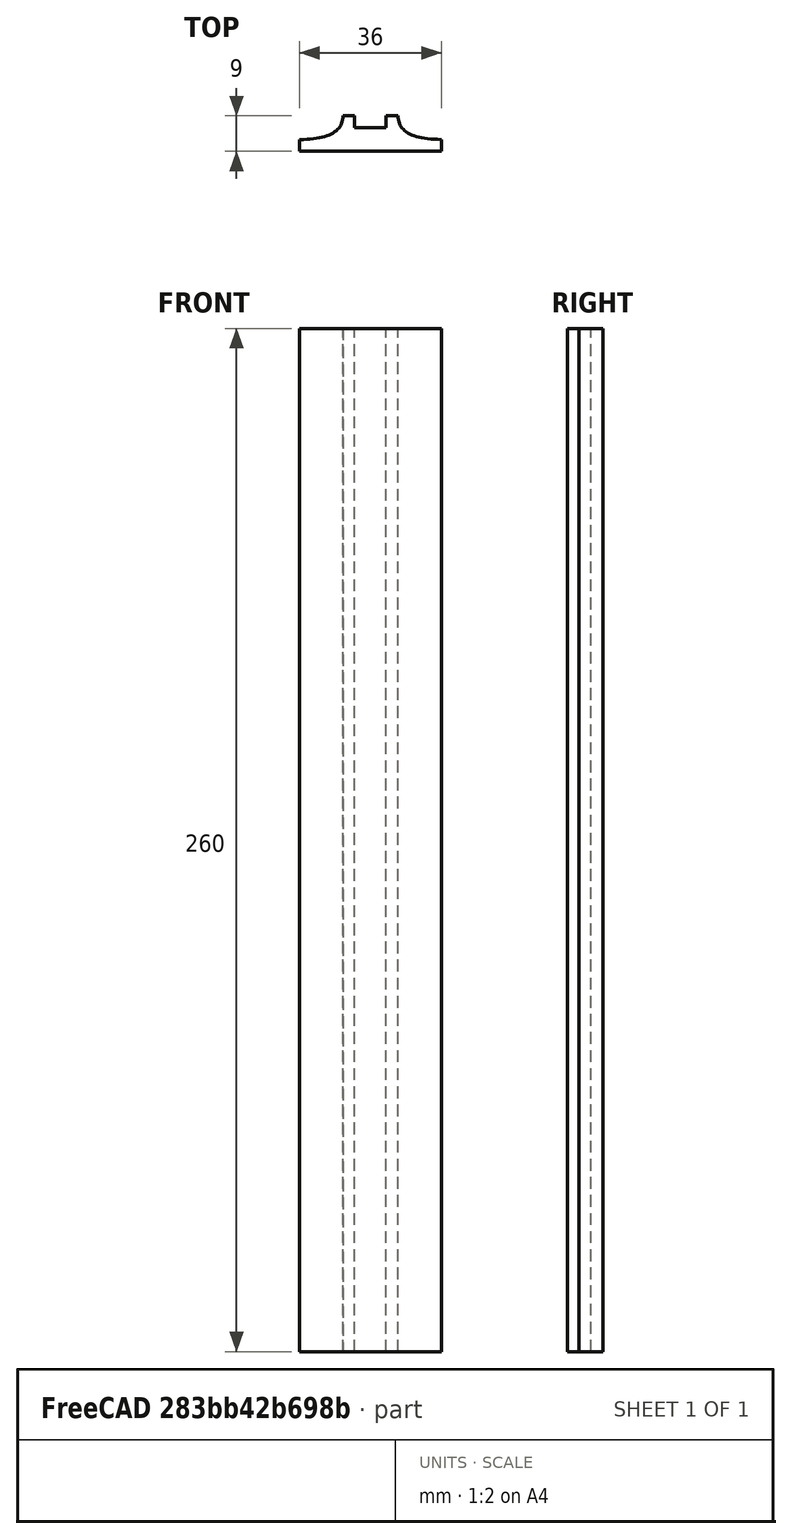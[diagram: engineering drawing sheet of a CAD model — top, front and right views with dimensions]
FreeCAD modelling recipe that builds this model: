
FCSTD DOCUMENT  (FreeCAD 0.19R0.19.2)
Label: laptopStand299.FCStd
License: All rights reserved
LicenseURL: http://en.wikipedia.org/wiki/All_rights_reserved
objects: Sketcher::SketchObject×11, Part::Extrusion×1
note: 12 computed .brp shape members not serialized (recipe doc carries the construction recipe); baked Part::Feature solids carry a one-line shape summary decoded from their .brp

FEATURE [Sketcher::SketchObject] Sketch001  label="legTop"
  FullyConstrained = true
  MapMode = 4
  Placement = pos=(0,0,0) rot=(0.57735,0.57735,0.57735;2.0944rad)
  sketch-geometry (41):
    g0: BSplineCurve PolesCount=3 KnotsCount=2 Degree=2 IsPeriodic=0
    g1: ArcOfCircle CenterX=73.1223 CenterY=-32.291 CenterZ=0 NormalX=0 NormalY=0 NormalZ=1 AngleXU=0 Radius=13 StartAngle=5.92268 EndAngle=9.06428
    g2: ArcOfCircle CenterX=66.7816 CenterY=-49.1439 CenterZ=0 NormalX=0 NormalY=0 NormalZ=1 AngleXU=0 Radius=13 StartAngle=2.78068 EndAngle=5.92131
    g3-g6: Circle x4 (B-spline internal-alignment scaffolding for g7; pole/knot coordinates omitted)
    g7: BSplineCurve PolesCount=4 KnotsCount=2 Degree=3 IsPeriodic=0
    g8: GeomPoint X=28.8094 Y=-19.0875 Z=0
    g9: GeomPoint X=47.0443 Y=-50.4712 Z=0
    g10: Circle CenterX=53.5586 CenterY=-23.2695 CenterZ=0 NormalX=0 NormalY=0 NormalZ=1 AngleXU=0 Radius=3.24518
    g11: LineSegment StartX=17.2232 StartY=-16.0875 StartZ=0 EndX=17.2232 EndY=-19.0875 EndZ=0
    g12: ArcOfCircle CenterX=17.2475 CenterY=-181.166 CenterZ=0 NormalX=0 NormalY=0 NormalZ=1 AngleXU=0 Radius=13 StartAngle=5.92268 EndAngle=7.49361
    g13: ArcOfCircle CenterX=29.5716 CenterY=-148.408 CenterZ=0 NormalX=0 NormalY=0 NormalZ=1 AngleXU=0 Radius=13 StartAngle=4.35228 EndAngle=5.92131
    g14: ArcOfCircle CenterX=35.8967 CenterY=-131.555 CenterZ=0 NormalX=0 NormalY=0 NormalZ=1 AngleXU=0 Radius=13 StartAngle=5.92268 EndAngle=7.49902
    g15: ArcOfCircle CenterX=48.1805 CenterY=-98.7782 CenterZ=0 NormalX=0 NormalY=0 NormalZ=1 AngleXU=0 Radius=13 StartAngle=4.34921 EndAngle=5.92131
    g16: ArcOfCircle CenterX=54.5183 CenterY=-81.9247 CenterZ=0 NormalX=0 NormalY=0 NormalZ=1 AngleXU=0 Radius=13 StartAngle=5.92268 EndAngle=8.70432
    g17: ArcOfCircle CenterX=20.184 CenterY=-217.506 CenterZ=0 NormalX=0 NormalY=0 NormalZ=1 AngleXU=0 Radius=3.81084 StartAngle=1.88136 EndAngle=6.80465
    g18: ArcOfCircle CenterX=36.3663 CenterY=-113.042 CenterZ=0 NormalX=0 NormalY=0 NormalZ=1 AngleXU=0 Radius=3.60555 StartAngle=0.230024 EndAngle=5.3372
    g19: ArcOfCircle CenterX=17.7945 CenterY=-162.686 CenterZ=0 NormalX=0 NormalY=0 NormalZ=1 AngleXU=0 Radius=3.60555 StartAngle=0.230024 EndAngle=5.3372
    g20: ArcOfCircle CenterX=49.8795 CenterY=-62.6074 CenterZ=0 NormalX=0 NormalY=0 NormalZ=1 AngleXU=0 Radius=3.84187 StartAngle=4.46973 EndAngle=9.40343
    g21: LineSegment StartX=48.9563 StartY=-66.3367 StartZ=0 EndX=44.7488 EndY=-73.3482 EndZ=0
    g22: LineSegment StartX=41.085 StartY=-66.3176 StartZ=0 EndX=46.0385 EndY=-62.5254 EndZ=0
    g23: LineSegment StartX=47.0443 StartY=-50.4712 StartZ=0 EndX=41.085 EndY=-66.3176 EndZ=0
    g24: LineSegment StartX=17.2232 StartY=-16.0875 StartZ=0 EndX=117.223 EndY=-16.0875 EndZ=0
    g25: LineSegment StartX=28.8094 StartY=-19.0875 StartZ=0 EndX=17.2232 EndY=-19.0875 EndZ=0
    g26: LineSegment StartX=117.223 StartY=-16.0875 StartZ=0 EndX=117.223 EndY=-19.0875 EndZ=0
    g27: LineSegment StartX=85.2866 StartY=-36.8766 StartZ=0 EndX=78.9396 EndY=-53.7463 EndZ=0
    g28: LineSegment StartX=60.9579 StartY=-27.7053 StartZ=0 EndX=54.6191 EndY=-44.5532 EndZ=0
    g29: LineSegment StartX=23.4884 StartY=-215.608 StartZ=0 EndX=94.6579 EndY=-26.1359 EndZ=0
    g30: LineSegment StartX=19.0195 StartY=-213.878 StartZ=0 EndX=29.4118 EndY=-185.752 EndZ=0
    g31: LineSegment StartX=22.7134 StartY=-166.661 StartZ=0 EndX=21.8316 EndY=-169.001 EndZ=0
    g32: LineSegment StartX=19.9036 StartY=-165.61 StartZ=0 EndX=22.7134 EndY=-166.661 EndZ=0
    g33: LineSegment StartX=21.3051 StartY=-161.864 StartZ=0 EndX=24.1149 EndY=-162.915 EndZ=0
    g34: LineSegment StartX=24.1149 StartY=-162.915 StartZ=0 EndX=24.9906 EndY=-160.574 EndZ=0
    g35: LineSegment StartX=41.7296 StartY=-153.01 StartZ=0 EndX=48.061 EndY=-136.14 EndZ=0
    g36: LineSegment StartX=41.2852 StartY=-117.017 StartZ=0 EndX=40.4148 EndY=-119.365 EndZ=0
    g37: LineSegment StartX=38.4753 StartY=-115.966 StartZ=0 EndX=41.2852 EndY=-117.017 EndZ=0
    g38: LineSegment StartX=39.8769 StartY=-112.22 StartZ=0 EndX=42.6867 EndY=-113.271 EndZ=0
    g39: LineSegment StartX=42.6867 StartY=-113.271 StartZ=0 EndX=43.5622 EndY=-110.93 EndZ=0
    g40: LineSegment StartX=66.6827 StartY=-86.5104 StartZ=0 EndX=60.3386 EndY=-103.381 EndZ=0
  constraints (65):
    c: Block(g0)
    c: Block(g1)
    c: Block(g2)
    c: Weight(g3) = 1
    c: Equal(g3,g4)
    c: Equal(g3,g5)
    c: Equal(g3,g6)
    c: InternalAlignment(g3-g6 -> g7) x4
    c: InternalAlignment(g8,g7)
    c: InternalAlignment(g9,g7)
    c: Block(g10)
    c: Block(g7)
    c: Vertical(g11)
    c: Block(g12)
    c: Block(g13)
    c: Block(g14)
    c: Block(g15)
    c: Block(g16)
    c: Block(g17)
    c: Block(g18)
    c: Block(g19)
    c: Block(g20)
    c: Coincident(g21,g20)
    c: Coincident(g21,g16)
    c: Coincident(g22,g20)
    c: Block(g22)
    c: Coincident(g23,g7)
    c: Coincident(g23,g22)
    c: Coincident(g24,g11)
    c: Horizontal(g24)
    c: Coincident(g25,g7)
    c: Coincident(g25,g11)
    c: Horizontal(g25)
    c: Coincident(g26,g24)
    c: Coincident(g26,g0)
    c: Vertical(g26)
    c: Block(g24)
    c: Coincident(g27,g1)
    c: Coincident(g27,g2)
    c: Coincident(g28,g1)
    c: Coincident(g28,g2)
    c: Coincident(g29,g17)
    c: Coincident(g29,g0)
    c: Coincident(g30,g17)
    c: Coincident(g30,g12)
    c: Coincident(g31,g12)
    c: Coincident(g32,g19)
    c: Coincident(g32,g31)
    c: Block(g31)
    c: Coincident(g33,g19)
    c: Coincident(g34,g33)
    c: Coincident(g34,g13)
    c: Block(g34)
    c: Coincident(g35,g13)
    c: Coincident(g35,g14)
    c: Coincident(g36,g14)
    c: Coincident(g37,g18)
    c: Coincident(g37,g36)
    c: Block(g36)
    c: Coincident(g38,g18)
    c: Coincident(g39,g38)
    c: Coincident(g39,g15)
    c: Block(g39)
    c: Coincident(g40,g16)
    c: Coincident(g40,g15)
FEATURE [Sketcher::SketchObject] Sketch002
  FullyConstrained = true
  sketch-geometry (20):
    g0: LineSegment StartX=-2.77179 StartY=-200.304 StartZ=0 EndX=5.22821 EndY=-200.304 EndZ=0
    g1: LineSegment StartX=5.22821 StartY=-200.304 StartZ=0 EndX=5.22821 EndY=-197.304 EndZ=0
    g2: LineSegment StartX=-2.77179 StartY=-200.304 StartZ=0 EndX=-2.77179 EndY=-197.304 EndZ=0
    g3: LineSegment StartX=5.22821 StartY=-197.304 StartZ=0 EndX=8.22821 EndY=-197.304 EndZ=0
    g4: LineSegment StartX=-2.77179 StartY=-197.304 StartZ=0 EndX=-5.77179 EndY=-197.304 EndZ=0
    g5: LineSegment StartX=19.2282 StartY=-203.304 StartZ=0 EndX=19.2282 EndY=-206.304 EndZ=0
    g6: LineSegment StartX=-16.7718 StartY=-203.304 StartZ=0 EndX=-16.7718 EndY=-206.304 EndZ=0
    g7: LineSegment StartX=-16.7718 StartY=-206.304 StartZ=0 EndX=19.2282 EndY=-206.304 EndZ=0
    g8: Circle CenterX=-16.7718 CenterY=-203.304 CenterZ=0 NormalX=0 NormalY=0 NormalZ=1 AngleXU=0 Radius=1
    g9: Circle CenterX=-5.77179 CenterY=-203.304 CenterZ=0 NormalX=0 NormalY=0 NormalZ=1 AngleXU=0 Radius=1
    g10: Circle CenterX=-5.77179 CenterY=-197.304 CenterZ=0 NormalX=0 NormalY=0 NormalZ=1 AngleXU=0 Radius=1
    g11: BSplineCurve PolesCount=3 KnotsCount=2 Degree=2 IsPeriodic=0
    g12: GeomPoint X=-16.7718 Y=-203.304 Z=0
    g13: GeomPoint X=-5.77179 Y=-197.304 Z=0
    g14: Circle CenterX=19.2282 CenterY=-203.304 CenterZ=0 NormalX=0 NormalY=0 NormalZ=1 AngleXU=0 Radius=1
    g15: Circle CenterX=8.22821 CenterY=-203.304 CenterZ=0 NormalX=0 NormalY=0 NormalZ=1 AngleXU=0 Radius=1
    g16: Circle CenterX=8.22821 CenterY=-197.304 CenterZ=0 NormalX=0 NormalY=0 NormalZ=1 AngleXU=0 Radius=1
    g17: BSplineCurve PolesCount=3 KnotsCount=2 Degree=2 IsPeriodic=0
    g18: GeomPoint X=19.2282 Y=-203.304 Z=0
    g19: GeomPoint X=8.22821 Y=-197.304 Z=0
  constraints (41):
    c: Horizontal(g0)
    c: Distance(g0) = 8
    c: Coincident(g1,g0)
    c: Vertical(g1)
    c: Distance(g1) = 3
    c: Coincident(g2,g0)
    c: Vertical(g2)
    c: Distance(g2) = 3
    c: Coincident(g3,g1)
    c: Horizontal(g3)
    c: Distance(g3) = 3
    c: Coincident(g4,g2)
    c: Horizontal(g4)
    c: Distance(g4) = 3
    c: Vertical(g5)
    c: Vertical(g6)
    c: Coincident(g7,g6)
    c: Coincident(g7,g5)
    c: Weight(g8) = 1
    c: Equal(g8,g9)
    c: Equal(g8,g10)
    c: Coincident(g11,g4)
    c: InternalAlignment(g8,g11)
    c: InternalAlignment(g9,g11)
    c: InternalAlignment(g10,g11)
    c: InternalAlignment(g12,g11)
    c: InternalAlignment(g13,g11)
    c: Coincident(g17,g5)
    c: Weight(g14) = 1
    c: Equal(g14,g15)
    c: Equal(g14,g16)
    c: Coincident(g17,g3)
    c: InternalAlignment(g14,g17)
    c: InternalAlignment(g15,g17)
    c: InternalAlignment(g16,g17)
    c: InternalAlignment(g18,g17)
    c: InternalAlignment(g19,g17)
    c: Block(g7)
    c: Block(g17)
    c: Block(g11)
    c: Block(g6)
FEATURE [Part::Extrusion] Extrude003
  Base = -> Sketch002
  Dir = (0,0,1)
  DirMode = 2
  FaceMakerClass = Part::FaceMakerBullseye
  LengthFwd = 260
  LengthRev = 0
  Solid = true
  Symmetric = false
FEATURE [Sketcher::SketchObject] Sketch003  label="original"
  FullyConstrained = false
  sketch-geometry (469):
    g0: LineSegment StartX=-42.9272 StartY=136.221 StartZ=0 EndX=-42.9272 EndY=-103.779 EndZ=0
    g1: LineSegment StartX=407.073 StartY=136.221 StartZ=0 EndX=407.073 EndY=-103.779 EndZ=0
    g2: ArcOfCircle CenterX=-26.9272 CenterY=-83.7794 CenterZ=0 NormalX=0 NormalY=0 NormalZ=1 AngleXU=0 Radius=8 StartAngle=3.14159 EndAngle=6.28319
    g3: ArcOfCircle CenterX=391.073 CenterY=-83.7794 CenterZ=0 NormalX=0 NormalY=0 NormalZ=1 AngleXU=0 Radius=8 StartAngle=3.14159 EndAngle=6.28319
    g4: Circle CenterX=175.022 CenterY=27.0628 CenterZ=0 NormalX=0 NormalY=0 NormalZ=1 AngleXU=0 Radius=1
    g5: Circle CenterX=179.022 CenterY=24.8665 CenterZ=0 NormalX=0 NormalY=0 NormalZ=1 AngleXU=0 Radius=1
    g6: Circle CenterX=179.022 CenterY=27.0628 CenterZ=0 NormalX=0 NormalY=0 NormalZ=1 AngleXU=0 Radius=1
    g7: BSplineCurve PolesCount=3 KnotsCount=2 Degree=2 IsPeriodic=0
    g8: GeomPoint X=175.022 Y=27.0628 Z=0
    g9: GeomPoint X=179.022 Y=27.0628 Z=0
    g10: Circle CenterX=189.124 CenterY=27.0628 CenterZ=0 NormalX=0 NormalY=0 NormalZ=1 AngleXU=0 Radius=1
    g11: Circle CenterX=185.124 CenterY=24.8665 CenterZ=0 NormalX=0 NormalY=0 NormalZ=1 AngleXU=0 Radius=1
    g12: Circle CenterX=185.124 CenterY=27.0628 CenterZ=0 NormalX=0 NormalY=0 NormalZ=1 AngleXU=0 Radius=1
    g13: BSplineCurve PolesCount=3 KnotsCount=2 Degree=2 IsPeriodic=0
    g14: GeomPoint X=189.124 Y=27.0628 Z=0
    g15: GeomPoint X=185.124 Y=27.0628 Z=0
    g16: Circle CenterX=175.022 CenterY=5.37834 CenterZ=0 NormalX=0 NormalY=0 NormalZ=1 AngleXU=0 Radius=1
    g17: Circle CenterX=179.022 CenterY=7.57463 CenterZ=0 NormalX=0 NormalY=0 NormalZ=1 AngleXU=0 Radius=1
    g18: Circle CenterX=179.022 CenterY=5.34704 CenterZ=0 NormalX=0 NormalY=0 NormalZ=1 AngleXU=0 Radius=1
    g19: BSplineCurve PolesCount=3 KnotsCount=2 Degree=2 IsPeriodic=0
    g20: GeomPoint X=175.022 Y=5.37834 Z=0
    g21: GeomPoint X=179.022 Y=5.34704 Z=0
    g22: Circle CenterX=189.124 CenterY=5.37834 CenterZ=0 NormalX=0 NormalY=0 NormalZ=1 AngleXU=0 Radius=1
    g23: Circle CenterX=185.124 CenterY=7.57463 CenterZ=0 NormalX=0 NormalY=0 NormalZ=1 AngleXU=0 Radius=1
    g24: Circle CenterX=185.124 CenterY=5.34704 CenterZ=0 NormalX=0 NormalY=0 NormalZ=1 AngleXU=0 Radius=1
    g25: BSplineCurve PolesCount=3 KnotsCount=2 Degree=2 IsPeriodic=0
    g26: GeomPoint X=189.124 Y=5.37834 Z=0
    g27: GeomPoint X=185.124 Y=5.34704 Z=0
    g28: Circle CenterX=165.871 CenterY=18.1458 CenterZ=0 NormalX=0 NormalY=0 NormalZ=1 AngleXU=0 Radius=1
    g29: Circle CenterX=169.377 CenterY=16.2206 CenterZ=0 NormalX=0 NormalY=0 NormalZ=1 AngleXU=0 Radius=1
    g30: Circle CenterX=165.871 CenterY=14.2956 CenterZ=0 NormalX=0 NormalY=0 NormalZ=1 AngleXU=0 Radius=1
    g31: BSplineCurve PolesCount=3 KnotsCount=2 Degree=2 IsPeriodic=0
    g32: GeomPoint X=165.871 Y=18.1458 Z=0
    g33: GeomPoint X=165.871 Y=14.2956 Z=0
    g34: Circle CenterX=198.275 CenterY=18.1318 CenterZ=0 NormalX=0 NormalY=0 NormalZ=1 AngleXU=0 Radius=1
    g35: Circle CenterX=194.768 CenterY=16.2206 CenterZ=0 NormalX=0 NormalY=0 NormalZ=1 AngleXU=0 Radius=1
    g36: Circle CenterX=198.264 CenterY=14.2963 CenterZ=0 NormalX=0 NormalY=0 NormalZ=1 AngleXU=0 Radius=1
    g37: BSplineCurve PolesCount=3 KnotsCount=2 Degree=2 IsPeriodic=0
    g38: GeomPoint X=198.275 Y=18.1318 Z=0
    g39: GeomPoint X=198.264 Y=14.2963 Z=0
    g40: LineSegment StartX=407.073 StartY=-103.779 StartZ=0 EndX=-42.9272 EndY=-103.779 EndZ=0
    g41: Circle CenterX=125.607 CenterY=54.1951 CenterZ=0 NormalX=0 NormalY=0 NormalZ=1 AngleXU=0 Radius=1
    g42: Circle CenterX=139.632 CenterY=46.4944 CenterZ=0 NormalX=0 NormalY=0 NormalZ=1 AngleXU=0 Radius=1
    g43: Circle CenterX=127.326 CenterY=56.7187 CenterZ=0 NormalX=0 NormalY=0 NormalZ=1 AngleXU=0 Radius=1
    g44: BSplineCurve PolesCount=3 KnotsCount=2 Degree=2 IsPeriodic=0
    g45: GeomPoint X=125.607 Y=54.1951 Z=0
    g46: GeomPoint X=127.326 Y=56.7187 Z=0
    g47: Circle CenterX=236.824 CenterY=56.7187 CenterZ=0 NormalX=0 NormalY=0 NormalZ=1 AngleXU=0 Radius=1
    g48: Circle CenterX=224.513 CenterY=46.4944 CenterZ=0 NormalX=0 NormalY=0 NormalZ=1 AngleXU=0 Radius=1
    g49: Circle CenterX=238.538 CenterY=54.1951 CenterZ=0 NormalX=0 NormalY=0 NormalZ=1 AngleXU=0 Radius=1
    g50: BSplineCurve PolesCount=3 KnotsCount=2 Degree=2 IsPeriodic=0
    g51: GeomPoint X=236.824 Y=56.7187 Z=0
    g52: GeomPoint X=238.538 Y=54.1951 Z=0
    g53: Circle CenterX=238.538 CenterY=-21.7516 CenterZ=0 NormalX=0 NormalY=0 NormalZ=1 AngleXU=0 Radius=1
    g54: Circle CenterX=224.513 CenterY=-14.0532 CenterZ=0 NormalX=0 NormalY=0 NormalZ=1 AngleXU=0 Radius=1
    g55: Circle CenterX=236.584 CenterY=-24.2775 CenterZ=0 NormalX=0 NormalY=0 NormalZ=1 AngleXU=0 Radius=1
    g56: BSplineCurve PolesCount=3 KnotsCount=2 Degree=2 IsPeriodic=0
    g57: GeomPoint X=238.538 Y=-21.7516 Z=0
    g58: GeomPoint X=236.584 Y=-24.2775 Z=0
    g59: Circle CenterX=125.607 CenterY=-21.7539 CenterZ=0 NormalX=0 NormalY=0 NormalZ=1 AngleXU=0 Radius=1
    g60: Circle CenterX=139.632 CenterY=-14.0532 CenterZ=0 NormalX=0 NormalY=0 NormalZ=1 AngleXU=0 Radius=1
    g61: Circle CenterX=127.325 CenterY=-24.2775 CenterZ=0 NormalX=0 NormalY=0 NormalZ=1 AngleXU=0 Radius=1
    g62: BSplineCurve PolesCount=3 KnotsCount=2 Degree=2 IsPeriodic=0
    g63: GeomPoint X=125.607 Y=-21.7539 Z=0
    g64: GeomPoint X=127.325 Y=-24.2775 Z=0
    g65: Circle CenterX=302.996 CenterY=111.695 CenterZ=0 NormalX=0 NormalY=0 NormalZ=1 AngleXU=0 Radius=1
    g66: Circle CenterX=306.073 CenterY=114.251 CenterZ=0 NormalX=0 NormalY=0 NormalZ=1 AngleXU=0 Radius=1
    g67: Circle CenterX=306.073 CenterY=110.251 CenterZ=0 NormalX=0 NormalY=0 NormalZ=1 AngleXU=0 Radius=1
    g68: BSplineCurve PolesCount=3 KnotsCount=2 Degree=2 IsPeriodic=0
    g69: GeomPoint X=302.996 Y=111.695 Z=0
    g70: GeomPoint X=306.073 Y=110.251 Z=0
    g71: Circle CenterX=306.073 CenterY=95.2763 CenterZ=0 NormalX=0 NormalY=0 NormalZ=1 AngleXU=0 Radius=1
    g72: Circle CenterX=306.073 CenterY=91.2763 CenterZ=0 NormalX=0 NormalY=0 NormalZ=1 AngleXU=0 Radius=1
    g73: Circle CenterX=302.567 CenterY=89.3511 CenterZ=0 NormalX=0 NormalY=0 NormalZ=1 AngleXU=0 Radius=1
    g74: BSplineCurve PolesCount=3 KnotsCount=2 Degree=2 IsPeriodic=0
    g75: GeomPoint X=306.073 Y=95.2763 Z=0
    g76: GeomPoint X=302.567 Y=89.3511 Z=0
    g77: LineSegment StartX=306.073 StartY=110.251 StartZ=0 EndX=306.073 EndY=95.2763 EndZ=0
    g78: LineSegment StartX=302.996 StartY=111.695 StartZ=0 EndX=236.824 EndY=56.7187 EndZ=0
    g79: LineSegment StartX=238.538 StartY=54.1951 StartZ=0 EndX=302.567 EndY=89.3511 EndZ=0
    g80: Circle CenterX=61.1496 CenterY=111.695 CenterZ=0 NormalX=0 NormalY=0 NormalZ=1 AngleXU=0 Radius=1
    g81: Circle CenterX=58.0728 CenterY=114.251 CenterZ=0 NormalX=0 NormalY=0 NormalZ=1 AngleXU=0 Radius=1
    g82: Circle CenterX=58.0728 CenterY=110.251 CenterZ=0 NormalX=0 NormalY=0 NormalZ=1 AngleXU=0 Radius=1
    g83: BSplineCurve PolesCount=3 KnotsCount=2 Degree=2 IsPeriodic=0
    g84: GeomPoint X=61.1496 Y=111.695 Z=0
    g85: GeomPoint X=58.0728 Y=110.251 Z=0
    g86: Circle CenterX=61.5791 CenterY=89.3511 CenterZ=0 NormalX=0 NormalY=0 NormalZ=1 AngleXU=0 Radius=1
    g87: Circle CenterX=58.0728 CenterY=91.2763 CenterZ=0 NormalX=0 NormalY=0 NormalZ=1 AngleXU=0 Radius=1
    g88: Circle CenterX=58.0728 CenterY=95.2763 CenterZ=0 NormalX=0 NormalY=0 NormalZ=1 AngleXU=0 Radius=1
    g89: BSplineCurve PolesCount=3 KnotsCount=2 Degree=2 IsPeriodic=0
    g90: GeomPoint X=61.5791 Y=89.3511 Z=0
    g91: GeomPoint X=58.0728 Y=95.2763 Z=0
    g92: LineSegment StartX=58.0728 StartY=110.251 StartZ=0 EndX=58.0728 EndY=95.2763 EndZ=0
    g93: LineSegment StartX=61.1496 StartY=111.695 StartZ=0 EndX=127.326 EndY=56.7187 EndZ=0
    g94: LineSegment StartX=125.607 StartY=54.1951 StartZ=0 EndX=61.5791 EndY=89.3511 EndZ=0
    g95: Circle CenterX=61.5791 CenterY=-56.9099 CenterZ=0 NormalX=0 NormalY=0 NormalZ=1 AngleXU=0 Radius=1
    g96: Circle CenterX=58.0728 CenterY=-58.8351 CenterZ=0 NormalX=0 NormalY=0 NormalZ=1 AngleXU=0 Radius=1
    g97: Circle CenterX=58.0728 CenterY=-62.8351 CenterZ=0 NormalX=0 NormalY=0 NormalZ=1 AngleXU=0 Radius=1
    g98: BSplineCurve PolesCount=3 KnotsCount=2 Degree=2 IsPeriodic=0
    g99: GeomPoint X=61.5791 Y=-56.9099 Z=0
    g100: GeomPoint X=58.0728 Y=-62.8351 Z=0
    g101: Circle CenterX=58.0728 CenterY=-77.8102 CenterZ=0 NormalX=0 NormalY=0 NormalZ=1 AngleXU=0 Radius=1
    g102: Circle CenterX=58.0728 CenterY=-81.8102 CenterZ=0 NormalX=0 NormalY=0 NormalZ=1 AngleXU=0 Radius=1
    g103: Circle CenterX=61.1496 CenterY=-79.2541 CenterZ=0 NormalX=0 NormalY=0 NormalZ=1 AngleXU=0 Radius=1
    g104: BSplineCurve PolesCount=3 KnotsCount=2 Degree=2 IsPeriodic=0
    g105: GeomPoint X=58.0728 Y=-77.8102 Z=0
    g106: GeomPoint X=61.1496 Y=-79.2541 Z=0
    g107: LineSegment StartX=58.0728 StartY=-62.8351 StartZ=0 EndX=58.0728 EndY=-77.8102 EndZ=0
    g108: LineSegment StartX=61.1496 StartY=-79.2541 StartZ=0 EndX=127.325 EndY=-24.2775 EndZ=0
    g109: LineSegment StartX=125.607 StartY=-21.7539 StartZ=0 EndX=61.5791 EndY=-56.9099 EndZ=0
    g110: Circle CenterX=302.567 CenterY=-56.9099 CenterZ=0 NormalX=0 NormalY=0 NormalZ=1 AngleXU=0 Radius=1
    g111: Circle CenterX=306.073 CenterY=-58.8351 CenterZ=0 NormalX=0 NormalY=0 NormalZ=1 AngleXU=0 Radius=1
    g112: Circle CenterX=306.073 CenterY=-62.8351 CenterZ=0 NormalX=0 NormalY=0 NormalZ=1 AngleXU=0 Radius=1
    g113: BSplineCurve PolesCount=3 KnotsCount=2 Degree=2 IsPeriodic=0
    g114: GeomPoint X=302.567 Y=-56.9099 Z=0
    g115: GeomPoint X=306.073 Y=-62.8351 Z=0
    g116: Circle CenterX=302.996 CenterY=-79.2541 CenterZ=0 NormalX=0 NormalY=0 NormalZ=1 AngleXU=0 Radius=1
    g117: Circle CenterX=306.073 CenterY=-81.8102 CenterZ=0 NormalX=0 NormalY=0 NormalZ=1 AngleXU=0 Radius=1
    g118: Circle CenterX=306.073 CenterY=-77.8102 CenterZ=0 NormalX=0 NormalY=0 NormalZ=1 AngleXU=0 Radius=1
    g119: BSplineCurve PolesCount=3 KnotsCount=2 Degree=2 IsPeriodic=0
    g120: GeomPoint X=302.996 Y=-79.2541 Z=0
    g121: GeomPoint X=306.073 Y=-77.8102 Z=0
    g122: LineSegment StartX=306.073 StartY=-62.8351 StartZ=0 EndX=306.073 EndY=-77.8102 EndZ=0
    g123: LineSegment StartX=302.996 StartY=-79.2541 StartZ=0 EndX=236.584 EndY=-24.2775 EndZ=0
    g124: LineSegment StartX=238.538 StartY=-21.7516 StartZ=0 EndX=302.567 EndY=-56.9099 EndZ=0
    g125: Circle CenterX=61.6457 CenterY=-88.8112 CenterZ=0 NormalX=0 NormalY=0 NormalZ=1 AngleXU=0 Radius=1
    g126: Circle CenterX=58.0728 CenterY=-91.7794 CenterZ=0 NormalX=0 NormalY=0 NormalZ=1 AngleXU=0 Radius=1
    g127: Circle CenterX=63.9135 CenterY=-91.7791 CenterZ=0 NormalX=0 NormalY=0 NormalZ=1 AngleXU=0 Radius=1
    g128: BSplineCurve PolesCount=3 KnotsCount=2 Degree=2 IsPeriodic=0
    g129: GeomPoint X=61.6457 Y=-88.8112 Z=0
    g130: GeomPoint X=63.9135 Y=-91.7791 Z=0
    g131: Circle CenterX=179.022 CenterY=-85.8163 CenterZ=0 NormalX=0 NormalY=0 NormalZ=1 AngleXU=0 Radius=1
    g132: Circle CenterX=179.022 CenterY=-91.7794 CenterZ=0 NormalX=0 NormalY=0 NormalZ=1 AngleXU=0 Radius=1
    g133: Circle CenterX=171.895 CenterY=-91.7791 CenterZ=0 NormalX=0 NormalY=0 NormalZ=1 AngleXU=0 Radius=1
    g134: BSplineCurve PolesCount=3 KnotsCount=2 Degree=2 IsPeriodic=0
    g135: GeomPoint X=179.022 Y=-85.8163 Z=0
    g136: GeomPoint X=171.895 Y=-91.7791 Z=0
    g137: Circle CenterX=185.124 CenterY=-86.2028 CenterZ=0 NormalX=0 NormalY=0 NormalZ=1 AngleXU=0 Radius=1
    g138: Circle CenterX=185.124 CenterY=-91.7794 CenterZ=0 NormalX=0 NormalY=0 NormalZ=1 AngleXU=0 Radius=1
    g139: Circle CenterX=191.747 CenterY=-91.7794 CenterZ=0 NormalX=0 NormalY=0 NormalZ=1 AngleXU=0 Radius=1
    g140: BSplineCurve PolesCount=3 KnotsCount=2 Degree=2 IsPeriodic=0
    g141: GeomPoint X=185.124 Y=-86.2028 Z=0
    g142: GeomPoint X=191.747 Y=-91.7794 Z=0
    g143: Circle CenterX=299.888 CenterY=-86.6413 CenterZ=0 NormalX=0 NormalY=0 NormalZ=1 AngleXU=0 Radius=1
    g144: Circle CenterX=306.073 CenterY=-91.7794 CenterZ=0 NormalX=0 NormalY=0 NormalZ=1 AngleXU=0 Radius=1
    g145: Circle CenterX=298.776 CenterY=-91.7794 CenterZ=0 NormalX=0 NormalY=0 NormalZ=1 AngleXU=0 Radius=1
    g146: BSplineCurve PolesCount=3 KnotsCount=2 Degree=2 IsPeriodic=0
    g147: GeomPoint X=299.888 Y=-86.6413 Z=0
    g148: GeomPoint X=298.776 Y=-91.7794 Z=0
    g149: LineSegment StartX=189.124 StartY=5.37834 StartZ=0 EndX=299.888 EndY=-86.6413 EndZ=0
    g150: LineSegment StartX=298.776 StartY=-91.7794 StartZ=0 EndX=191.747 EndY=-91.7794 EndZ=0
    g151: LineSegment StartX=185.124 StartY=-86.2028 StartZ=0 EndX=185.124 EndY=5.34704 EndZ=0
    g152: LineSegment StartX=179.022 StartY=5.34704 StartZ=0 EndX=179.022 EndY=-85.8163 EndZ=0
    g153: LineSegment StartX=171.895 StartY=-91.7791 StartZ=0 EndX=63.9135 EndY=-91.7791 EndZ=0
    g154: LineSegment StartX=61.6457 StartY=-88.8112 StartZ=0 EndX=175.022 EndY=5.37834 EndZ=0
    g155: Circle CenterX=302.073 CenterY=124.221 CenterZ=0 NormalX=0 NormalY=0 NormalZ=1 AngleXU=0 Radius=1
    g156: Circle CenterX=306.073 CenterY=124.221 CenterZ=0 NormalX=0 NormalY=0 NormalZ=1 AngleXU=0 Radius=1
    g157: Circle CenterX=302.996 CenterY=121.665 CenterZ=0 NormalX=0 NormalY=0 NormalZ=1 AngleXU=0 Radius=1
    g158: BSplineCurve PolesCount=3 KnotsCount=2 Degree=2 IsPeriodic=0
    g159: GeomPoint X=302.073 Y=124.221 Z=0
    g160: GeomPoint X=302.996 Y=121.665 Z=0
    g161: Circle CenterX=189.124 CenterY=124.221 CenterZ=0 NormalX=0 NormalY=0 NormalZ=1 AngleXU=0 Radius=1
    g162: Circle CenterX=185.124 CenterY=124.221 CenterZ=0 NormalX=0 NormalY=0 NormalZ=1 AngleXU=0 Radius=1
    g163: Circle CenterX=185.124 CenterY=120.221 CenterZ=0 NormalX=0 NormalY=0 NormalZ=1 AngleXU=0 Radius=1
    g164: BSplineCurve PolesCount=3 KnotsCount=2 Degree=2 IsPeriodic=0
    g165: GeomPoint X=189.124 Y=124.221 Z=0
    g166: GeomPoint X=185.124 Y=120.221 Z=0
    g167: Circle CenterX=175.022 CenterY=124.221 CenterZ=0 NormalX=0 NormalY=0 NormalZ=1 AngleXU=0 Radius=1
    g168: Circle CenterX=179.022 CenterY=124.221 CenterZ=0 NormalX=0 NormalY=0 NormalZ=1 AngleXU=0 Radius=1
    g169: Circle CenterX=179.022 CenterY=120.221 CenterZ=0 NormalX=0 NormalY=0 NormalZ=1 AngleXU=0 Radius=1
    g170: BSplineCurve PolesCount=3 KnotsCount=2 Degree=2 IsPeriodic=0
    g171: GeomPoint X=175.022 Y=124.221 Z=0
    g172: GeomPoint X=179.022 Y=120.221 Z=0
    g173: Circle CenterX=62.0728 CenterY=124.221 CenterZ=0 NormalX=0 NormalY=0 NormalZ=1 AngleXU=0 Radius=1
    g174: Circle CenterX=58.0728 CenterY=124.221 CenterZ=0 NormalX=0 NormalY=0 NormalZ=1 AngleXU=0 Radius=1
    g175: Circle CenterX=61.1496 CenterY=121.665 CenterZ=0 NormalX=0 NormalY=0 NormalZ=1 AngleXU=0 Radius=1
    g176: BSplineCurve PolesCount=3 KnotsCount=2 Degree=2 IsPeriodic=0
    g177: GeomPoint X=62.0728 Y=124.221 Z=0
    g178: GeomPoint X=61.1496 Y=121.665 Z=0
    g179: LineSegment StartX=179.022 StartY=120.221 StartZ=0 EndX=179.022 EndY=27.0628 EndZ=0
    g180: LineSegment StartX=185.124 StartY=27.0628 StartZ=0 EndX=185.124 EndY=120.221 EndZ=0
    g181: LineSegment StartX=302.996 StartY=121.665 StartZ=0 EndX=189.124 EndY=27.0628 EndZ=0
    g182: LineSegment StartX=175.022 StartY=27.0628 StartZ=0 EndX=61.1496 EndY=121.665 EndZ=0
    g183: Circle CenterX=61.5791 CenterY=75.4095 CenterZ=0 NormalX=0 NormalY=0 NormalZ=1 AngleXU=0 Radius=1
    g184: Circle CenterX=58.0728 CenterY=77.3346 CenterZ=0 NormalX=0 NormalY=0 NormalZ=1 AngleXU=0 Radius=1
    g185: Circle CenterX=58.0728 CenterY=73.3346 CenterZ=0 NormalX=0 NormalY=0 NormalZ=1 AngleXU=0 Radius=1
    g186: BSplineCurve PolesCount=3 KnotsCount=2 Degree=2 IsPeriodic=0
    g187: GeomPoint X=61.5791 Y=75.4095 Z=0
    g188: GeomPoint X=58.0728 Y=73.3346 Z=0
    g189: Circle CenterX=58.0728 CenterY=-40.8935 CenterZ=0 NormalX=0 NormalY=0 NormalZ=1 AngleXU=0 Radius=1
    g190: Circle CenterX=58.0728 CenterY=-44.8935 CenterZ=0 NormalX=0 NormalY=0 NormalZ=1 AngleXU=0 Radius=1
    g191: Circle CenterX=61.5791 CenterY=-42.9683 CenterZ=0 NormalX=0 NormalY=0 NormalZ=1 AngleXU=0 Radius=1
    g192: BSplineCurve PolesCount=3 KnotsCount=2 Degree=2 IsPeriodic=0
    g193: GeomPoint X=58.0728 Y=-40.8935 Z=0
    g194: GeomPoint X=61.5791 Y=-42.9683 Z=0
    g195: LineSegment StartX=61.5791 StartY=-42.9683 StartZ=0 EndX=165.871 EndY=14.2956 EndZ=0
    g196: LineSegment StartX=165.871 StartY=18.1458 StartZ=0 EndX=61.5791 EndY=75.4095 EndZ=0
    g197: LineSegment StartX=58.0728 StartY=73.3346 StartZ=0 EndX=58.0728 EndY=-40.8935 EndZ=0
    g198: Circle CenterX=302.567 CenterY=-42.9683 CenterZ=0 NormalX=0 NormalY=0 NormalZ=1 AngleXU=0 Radius=1
    g199: Circle CenterX=306.073 CenterY=-44.8935 CenterZ=0 NormalX=0 NormalY=0 NormalZ=1 AngleXU=0 Radius=1
    g200: Circle CenterX=306.073 CenterY=-40.8935 CenterZ=0 NormalX=0 NormalY=0 NormalZ=1 AngleXU=0 Radius=1
    g201: BSplineCurve PolesCount=3 KnotsCount=2 Degree=2 IsPeriodic=0
    g202: GeomPoint X=302.567 Y=-42.9683 Z=0
    g203: GeomPoint X=306.073 Y=-40.8935 Z=0
    g204: Circle CenterX=306.073 CenterY=73.3346 CenterZ=0 NormalX=0 NormalY=0 NormalZ=1 AngleXU=0 Radius=1
    g205: Circle CenterX=306.073 CenterY=77.3346 CenterZ=0 NormalX=0 NormalY=0 NormalZ=1 AngleXU=0 Radius=1
    g206: Circle CenterX=302.535 CenterY=75.4095 CenterZ=0 NormalX=0 NormalY=0 NormalZ=1 AngleXU=0 Radius=1
    g207: BSplineCurve PolesCount=3 KnotsCount=2 Degree=2 IsPeriodic=0
    g208: GeomPoint X=306.073 Y=73.3346 Z=0
    g209: GeomPoint X=302.535 Y=75.4095 Z=0
    g210: LineSegment StartX=302.567 StartY=-42.9683 StartZ=0 EndX=198.264 EndY=14.2963 EndZ=0
    g211: LineSegment StartX=198.275 StartY=18.1318 StartZ=0 EndX=302.535 EndY=75.4095 EndZ=0
    g212: LineSegment StartX=306.073 StartY=73.3346 StartZ=0 EndX=306.073 EndY=-40.8935 EndZ=0
    g213: LineSegment StartX=322.073 StartY=105.865 StartZ=0 EndX=328.643 EndY=105.865 EndZ=0
    g214: LineSegment StartX=318.073 StartY=120.221 StartZ=0 EndX=318.073 EndY=109.865 EndZ=0
    g215: LineSegment StartX=336.157 StartY=107.779 StartZ=0 EndX=362.567 EndY=122.294 EndZ=0
    g216: Circle CenterX=362.073 CenterY=124.221 CenterZ=0 NormalX=0 NormalY=0 NormalZ=1 AngleXU=0 Radius=1
    g217: Circle CenterX=366.073 CenterY=124.221 CenterZ=0 NormalX=0 NormalY=0 NormalZ=1 AngleXU=0 Radius=1
    g218: Circle CenterX=362.567 CenterY=122.294 CenterZ=0 NormalX=0 NormalY=0 NormalZ=1 AngleXU=0 Radius=1
    g219: BSplineCurve PolesCount=3 KnotsCount=2 Degree=2 IsPeriodic=0
    g220: GeomPoint X=362.073 Y=124.221 Z=0
    g221: GeomPoint X=362.567 Y=122.294 Z=0
    g222: Circle CenterX=322.073 CenterY=124.221 CenterZ=0 NormalX=0 NormalY=0 NormalZ=1 AngleXU=0 Radius=1
    g223: Circle CenterX=318.073 CenterY=124.221 CenterZ=0 NormalX=0 NormalY=0 NormalZ=1 AngleXU=0 Radius=1
    g224: Circle CenterX=318.073 CenterY=120.221 CenterZ=0 NormalX=0 NormalY=0 NormalZ=1 AngleXU=0 Radius=1
    g225: BSplineCurve PolesCount=3 KnotsCount=2 Degree=2 IsPeriodic=0
    g226: GeomPoint X=322.073 Y=124.221 Z=0
    g227: GeomPoint X=318.073 Y=120.221 Z=0
    g228: Circle CenterX=322.073 CenterY=105.865 CenterZ=0 NormalX=0 NormalY=0 NormalZ=1 AngleXU=0 Radius=1
    g229: Circle CenterX=318.073 CenterY=105.865 CenterZ=0 NormalX=0 NormalY=0 NormalZ=1 AngleXU=0 Radius=1
    g230: Circle CenterX=318.073 CenterY=109.865 CenterZ=0 NormalX=0 NormalY=0 NormalZ=1 AngleXU=0 Radius=1
    g231: BSplineCurve PolesCount=3 KnotsCount=2 Degree=2 IsPeriodic=0
    g232: GeomPoint X=322.073 Y=105.865 Z=0
    g233: GeomPoint X=318.073 Y=109.865 Z=0
    g234: Circle CenterX=336.157 CenterY=107.779 CenterZ=0 NormalX=0 NormalY=0 NormalZ=1 AngleXU=0 Radius=1
    g235: Circle CenterX=332.651 CenterY=105.853 CenterZ=0 NormalX=0 NormalY=0 NormalZ=1 AngleXU=0 Radius=1
    g236: Circle CenterX=328.643 CenterY=105.865 CenterZ=0 NormalX=0 NormalY=0 NormalZ=1 AngleXU=0 Radius=1
    g237: BSplineCurve PolesCount=3 KnotsCount=2 Degree=2 IsPeriodic=0
    g238: GeomPoint X=336.157 Y=107.779 Z=0
    g239: GeomPoint X=328.643 Y=105.865 Z=0
    g240: LineSegment StartX=322.073 StartY=124.221 StartZ=0 EndX=362.073 EndY=124.221 EndZ=0
    g241: Circle CenterX=371.567 CenterY=-80.8644 CenterZ=0 NormalX=0 NormalY=0 NormalZ=1 AngleXU=0 Radius=1
    g242: Circle CenterX=375.073 CenterY=-82.7896 CenterZ=0 NormalX=0 NormalY=0 NormalZ=1 AngleXU=0 Radius=1
    g243: Circle CenterX=375.073 CenterY=-78.7896 CenterZ=0 NormalX=0 NormalY=0 NormalZ=1 AngleXU=0 Radius=1
    g244: BSplineCurve PolesCount=3 KnotsCount=2 Degree=2 IsPeriodic=0
    g245: GeomPoint X=371.567 Y=-80.8644 Z=0
    g246: GeomPoint X=375.073 Y=-78.7896 Z=0
    g247: Circle CenterX=321.579 CenterY=-53.4075 CenterZ=0 NormalX=0 NormalY=0 NormalZ=1 AngleXU=0 Radius=1
    g248: Circle CenterX=318.073 CenterY=-51.4823 CenterZ=0 NormalX=0 NormalY=0 NormalZ=1 AngleXU=0 Radius=1
    g249: Circle CenterX=318.073 CenterY=-47.4805 CenterZ=0 NormalX=0 NormalY=0 NormalZ=1 AngleXU=0 Radius=1
    g250: BSplineCurve PolesCount=3 KnotsCount=2 Degree=2 IsPeriodic=0
    g251: GeomPoint X=321.579 Y=-53.4075 Z=0
    g252: GeomPoint X=318.073 Y=-47.4805 Z=0
    g253: LineSegment StartX=371.567 StartY=-80.8644 StartZ=0 EndX=321.579 EndY=-53.4075 EndZ=0
    g254: Circle CenterX=321.579 CenterY=-67.3492 CenterZ=0 NormalX=0 NormalY=0 NormalZ=1 AngleXU=0 Radius=1
    g255: Circle CenterX=318.073 CenterY=-65.424 CenterZ=0 NormalX=0 NormalY=0 NormalZ=1 AngleXU=0 Radius=1
    g256: Circle CenterX=318.073 CenterY=-69.424 CenterZ=0 NormalX=0 NormalY=0 NormalZ=1 AngleXU=0 Radius=1
    g257: BSplineCurve PolesCount=3 KnotsCount=2 Degree=2 IsPeriodic=0
    g258: GeomPoint X=321.579 Y=-67.3492 Z=0
    g259: GeomPoint X=318.073 Y=-69.424 Z=0
    g260: Circle CenterX=362.567 CenterY=-89.8542 CenterZ=0 NormalX=0 NormalY=0 NormalZ=1 AngleXU=0 Radius=1
    g261: Circle CenterX=366.073 CenterY=-91.7794 CenterZ=0 NormalX=0 NormalY=0 NormalZ=1 AngleXU=0 Radius=1
    g262: Circle CenterX=362.073 CenterY=-91.7794 CenterZ=0 NormalX=0 NormalY=0 NormalZ=1 AngleXU=0 Radius=1
    g263: BSplineCurve PolesCount=3 KnotsCount=2 Degree=2 IsPeriodic=0
    g264: GeomPoint X=362.567 Y=-89.8542 Z=0
    g265: GeomPoint X=362.073 Y=-91.7794 Z=0
    g266: Circle CenterX=322.073 CenterY=-91.7794 CenterZ=0 NormalX=0 NormalY=0 NormalZ=1 AngleXU=0 Radius=1
    g267: Circle CenterX=318.073 CenterY=-91.7794 CenterZ=0 NormalX=0 NormalY=0 NormalZ=1 AngleXU=0 Radius=1
    g268: Circle CenterX=318.073 CenterY=-87.7794 CenterZ=0 NormalX=0 NormalY=0 NormalZ=1 AngleXU=0 Radius=1
    g269: BSplineCurve PolesCount=3 KnotsCount=2 Degree=2 IsPeriodic=0
    g270: GeomPoint X=322.073 Y=-91.7794 Z=0
    g271: GeomPoint X=318.073 Y=-87.7794 Z=0
    g272: LineSegment StartX=362.567 StartY=-89.8542 StartZ=0 EndX=321.579 EndY=-67.3492 EndZ=0
    g273: LineSegment StartX=318.073 StartY=-69.424 StartZ=0 EndX=318.073 EndY=-87.7794 EndZ=0
    g274: LineSegment StartX=322.073 StartY=-91.7794 StartZ=0 EndX=362.073 EndY=-91.7794 EndZ=0
    g275: Circle CenterX=2.07281 CenterY=124.221 CenterZ=0 NormalX=0 NormalY=0 NormalZ=1 AngleXU=0 Radius=1
    g276: Circle CenterX=1.57905 CenterY=122.295 CenterZ=0 NormalX=0 NormalY=0 NormalZ=1 AngleXU=0 Radius=1
    g277: BSplineCurve PolesCount=3 KnotsCount=2 Degree=2 IsPeriodic=0
    g278: GeomPoint X=2.07281 Y=124.221 Z=0
    g279: GeomPoint X=1.57905 Y=122.295 Z=0
    g280: Circle CenterX=42.0728 CenterY=124.221 CenterZ=0 NormalX=0 NormalY=0 NormalZ=1 AngleXU=0 Radius=1
    g281: Circle CenterX=46.0728 CenterY=124.221 CenterZ=0 NormalX=0 NormalY=0 NormalZ=1 AngleXU=0 Radius=1
    g282: Circle CenterX=46.0728 CenterY=120.221 CenterZ=0 NormalX=0 NormalY=0 NormalZ=1 AngleXU=0 Radius=1
    g283: BSplineCurve PolesCount=3 KnotsCount=2 Degree=2 IsPeriodic=0
    g284: GeomPoint X=42.0728 Y=124.221 Z=0
    g285: GeomPoint X=46.0728 Y=120.221 Z=0
    g286: Circle CenterX=46.0728 CenterY=109.865 CenterZ=0 NormalX=0 NormalY=0 NormalZ=1 AngleXU=0 Radius=1
    g287: Circle CenterX=46.0728 CenterY=105.865 CenterZ=0 NormalX=0 NormalY=0 NormalZ=1 AngleXU=0 Radius=1
    g288: Circle CenterX=42.0728 CenterY=105.865 CenterZ=0 NormalX=0 NormalY=0 NormalZ=1 AngleXU=0 Radius=1
    g289: BSplineCurve PolesCount=3 KnotsCount=2 Degree=2 IsPeriodic=0
    g290: GeomPoint X=46.0728 Y=109.865 Z=0
    g291: GeomPoint X=42.0728 Y=105.865 Z=0
    g292: Circle CenterX=35.5028 CenterY=105.865 CenterZ=0 NormalX=0 NormalY=0 NormalZ=1 AngleXU=0 Radius=1
    g293: Circle CenterX=31.5028 CenterY=105.865 CenterZ=0 NormalX=0 NormalY=0 NormalZ=1 AngleXU=0 Radius=1
    g294: Circle CenterX=27.9965 CenterY=107.79 CenterZ=0 NormalX=0 NormalY=0 NormalZ=1 AngleXU=0 Radius=1
    g295: BSplineCurve PolesCount=3 KnotsCount=2 Degree=2 IsPeriodic=0
    g296: GeomPoint X=35.5028 Y=105.865 Z=0
    g297: GeomPoint X=27.9965 Y=107.79 Z=0
    g298: LineSegment StartX=2.07281 StartY=124.221 StartZ=0 EndX=42.0728 EndY=124.221 EndZ=0
    g299: LineSegment StartX=46.0728 StartY=120.221 StartZ=0 EndX=46.0728 EndY=109.865 EndZ=0
    g300: LineSegment StartX=42.0728 StartY=105.865 StartZ=0 EndX=35.5028 EndY=105.865 EndZ=0
    g301: LineSegment StartX=27.9965 StartY=107.79 StartZ=0 EndX=1.57905 EndY=122.295 EndZ=0
    g302: Circle CenterX=42.5666 CenterY=-67.3492 CenterZ=0 NormalX=0 NormalY=0 NormalZ=1 AngleXU=0 Radius=1
    g303: Circle CenterX=46.0728 CenterY=-65.424 CenterZ=0 NormalX=0 NormalY=0 NormalZ=1 AngleXU=0 Radius=1
    g304: Circle CenterX=46.0728 CenterY=-69.424 CenterZ=0 NormalX=0 NormalY=0 NormalZ=1 AngleXU=0 Radius=1
    g305: BSplineCurve PolesCount=3 KnotsCount=2 Degree=2 IsPeriodic=0
    g306: GeomPoint X=42.5666 Y=-67.3492 Z=0
    g307: GeomPoint X=46.0728 Y=-69.424 Z=0
    g308: Circle CenterX=46.0728 CenterY=-87.7794 CenterZ=0 NormalX=0 NormalY=0 NormalZ=1 AngleXU=0 Radius=1
    g309: Circle CenterX=46.0728 CenterY=-91.7794 CenterZ=0 NormalX=0 NormalY=0 NormalZ=1 AngleXU=0 Radius=1
    g310: Circle CenterX=42.0728 CenterY=-91.7794 CenterZ=0 NormalX=0 NormalY=0 NormalZ=1 AngleXU=0 Radius=1
    g311: BSplineCurve PolesCount=3 KnotsCount=2 Degree=2 IsPeriodic=0
    g312: GeomPoint X=46.0728 Y=-87.7794 Z=0
    g313: GeomPoint X=42.0728 Y=-91.7794 Z=0
    g314: Circle CenterX=2.07281 CenterY=-91.7794 CenterZ=0 NormalX=0 NormalY=0 NormalZ=1 AngleXU=0 Radius=1
    g315: Circle CenterX=-1.92719 CenterY=-91.7794 CenterZ=0 NormalX=0 NormalY=0 NormalZ=1 AngleXU=0 Radius=1
    g316: Circle CenterX=1.57905 CenterY=-89.8542 CenterZ=0 NormalX=0 NormalY=0 NormalZ=1 AngleXU=0 Radius=1
    g317: BSplineCurve PolesCount=3 KnotsCount=2 Degree=2 IsPeriodic=0
    g318: GeomPoint X=2.07281 Y=-91.7794 Z=0
    g319: GeomPoint X=1.57905 Y=-89.8542 Z=0
    g320: LineSegment StartX=2.07281 StartY=-91.7794 StartZ=0 EndX=42.0728 EndY=-91.7794 EndZ=0
    g321: LineSegment StartX=46.0728 StartY=-87.7794 StartZ=0 EndX=46.0728 EndY=-69.424 EndZ=0
    g322: LineSegment StartX=42.5666 StartY=-67.3492 StartZ=0 EndX=1.57905 EndY=-89.8542 EndZ=0
    g323: Circle CenterX=322.073 CenterY=76.4095 CenterZ=0 NormalX=0 NormalY=0 NormalZ=1 AngleXU=0 Radius=4
    g324: BSplineCurve PolesCount=3 KnotsCount=2 Degree=2 IsPeriodic=0
    g325: GeomPoint X=318.073 Y=72.4095 Z=0
    g326: GeomPoint X=322.073 Y=76.4095 Z=0
    g327: Circle CenterX=375.073 CenterY=72.4095 CenterZ=0 NormalX=0 NormalY=0 NormalZ=1 AngleXU=0 Radius=1
    g328: Circle CenterX=375.073 CenterY=76.4095 CenterZ=0 NormalX=0 NormalY=0 NormalZ=1 AngleXU=0 Radius=1
    g329: Circle CenterX=371.073 CenterY=76.4095 CenterZ=0 NormalX=0 NormalY=0 NormalZ=1 AngleXU=0 Radius=1
    g330: BSplineCurve PolesCount=3 KnotsCount=2 Degree=2 IsPeriodic=0
    g331: GeomPoint X=375.073 Y=72.4095 Z=0
    g332: GeomPoint X=371.073 Y=76.4095 Z=0
    g333: LineSegment StartX=322.073 StartY=76.4095 StartZ=0 EndX=371.073 EndY=76.4095 EndZ=0
    g334: LineSegment StartX=318.073 StartY=72.4095 StartZ=0 EndX=318.073 EndY=-47.4805 EndZ=0
    g335: LineSegment StartX=375.073 StartY=72.4095 StartZ=0 EndX=375.073 EndY=-78.7896 EndZ=0
    g336: ArcOfCircle CenterX=-26.9272 CenterY=22.1087 CenterZ=0 NormalX=0 NormalY=0 NormalZ=1 AngleXU=0 Radius=4 StartAngle=5e-16 EndAngle=3.14159
    g337: LineSegment StartX=-22.9272 StartY=22.1087 StartZ=0 EndX=-18.9272 EndY=-83.7794 EndZ=0
    g338: LineSegment StartX=-34.9272 StartY=-83.7794 StartZ=0 EndX=-30.9272 EndY=22.1087 EndZ=0
    g339: ArcOfCircle CenterX=391.073 CenterY=22.1087 CenterZ=0 NormalX=0 NormalY=0 NormalZ=1 AngleXU=0 Radius=4 StartAngle=0 EndAngle=3.14159
    g340: LineSegment StartX=387.073 StartY=22.1087 StartZ=0 EndX=383.073 EndY=-83.7794 EndZ=0
    g341: LineSegment StartX=395.073 StartY=22.1087 StartZ=0 EndX=399.073 EndY=-83.7794 EndZ=0
    g342: Circle CenterX=-10.9272 CenterY=-78.7794 CenterZ=0 NormalX=0 NormalY=0 NormalZ=1 AngleXU=0 Radius=1
    g343: Circle CenterX=-10.9272 CenterY=-82.7794 CenterZ=0 NormalX=0 NormalY=0 NormalZ=1 AngleXU=0 Radius=1
    g344: Circle CenterX=-7.42095 CenterY=-80.8542 CenterZ=0 NormalX=0 NormalY=0 NormalZ=1 AngleXU=0 Radius=1
    g345: BSplineCurve PolesCount=3 KnotsCount=2 Degree=2 IsPeriodic=0
    g346: GeomPoint X=-10.9272 Y=-78.7794 Z=0
    g347: GeomPoint X=-7.42095 Y=-80.8542 Z=0
    g348: Circle CenterX=42.5666 CenterY=-53.4075 CenterZ=0 NormalX=0 NormalY=0 NormalZ=1 AngleXU=0 Radius=1
    g349: Circle CenterX=46.0728 CenterY=-51.4823 CenterZ=0 NormalX=0 NormalY=0 NormalZ=1 AngleXU=0 Radius=1
    g350: Circle CenterX=46.0728 CenterY=-47.4823 CenterZ=0 NormalX=0 NormalY=0 NormalZ=1 AngleXU=0 Radius=1
    g351: BSplineCurve PolesCount=3 KnotsCount=2 Degree=2 IsPeriodic=0
    g352: GeomPoint X=42.5666 Y=-53.4075 Z=0
    g353: GeomPoint X=46.0728 Y=-47.4823 Z=0
    g354: Circle CenterX=46.0728 CenterY=72.4095 CenterZ=0 NormalX=0 NormalY=0 NormalZ=1 AngleXU=0 Radius=1
    g355: Circle CenterX=46.0728 CenterY=76.4095 CenterZ=0 NormalX=0 NormalY=0 NormalZ=1 AngleXU=0 Radius=1
    g356: Circle CenterX=42.0728 CenterY=76.4095 CenterZ=0 NormalX=0 NormalY=0 NormalZ=1 AngleXU=0 Radius=1
    g357: BSplineCurve PolesCount=3 KnotsCount=2 Degree=2 IsPeriodic=0
    g358: GeomPoint X=46.0728 Y=72.4095 Z=0
    g359: GeomPoint X=42.0728 Y=76.4095 Z=0
    g360: Circle CenterX=-6.92719 CenterY=76.4095 CenterZ=0 NormalX=0 NormalY=0 NormalZ=1 AngleXU=0 Radius=1
    g361: Circle CenterX=-10.9272 CenterY=76.4095 CenterZ=0 NormalX=0 NormalY=0 NormalZ=1 AngleXU=0 Radius=1
    g362: Circle CenterX=-10.9272 CenterY=72.4095 CenterZ=0 NormalX=0 NormalY=0 NormalZ=1 AngleXU=0 Radius=1
    g363: BSplineCurve PolesCount=3 KnotsCount=2 Degree=2 IsPeriodic=0
    g364: GeomPoint X=-6.92719 Y=76.4095 Z=0
    g365: GeomPoint X=-10.9272 Y=72.4095 Z=0
    g366: LineSegment StartX=-10.9272 StartY=72.4095 StartZ=0 EndX=-10.9272 EndY=-78.7794 EndZ=0
    g367: LineSegment StartX=-7.42095 StartY=-80.8542 StartZ=0 EndX=42.5666 EndY=-53.4075 EndZ=0
    g368: LineSegment StartX=46.0728 StartY=-47.4823 StartZ=0 EndX=46.0728 EndY=72.4095 EndZ=0
    g369: LineSegment StartX=42.0728 StartY=76.4095 StartZ=0 EndX=-6.92719 EndY=76.4095 EndZ=0
    g370: LineSegment StartX=-42.9272 StartY=136.221 StartZ=0 EndX=407.073 EndY=136.221 EndZ=0
    g371: LineSegment StartX=232.072 StartY=136.221 StartZ=0 EndX=220.072 EndY=136.221 EndZ=0
    g372: LineSegment StartX=232.072 StartY=136.221 StartZ=0 EndX=232.072 EndY=124.221 EndZ=0
    g373: LineSegment StartX=220.072 StartY=136.221 StartZ=0 EndX=220.072 EndY=124.221 EndZ=0
    g374: LineSegment StartX=220.072 StartY=136.221 StartZ=0 EndX=226.072 EndY=136.221 EndZ=0
    g375: LineSegment StartX=220.072 StartY=136.221 StartZ=0 EndX=220.072 EndY=130.221 EndZ=0
    g376: LineSegment StartX=220.072 StartY=124.221 StartZ=0 EndX=226.072 EndY=124.221 EndZ=0
    g377: LineSegment StartX=232.072 StartY=124.221 StartZ=0 EndX=232.072 EndY=127.221 EndZ=0
    g378: LineSegment StartX=232.072 StartY=136.221 StartZ=0 EndX=232.072 EndY=133.221 EndZ=0
    g379-g383: Circle x5 (B-spline internal-alignment scaffolding for g384; pole/knot coordinates omitted)
    g384: BSplineCurve PolesCount=5 KnotsCount=3 Degree=3 IsPeriodic=0
    g385: GeomPoint X=232.072 Y=133.221 Z=0
    g386: GeomPoint X=223.072 Y=130.221 Z=0
    g387: GeomPoint X=232.072 Y=127.221 Z=0
    g388: LineSegment StartX=189.124 StartY=124.221 StartZ=0 EndX=302.073 EndY=124.221 EndZ=0
    g389: LineSegment StartX=132.072 StartY=136.221 StartZ=0 EndX=132.072 EndY=124.221 EndZ=0
    g390: LineSegment StartX=132.072 StartY=136.221 StartZ=0 EndX=144.072 EndY=136.221 EndZ=0
    g391: LineSegment StartX=144.072 StartY=136.221 StartZ=0 EndX=144.072 EndY=124.221 EndZ=0
    g392: LineSegment StartX=144.072 StartY=136.221 StartZ=0 EndX=138.072 EndY=136.221 EndZ=0
    g393: LineSegment StartX=144.072 StartY=136.221 StartZ=0 EndX=144.072 EndY=130.221 EndZ=0
    g394: LineSegment StartX=132.072 StartY=136.221 StartZ=0 EndX=132.072 EndY=133.221 EndZ=0
    g395: LineSegment StartX=132.072 StartY=133.221 StartZ=0 EndX=132.072 EndY=127.221 EndZ=0
    g396-g400: Circle x5 (B-spline internal-alignment scaffolding for g401; pole/knot coordinates omitted)
    g401: BSplineCurve PolesCount=5 KnotsCount=3 Degree=3 IsPeriodic=0
    g402: GeomPoint X=132.072 Y=133.221 Z=0
    g403: GeomPoint X=141.072 Y=130.221 Z=0
    g404: GeomPoint X=132.072 Y=127.221 Z=0
    g405: LineSegment StartX=132.072 StartY=124.221 StartZ=0 EndX=175.022 EndY=124.221 EndZ=0
    g406: LineSegment StartX=62.0728 StartY=124.221 StartZ=0 EndX=132.072 EndY=124.221 EndZ=0
    g407: LineSegment StartX=132.072 StartY=136.221 StartZ=0 EndX=131.457 EndY=138.832 EndZ=0
    ... +61 more geometry lines
  constraints (808):
    c: Vertical(g0)
    c: Vertical(g1)
    c: Block(g1)
    c: Block(g0)
    c: Weight(g4) = 1
    c: Equal(g4,g5)
    c: Equal(g4,g6)
    c: InternalAlignment(g4,g7)
    c: InternalAlignment(g5,g7)
    c: InternalAlignment(g6,g7)
    c: InternalAlignment(g8,g7)
    c: InternalAlignment(g9,g7)
    c: Weight(g10) = 1
    c: Equal(g10,g11)
    c: Equal(g10,g12)
    c: InternalAlignment(g10,g13)
    c: InternalAlignment(g11,g13)
    c: InternalAlignment(g12,g13)
    c: InternalAlignment(g14,g13)
    c: InternalAlignment(g15,g13)
    c: Block(g13)
    c: Block(g7)
    c: Weight(g16) = 1
    c: Equal(g16,g17)
    c: Equal(g16,g18)
    c: InternalAlignment(g16,g19)
    c: InternalAlignment(g17,g19)
    c: InternalAlignment(g18,g19)
    c: InternalAlignment(g20,g19)
    c: InternalAlignment(g21,g19)
    c: Weight(g22) = 1
    c: Equal(g22,g23)
    c: Equal(g22,g24)
    c: InternalAlignment(g22,g25)
    c: InternalAlignment(g23,g25)
    c: InternalAlignment(g24,g25)
    c: InternalAlignment(g26,g25)
    c: InternalAlignment(g27,g25)
    c: Block(g25)
    c: Block(g19)
    c: Weight(g28) = 1
    c: Equal(g28,g29)
    c: Equal(g28,g30)
    c: InternalAlignment(g28,g31)
    c: InternalAlignment(g29,g31)
    c: InternalAlignment(g30,g31)
    c: InternalAlignment(g32,g31)
    c: InternalAlignment(g33,g31)
    c: Weight(g34) = 1
    c: Equal(g34,g35)
    c: Equal(g34,g36)
    c: InternalAlignment(g34,g37)
    c: InternalAlignment(g35,g37)
    c: InternalAlignment(g36,g37)
    c: InternalAlignment(g38,g37)
    c: InternalAlignment(g39,g37)
    c: Block(g31)
    c: Block(g37)
    c: Coincident(g40,g1)
    c: Coincident(g40,g0)
    c: Horizontal(g40)
    c: Distance(g40) = 450
    c: Weight(g41) = 1
    c: Equal(g41,g42)
    c: Equal(g41,g43)
    c: InternalAlignment(g41,g44)
    c: InternalAlignment(g42,g44)
    c: InternalAlignment(g43,g44)
    c: InternalAlignment(g45,g44)
    c: InternalAlignment(g46,g44)
    c: Block(g44)
    c: Weight(g47) = 1
    c: Equal(g47,g48)
    c: Equal(g47,g49)
    c: InternalAlignment(g47,g50)
    c: InternalAlignment(g48,g50)
    c: InternalAlignment(g49,g50)
    c: InternalAlignment(g51,g50)
    c: InternalAlignment(g52,g50)
    c: Block(g50)
    c: Weight(g53) = 1
    c: Equal(g53,g54)
    c: Equal(g53,g55)
    c: InternalAlignment(g53,g56)
    c: InternalAlignment(g54,g56)
    c: InternalAlignment(g55,g56)
    c: InternalAlignment(g57,g56)
    c: InternalAlignment(g58,g56)
    c: Block(g56)
    c: Weight(g59) = 1
    c: Equal(g59,g60)
    c: Equal(g59,g61)
    c: InternalAlignment(g59,g62)
    c: InternalAlignment(g60,g62)
    c: InternalAlignment(g61,g62)
    c: InternalAlignment(g63,g62)
    c: InternalAlignment(g64,g62)
    c: Block(g62)
    c: Weight(g65) = 1
    c: Equal(g65,g66)
    c: Equal(g65,g67)
    c: InternalAlignment(g65,g68)
    c: InternalAlignment(g66,g68)
    c: InternalAlignment(g67,g68)
    c: InternalAlignment(g69,g68)
    c: InternalAlignment(g70,g68)
    c: Weight(g71) = 1
    c: Equal(g71,g72)
    c: Equal(g71,g73)
    c: InternalAlignment(g71,g74)
    c: InternalAlignment(g72,g74)
    c: InternalAlignment(g73,g74)
    c: InternalAlignment(g75,g74)
    c: InternalAlignment(g76,g74)
    c: Block(g68)
    c: Block(g74)
    c: Coincident(g77,g68)
    c: Coincident(g77,g74)
    c: Vertical(g77)
    c: Coincident(g78,g68)
    c: Coincident(g78,g50)
    c: Coincident(g79,g50)
    c: Coincident(g79,g74)
    c: Weight(g80) = 1
    c: Equal(g80,g81)
    c: Equal(g80,g82)
    c: InternalAlignment(g80,g83)
    c: InternalAlignment(g81,g83)
    c: InternalAlignment(g82,g83)
    c: InternalAlignment(g84,g83)
    c: InternalAlignment(g85,g83)
    c: Weight(g86) = 1
    c: Equal(g86,g87)
    c: Equal(g86,g88)
    c: InternalAlignment(g86,g89)
    c: InternalAlignment(g87,g89)
    c: InternalAlignment(g88,g89)
    c: InternalAlignment(g90,g89)
    c: InternalAlignment(g91,g89)
    c: Block(g83)
    c: Block(g89)
    c: Coincident(g92,g83)
    c: Coincident(g92,g89)
    c: Vertical(g92)
    c: Coincident(g93,g83)
    c: Coincident(g93,g44)
    c: Coincident(g94,g44)
    c: Coincident(g94,g89)
    c: Weight(g95) = 1
    c: Equal(g95,g96)
    c: Equal(g95,g97)
    c: InternalAlignment(g95,g98)
    c: InternalAlignment(g96,g98)
    c: InternalAlignment(g97,g98)
    c: InternalAlignment(g99,g98)
    c: InternalAlignment(g100,g98)
    c: Weight(g101) = 1
    c: Equal(g101,g102)
    c: Equal(g101,g103)
    c: InternalAlignment(g101,g104)
    c: InternalAlignment(g102,g104)
    c: InternalAlignment(g103,g104)
    c: InternalAlignment(g105,g104)
    c: InternalAlignment(g106,g104)
    c: Block(g98)
    c: Block(g104)
    c: Coincident(g107,g98)
    c: Coincident(g107,g104)
    c: Vertical(g107)
    c: Coincident(g108,g104)
    c: Coincident(g108,g62)
    c: Coincident(g109,g62)
    c: Coincident(g109,g98)
    c: Weight(g110) = 1
    c: Equal(g110,g111)
    c: Equal(g110,g112)
    c: InternalAlignment(g110,g113)
    c: InternalAlignment(g111,g113)
    c: InternalAlignment(g112,g113)
    c: InternalAlignment(g114,g113)
    c: InternalAlignment(g115,g113)
    c: Weight(g116) = 1
    c: Equal(g116,g117)
    c: Equal(g116,g118)
    c: InternalAlignment(g116,g119)
    c: InternalAlignment(g117,g119)
    c: InternalAlignment(g118,g119)
    c: InternalAlignment(g120,g119)
    c: InternalAlignment(g121,g119)
    c: Block(g113)
    c: Block(g119)
    c: Coincident(g122,g113)
    c: Coincident(g122,g119)
    c: Vertical(g122)
    c: Coincident(g123,g119)
    c: Coincident(g123,g56)
    c: Coincident(g124,g56)
    c: Coincident(g124,g113)
    c: Weight(g125) = 1
    c: Equal(g125,g126)
    c: Equal(g125,g127)
    c: InternalAlignment(g125,g128)
    c: InternalAlignment(g126,g128)
    c: InternalAlignment(g127,g128)
    c: InternalAlignment(g129,g128)
    c: InternalAlignment(g130,g128)
    c: Weight(g131) = 1
    c: Equal(g131,g132)
    c: Equal(g131,g133)
    c: InternalAlignment(g131,g134)
    c: InternalAlignment(g132,g134)
    c: InternalAlignment(g133,g134)
    c: InternalAlignment(g135,g134)
    c: InternalAlignment(g136,g134)
    c: Weight(g137) = 1
    c: Equal(g137,g138)
    c: Equal(g137,g139)
    c: InternalAlignment(g137,g140)
    c: InternalAlignment(g138,g140)
    c: InternalAlignment(g139,g140)
    c: InternalAlignment(g141,g140)
    c: InternalAlignment(g142,g140)
    c: Weight(g143) = 1
    c: Equal(g143,g144)
    c: Equal(g143,g145)
    c: InternalAlignment(g143,g146)
    c: InternalAlignment(g144,g146)
    c: InternalAlignment(g145,g146)
    c: InternalAlignment(g147,g146)
    c: InternalAlignment(g148,g146)
    c: Block(g146)
    c: Block(g140)
    c: Block(g134)
    c: Block(g128)
    c: Coincident(g149,g25)
    c: Coincident(g149,g146)
    c: Coincident(g150,g146)
    c: Coincident(g150,g140)
    c: Horizontal(g150)
    c: Coincident(g151,g140)
    c: Coincident(g151,g25)
    c: Vertical(g151)
    c: Coincident(g152,g19)
    c: Coincident(g152,g134)
    c: Vertical(g152)
    c: Coincident(g153,g134)
    c: Coincident(g153,g128)
    c: Horizontal(g153)
    c: Coincident(g154,g128)
    c: Coincident(g154,g19)
    c: Weight(g155) = 1
    c: Equal(g155,g156)
    c: Equal(g155,g157)
    c: InternalAlignment(g155,g158)
    c: InternalAlignment(g156,g158)
    c: InternalAlignment(g157,g158)
    c: InternalAlignment(g159,g158)
    c: InternalAlignment(g160,g158)
    c: Weight(g161) = 1
    c: Equal(g161,g162)
    c: Equal(g161,g163)
    c: InternalAlignment(g161,g164)
    c: InternalAlignment(g162,g164)
    c: InternalAlignment(g163,g164)
    c: InternalAlignment(g165,g164)
    c: InternalAlignment(g166,g164)
    c: Weight(g167) = 1
    c: Equal(g167,g168)
    c: Equal(g167,g169)
    c: InternalAlignment(g167,g170)
    c: InternalAlignment(g168,g170)
    c: InternalAlignment(g169,g170)
    c: InternalAlignment(g171,g170)
    c: InternalAlignment(g172,g170)
    c: Weight(g173) = 1
    c: Equal(g173,g174)
    c: Equal(g173,g175)
    c: InternalAlignment(g173,g176)
    c: InternalAlignment(g174,g176)
    c: InternalAlignment(g175,g176)
    c: InternalAlignment(g177,g176)
    c: InternalAlignment(g178,g176)
    c: Block(g176)
    c: Block(g170)
    c: Block(g164)
    c: Block(g158)
    c: Coincident(g179,g170)
    c: Coincident(g179,g7)
    c: Vertical(g179)
    c: Coincident(g180,g13)
    c: Coincident(g180,g164)
    c: Vertical(g180)
    c: Coincident(g181,g158)
    c: Coincident(g181,g13)
    c: Coincident(g182,g7)
    c: Weight(g183) = 1
    c: Equal(g183,g184)
    c: Equal(g183,g185)
    c: InternalAlignment(g183,g186)
    c: InternalAlignment(g184,g186)
    c: InternalAlignment(g185,g186)
    c: InternalAlignment(g187,g186)
    c: InternalAlignment(g188,g186)
    c: Weight(g189) = 1
    c: Equal(g189,g190)
    c: Equal(g189,g191)
    c: InternalAlignment(g189,g192)
    c: InternalAlignment(g190,g192)
    c: InternalAlignment(g191,g192)
    c: InternalAlignment(g193,g192)
    c: InternalAlignment(g194,g192)
    c: Block(g192)
    c: Block(g186)
    c: Coincident(g195,g192)
    c: Coincident(g195,g31)
    c: Coincident(g196,g31)
    c: Coincident(g196,g186)
    c: Coincident(g197,g186)
    c: Coincident(g197,g192)
    c: Vertical(g197)
    c: Weight(g198) = 1
    c: Equal(g198,g199)
    c: Equal(g198,g200)
    c: InternalAlignment(g198,g201)
    c: InternalAlignment(g199,g201)
    c: InternalAlignment(g200,g201)
    c: InternalAlignment(g202,g201)
    c: InternalAlignment(g203,g201)
    c: Weight(g204) = 1
    c: Equal(g204,g205)
    c: Equal(g204,g206)
    c: InternalAlignment(g204,g207)
    c: InternalAlignment(g205,g207)
    c: InternalAlignment(g206,g207)
    c: InternalAlignment(g208,g207)
    c: InternalAlignment(g209,g207)
    c: Block(g207)
    c: Block(g201)
    c: Coincident(g210,g201)
    c: Coincident(g210,g37)
    c: Coincident(g211,g37)
    c: Coincident(g211,g207)
    c: Coincident(g212,g207)
    c: Coincident(g212,g201)
    c: Vertical(g212)
    c: Horizontal(g213)
    c: Block(g213)
    c: Vertical(g214)
    c: Block(g214)
    c: Block(g215)
    c: Weight(g216) = 1
    c: Equal(g216,g217)
    c: Equal(g216,g218)
    c: InternalAlignment(g216,g219)
    c: InternalAlignment(g217,g219)
    c: InternalAlignment(g218,g219)
    c: InternalAlignment(g220,g219)
    c: InternalAlignment(g221,g219)
    c: Weight(g222) = 1
    c: Equal(g222,g223)
    c: Equal(g222,g224)
    c: InternalAlignment(g222,g225)
    c: InternalAlignment(g223,g225)
    c: InternalAlignment(g224,g225)
    c: InternalAlignment(g226,g225)
    c: InternalAlignment(g227,g225)
    c: Weight(g228) = 1
    c: Equal(g228,g229)
    c: Equal(g228,g230)
    c: InternalAlignment(g228,g231)
    c: InternalAlignment(g229,g231)
    c: InternalAlignment(g230,g231)
    c: InternalAlignment(g232,g231)
    c: InternalAlignment(g233,g231)
    c: Weight(g234) = 1
    c: Equal(g234,g235)
    c: Equal(g234,g236)
    c: InternalAlignment(g234,g237)
    c: InternalAlignment(g235,g237)
    c: InternalAlignment(g236,g237)
    c: InternalAlignment(g238,g237)
    c: InternalAlignment(g239,g237)
    c: Block(g219)
    c: Block(g225)
    c: Block(g231)
    c: Block(g237)
    c: Coincident(g240,g225)
    c: Coincident(g240,g219)
    c: Horizontal(g240)
    c: Block(g182)
    c: Weight(g241) = 1
    c: Equal(g241,g242)
    c: Equal(g241,g243)
    c: InternalAlignment(g241,g244)
    c: InternalAlignment(g242,g244)
    c: InternalAlignment(g243,g244)
    c: InternalAlignment(g245,g244)
    c: InternalAlignment(g246,g244)
    c: Weight(g247) = 1
    c: Equal(g247,g248)
    c: Equal(g247,g249)
    c: InternalAlignment(g247,g250)
    c: InternalAlignment(g248,g250)
    c: InternalAlignment(g249,g250)
    c: InternalAlignment(g251,g250)
    c: InternalAlignment(g252,g250)
    c: Block(g244)
    c: Block(g250)
    c: Coincident(g253,g244)
    c: Coincident(g253,g250)
    c: Weight(g254) = 1
    c: Equal(g254,g255)
    c: Equal(g254,g256)
    c: InternalAlignment(g254,g257)
    c: InternalAlignment(g255,g257)
    c: InternalAlignment(g256,g257)
    c: InternalAlignment(g258,g257)
    c: InternalAlignment(g259,g257)
    c: Weight(g260) = 1
    c: Equal(g260,g261)
    c: Equal(g260,g262)
    c: InternalAlignment(g260,g263)
    c: InternalAlignment(g261,g263)
    c: InternalAlignment(g262,g263)
    c: InternalAlignment(g264,g263)
    c: InternalAlignment(g265,g263)
    c: Weight(g266) = 1
    c: Equal(g266,g267)
    c: Equal(g266,g268)
    c: InternalAlignment(g266,g269)
    c: InternalAlignment(g267,g269)
    c: InternalAlignment(g268,g269)
    c: InternalAlignment(g270,g269)
    c: InternalAlignment(g271,g269)
    c: Block(g269)
    c: Block(g263)
    c: Block(g257)
    c: Coincident(g272,g263)
    c: Coincident(g272,g257)
    c: Coincident(g273,g257)
    c: Coincident(g273,g269)
    c: Vertical(g273)
    c: Coincident(g274,g269)
    c: Coincident(g274,g263)
    c: Horizontal(g274)
    c: Weight(g275) = 1
    c: Equal(g275,g276)
    c: InternalAlignment(g275,g277)
    c: InternalAlignment(g276,g277)
    c: InternalAlignment(g278,g277)
    c: InternalAlignment(g279,g277)
    c: Weight(g280) = 1
    c: InternalAlignment(g281,g283)
    c: InternalAlignment(g282,g283)
    c: InternalAlignment(g284,g283)
    c: InternalAlignment(g285,g283)
    c: Weight(g286) = 1
    c: Equal(g286,g287)
    c: Equal(g286,g288)
    c: InternalAlignment(g286,g289)
    c: InternalAlignment(g287,g289)
    c: InternalAlignment(g288,g289)
    c: InternalAlignment(g290,g289)
    c: InternalAlignment(g291,g289)
    c: Equal(g292,g293)
    c: Equal(g292,g294)
    c: InternalAlignment(g292,g295)
    c: InternalAlignment(g293,g295)
    c: InternalAlignment(g294,g295)
    c: InternalAlignment(g296,g295)
    c: InternalAlignment(g297,g295)
    c: Block(g283)
    c: Block(g289)
    c: Block(g295)
    c: Block(g277)
    c: Coincident(g298,g277)
    c: Coincident(g298,g283)
    c: Horizontal(g298)
    c: Coincident(g299,g283)
    c: Coincident(g299,g289)
    c: Vertical(g299)
    c: Coincident(g300,g289)
    c: Coincident(g300,g295)
    c: Horizontal(g300)
    c: Coincident(g301,g295)
    c: Coincident(g301,g277)
    c: Weight(g302) = 1
    c: Equal(g302,g303)
    c: Equal(g302,g304)
    c: InternalAlignment(g302,g305)
    c: InternalAlignment(g303,g305)
    c: InternalAlignment(g304,g305)
    c: InternalAlignment(g306,g305)
    c: InternalAlignment(g307,g305)
    c: Weight(g308) = 1
    c: Equal(g308,g309)
    c: Equal(g308,g310)
    c: InternalAlignment(g308,g311)
    c: InternalAlignment(g309,g311)
    c: InternalAlignment(g310,g311)
    c: InternalAlignment(g312,g311)
    c: Weight(g314) = 1
    c: Equal(g314,g315)
    c: Equal(g314,g316)
    c: InternalAlignment(g314,g317)
    c: InternalAlignment(g315,g317)
    c: InternalAlignment(g316,g317)
    c: InternalAlignment(g318,g317)
    c: InternalAlignment(g319,g317)
    c: Block(g317)
    c: Block(g311)
    c: Block(g305)
    c: Coincident(g320,g317)
    c: Coincident(g320,g311)
    c: Horizontal(g320)
    c: Coincident(g321,g311)
    c: Coincident(g321,g305)
    c: Vertical(g321)
    c: Coincident(g322,g305)
    c: Coincident(g322,g317)
    c: InternalAlignment(g323,g324)
    c: InternalAlignment(g325,g324)
    c: InternalAlignment(g326,g324)
    c: Block(g324)
    c: Equal(g327,g328)
    c: Equal(g327,g329)
    c: InternalAlignment(g327,g330)
    c: InternalAlignment(g328,g330)
    c: InternalAlignment(g329,g330)
    c: InternalAlignment(g331,g330)
    c: InternalAlignment(g332,g330)
    c: Block(g330)
    c: Coincident(g333,g324)
    c: Horizontal(g333)
    c: Block(g333)
    c: Coincident(g334,g324)
    c: Coincident(g334,g250)
    c: Vertical(g334)
    c: Coincident(g335,g330)
    c: Coincident(g335,g244)
    c: Vertical(g335)
    c: Block(g336)
    c: Block(g2)
    c: Distance(g334) = 119.89
    c: Coincident(g337,g336)
    c: Coincident(g337,g2)
    c: Coincident(g338,g2)
    c: Coincident(g338,g336)
    c: Block(g3)
    c: Block(g339)
    c: Coincident(g340,g339)
    c: Coincident(g340,g3)
    c: Coincident(g341,g339)
    c: Coincident(g341,g3)
    c: Block(g341)
    c: Block(g340)
    c: Weight(g342) = 1
    c: Equal(g342,g344)
    c: InternalAlignment(g342,g345)
    c: InternalAlignment(g343,g345)
    c: InternalAlignment(g344,g345)
    c: InternalAlignment(g346,g345)
    c: InternalAlignment(g347,g345)
    c: InternalAlignment(g352,g351)
    c: InternalAlignment(g353,g351)
    c: InternalAlignment(g355,g357)
    c: Horizontal(g369)
    c: Coincident(g370,g0)
    c: Horizontal(g370)
    c: Block(g370)
    c: Distance(g370) = 450
    c: Horizontal(g371)
    c: Distance(g371) = 12
    c: Coincident(g373,g371)
    c: Vertical(g373)
    c: Horizontal(g374)
    c: Vertical(g375)
    c: Distance(g375) = 6
    c: Coincident(g375,g371)
    c: Coincident(g374,g371)
    c: Block(g373)
    c: Coincident(g376,g373)
    c: Horizontal(g376)
    c: Distance(g376) = 6
    c: Vertical(g377)
    c: Distance(g377) = 3
    c: Vertical(g378)
    c: Distance(g378) = 3
    c: Coincident(g372,g377)
    c: Coincident(g384,g378)
    c: Weight(g379) = 1
    c: Equal(g379,g380)
    c: Coincident(g380,g374)
    c: Equal(g379,g381)
    c: Coincident(g381,g375)
    c: Equal(g379,g382)
    c: Coincident(g382,g376)
    c: Equal(g379,g383)
    c: Coincident(g384,g377)
    c: InternalAlignment(g379-g383 -> g384) x5
    c: InternalAlignment(g385,g384)
    c: InternalAlignment(g386,g384)
    c: InternalAlignment(g387,g384)
    c: Coincident(g388,g164)
    c: Coincident(g388,g158)
    c: Coincident(g392,g390)
    c: Vertical(g393)
    c: Distance(g393) = 6
    c: Coincident(g393,g390)
    c: Vertical(g394)
    c: Distance(g394) = 3
    c: Vertical(g395)
    c: Distance(g395) = 6
    c: Coincident(g395,g394)
    c: Coincident(g401,g394)
    c: Weight(g396) = 1
    c: Equal(g396,g397)
    c: Coincident(g397,g392)
    c: Equal(g396,g398)
    c: Coincident(g398,g393)
    c: Equal(g396,g399)
    c: Equal(g396,g400)
    c: Coincident(g401,g395)
    c: InternalAlignment(g396-g400 -> g401) x5
    c: InternalAlignment(g402,g401)
    c: InternalAlignment(g403,g401)
    c: InternalAlignment(g404,g401)
    c: Coincident(g405,g389)
    c: Coincident(g405,g170)
    c: Horizontal(g405)
    c: Block(g401)
    c: Coincident(g406,g176)
    c: Coincident(g406,g389)
    c: Horizontal(g406)
    c: Block(g405)
    c: Coincident(g408,g389)
    c: PointOnObject(g408,g153)
    c: Vertical(g408)
    c: Block(g409)
    c: Coincident(g410,g409)
    c: Vertical(g410)
    c: PointOnObject(g410,g40)
    c: Block(g410)
    c: Coincident(g411,g409)
    c: Vertical(g411)
    c: Block(g411)
    c: Vertical(g412)
    c: Distance(g412) = 3
    c: Equal(g379,g415) = 1
    c: Equal(g415,g416)
    c: InternalAlignment(g415,g417)
    c: InternalAlignment(g416,g417)
    c: InternalAlignment(g413,g417)
    c: InternalAlignment(g414,g417)
    c: InternalAlignment(g418,g417)
    c: Block(g417)
    c: Coincident(g418,g412)
    c: Coincident(g419,g417)
    c: PointOnObject(g419,g150)
    c: Vertical(g419)
    c: Distance(g420) = 3
    c: Block(g420)
    c: Distance(g421) = 3
    c: Parallel(g421,g420)
    c: Coincident(g421,g420)
    c: Coincident(g422,g420)
    c: Perpendicular(g422,g420)
    c: Distance(g422) = 3
    c: Coincident(g423,g421)
    c: Perpendicular(g423,g421)
    c: Distance(g423) = 3
    c: Coincident(g424,g420)
    c: Perpendicular(g424,g421)
    c: Distance(g424) = 6
    c: Coincident(g425,g424)
    c: PointOnObject(g423,g425)
    c: Coincident(g426,g420)
    c: PointOnObject(g426,g79)
    c: Block(g426)
    c: Distance(g427) = 2.76
    c: Coincident(g428,g427)
    c: Parallel(g427,g428)
    c: PointOnObject(g428,g181)
    c: Distance(g428) = 2.41
    c: Block(g428)
    c: Coincident(g429,g427)
    c: Distance(g429) = 6.6
    c: Perpendicular(g429,g428)
    c: Distance(g430) = 6.6
    c: Coincident(g431,g429)
    c: Coincident(g431,g430)
    c: Block(g432)
    c: Coincident(g433,g432)
    c: Vertical(g433)
    c: Distance(g433) = 3.6
    c: Coincident(g434,g427)
    c: Parallel(g427,g434)
    c: PointOnObject(g434,g78)
    c: Block(g434)
    c: Coincident(g435,g421)
    c: Parallel(g435,g421)
    c: PointOnObject(g435,g211)
    c: Block(g435)
    c: Coincident(g436,g435)
    c: Vertical(g436)
    c: PointOnObject(g436,g210)
    c: Coincident(g437,g436)
    c: Perpendicular(g437,g210)
    c: Distance(g437) = 3
    c: Coincident(g438,g437)
    c: Block(g437)
    c: Distance(g438) = 3
    c: Parallel(g437,g438)
    c: Coincident(g439,g438)
    c: Distance(g439) = 3
    c: Parallel(g438,g439)
    c: Coincident(g440,g439)
    c: Parallel(g440,g437)
    c: PointOnObject(g440,g124)
    c: PointOnObject(g441,g53)
    c: Tangent(g440,g441)
    c: Coincident(g442,g439)
    c: Perpendicular(g442,g439)
    c: Coincident(g443,g437)
    c: Parallel(g443,g442)
    c: Distance(g443) = 3
    c: Distance(g442) = 3
    c: PointOnObject(g442,g444)
    c: Block(g444)
    c: PointOnObject(g445,g123)
    c: Perpendicular(g123,g445)
    c: Distance(g445) = 2.41
    c: Block(g445)
    c: Coincident(g446,g445)
    c: Perpendicular(g123,g446)
    c: Distance(g446) = 2.76
    c: Coincident(g447,g446)
    c: Perpendicular(g123,g447)
    c: PointOnObject(g447,g149)
    c: Coincident(g448,g445)
    c: Parallel(g123,g448)
    c: Distance(g448) = 6.6
    c: Coincident(g449,g446)
    c: Parallel(g123,g449)
    c: Coincident(g450,g448)
    c: Distance(g449) = 6.6
    c: Coincident(g449,g450)
    c: Block(g149)
    c: Block(g124)
    c: Block(g211)
    c: Block(g181)
    c: Block(g78)
    c: Block(g79)
    c: Block(g430)
    c: Coincident(g451,g447)
    c: Distance(g451) = 46
    c: Parallel(g149,g451)
    c: Coincident(g452,g451)
    c: Horizontal(g452)
    c: PointOnObject(g452,g154)
    c: Coincident(g453,g451)
    c: Vertical(g453)
    c: Distance(g453) = 9
    c: Block(g452)
    c: PointOnObject(g454,g93)
    c: Distance(g455) = 6.6
    c: Distance(g456) = 6.6
    c: Block(g454)
    c: Coincident(g457,g456)
    c: Coincident(g457,g455)
    c: Perpendicular(g457,g182)
    c: Coincident(g458,g455)
    c: Perpendicular(g458,g182)
    c: PointOnObject(g458,g182)
    c: Block(g458)
    c: Block(g457)
    c: Block(g456)
    c: PointOnObject(g459,g196)
    c: Perpendicular(g196,g459)
    c: Distance(g459) = 3
    c: Coincident(g460,g459)
    c: Perpendicular(g196,g460)
    c: Distance(g460) = 3
    c: Coincident(g461,g460)
    c: Perpendicular(g196,g461)
    c: Distance(g461) = 3
    c: Coincident(g462,g461)
    c: Tangent(g462,g41)
    c: PointOnObject(g462,g94)
    c: Block(g462)
    c: Block(g459)
    c: Coincident(g463,g459)
    c: Parallel(g196,g463)
    c: Distance(g463) = 3
    c: Coincident(g464,g461)
    c: Distance(g464) = 3
    c: Parallel(g196,g464)
    c: Coincident(g465,g460)
    c: Distance(g465) = 6
    c: Parallel(g465,g196)
    c: Coincident(g466,g465)
    c: PointOnObject(g464,g466)
    c: Block(g466)
    c: Coincident(g467,g458)
    c: Vertical(g467)
    c: PointOnObject(g467,g195)
    c: Coincident(g468,g467)
    c: Perpendicular(g195,g468)
FEATURE [Sketcher::SketchObject] Sketch004  label="rightSideBottom"
  FullyConstrained = false
  sketch-geometry (91):
    g0: ArcOfCircle CenterX=391.073 CenterY=-83.7794 CenterZ=0 NormalX=0 NormalY=0 NormalZ=1 AngleXU=0 Radius=8 StartAngle=3.14159 EndAngle=6.28319
    g1: Circle CenterX=306.073 CenterY=-81.8102 CenterZ=0 NormalX=0 NormalY=0 NormalZ=1 AngleXU=0 Radius=1
    g2: Circle CenterX=306.073 CenterY=-77.8102 CenterZ=0 NormalX=0 NormalY=0 NormalZ=1 AngleXU=0 Radius=1
    g3: Circle CenterX=302.567 CenterY=-42.9683 CenterZ=0 NormalX=0 NormalY=0 NormalZ=1 AngleXU=0 Radius=1
    g4: Circle CenterX=306.073 CenterY=-44.8935 CenterZ=0 NormalX=0 NormalY=0 NormalZ=1 AngleXU=0 Radius=1
    g5: Circle CenterX=306.073 CenterY=-40.8935 CenterZ=0 NormalX=0 NormalY=0 NormalZ=1 AngleXU=0 Radius=1
    g6: BSplineCurve PolesCount=3 KnotsCount=2 Degree=2 IsPeriodic=0
    g7: GeomPoint X=302.567 Y=-42.9683 Z=0
    g8: GeomPoint X=306.073 Y=-40.8935 Z=0
    g9: Circle CenterX=371.567 CenterY=-80.8644 CenterZ=0 NormalX=0 NormalY=0 NormalZ=1 AngleXU=0 Radius=1
    g10: Circle CenterX=375.073 CenterY=-82.7896 CenterZ=0 NormalX=0 NormalY=0 NormalZ=1 AngleXU=0 Radius=1
    g11: Circle CenterX=375.073 CenterY=-78.7896 CenterZ=0 NormalX=0 NormalY=0 NormalZ=1 AngleXU=0 Radius=1
    g12: GeomPoint X=371.567 Y=-80.8644 Z=0
    g13: GeomPoint X=375.073 Y=-78.7896 Z=0
    g14: Circle CenterX=318.073 CenterY=-51.4823 CenterZ=0 NormalX=0 NormalY=0 NormalZ=1 AngleXU=0 Radius=1
    g15: Circle CenterX=318.073 CenterY=-47.4805 CenterZ=0 NormalX=0 NormalY=0 NormalZ=1 AngleXU=0 Radius=1
    g16: GeomPoint X=321.579 Y=-53.4075 Z=0
    g17: GeomPoint X=318.073 Y=-47.4805 Z=0
    g18: Circle CenterX=321.579 CenterY=-67.3492 CenterZ=0 NormalX=0 NormalY=0 NormalZ=1 AngleXU=0 Radius=1
    g19: Circle CenterX=318.073 CenterY=-65.424 CenterZ=0 NormalX=0 NormalY=0 NormalZ=1 AngleXU=0 Radius=1
    g20: Circle CenterX=318.073 CenterY=-69.424 CenterZ=0 NormalX=0 NormalY=0 NormalZ=1 AngleXU=0 Radius=1
    g21: GeomPoint X=321.579 Y=-67.3492 Z=0
    g22: GeomPoint X=318.073 Y=-69.424 Z=0
    g23: Circle CenterX=362.567 CenterY=-89.8542 CenterZ=0 NormalX=0 NormalY=0 NormalZ=1 AngleXU=0 Radius=1
    g24: Circle CenterX=366.073 CenterY=-91.7794 CenterZ=0 NormalX=0 NormalY=0 NormalZ=1 AngleXU=0 Radius=1
    g25: Circle CenterX=362.073 CenterY=-91.7794 CenterZ=0 NormalX=0 NormalY=0 NormalZ=1 AngleXU=0 Radius=1
    g26: GeomPoint X=362.567 Y=-89.8542 Z=0
    g27: GeomPoint X=362.073 Y=-91.7794 Z=0
    g28: Circle CenterX=322.073 CenterY=-91.7794 CenterZ=0 NormalX=0 NormalY=0 NormalZ=1 AngleXU=0 Radius=1
    g29: Circle CenterX=318.073 CenterY=-91.7794 CenterZ=0 NormalX=0 NormalY=0 NormalZ=1 AngleXU=0 Radius=1
    g30: Circle CenterX=318.073 CenterY=-87.7794 CenterZ=0 NormalX=0 NormalY=0 NormalZ=1 AngleXU=0 Radius=1
    g31: GeomPoint X=322.073 Y=-91.7794 Z=0
    g32: GeomPoint X=318.073 Y=-87.7794 Z=0
    g33: ArcOfCircle CenterX=391.073 CenterY=22.1087 CenterZ=0 NormalX=0 NormalY=0 NormalZ=1 AngleXU=0 Radius=4 StartAngle=0 EndAngle=3.14159
    g34: LineSegment StartX=387.073 StartY=22.1087 StartZ=0 EndX=383.073 EndY=-83.7794 EndZ=0
    g35: LineSegment StartX=395.073 StartY=22.1087 StartZ=0 EndX=399.073 EndY=-83.7794 EndZ=0
    g36: LineSegment StartX=232.072 StartY=-103.779 StartZ=0 EndX=232.072 EndY=-100.779 EndZ=0
    g37: GeomPoint X=232.072 Y=-94.7794 Z=0
    g38: GeomPoint X=223.072 Y=-97.7794 Z=0
    g39: Circle CenterX=232.072 CenterY=-94.7794 CenterZ=0 NormalX=0 NormalY=0 NormalZ=1 AngleXU=0 Radius=1
    g40: Circle CenterX=232.072 CenterY=-100.779 CenterZ=0 NormalX=0 NormalY=0 NormalZ=1 AngleXU=0 Radius=1
    g41: BSplineCurve PolesCount=5 KnotsCount=3 Degree=3 IsPeriodic=0
    g42: GeomPoint X=232.072 Y=-100.779 Z=0
    g43: LineSegment StartX=232.072 StartY=-94.7794 StartZ=0 EndX=232.072 EndY=-91.7794 EndZ=0
    g44: LineSegment StartX=245.072 StartY=-31.3037 StartZ=0 EndX=243.535 EndY=-33.1602 EndZ=0
    g45: LineSegment StartX=241.775 StartY=-35.2862 StartZ=0 EndX=240.266 EndY=-37.1092 EndZ=0
    g46: LineSegment StartX=243.535 StartY=-33.1602 StartZ=0 EndX=248.619 EndY=-37.3688 EndZ=0
    g47: LineSegment StartX=241.775 StartY=-35.2862 StartZ=0 EndX=246.859 EndY=-39.4949 EndZ=0
    g48: LineSegment StartX=248.619 StartY=-37.3688 StartZ=0 EndX=246.859 EndY=-39.4949 EndZ=0
    g49: LineSegment StartX=232.072 StartY=-103.779 StartZ=0 EndX=407.073 EndY=-103.779 EndZ=0
    g50: LineSegment StartX=299.888 StartY=-86.6413 StartZ=0 EndX=240.266 EndY=-37.1092 EndZ=0
    g51: LineSegment StartX=245.072 StartY=-11.4025 StartZ=0 EndX=302.567 EndY=-42.9683 EndZ=0
    g52: BSplineCurve PolesCount=3 KnotsCount=2 Degree=2 IsPeriodic=0
    g53: BSplineCurve PolesCount=3 KnotsCount=2 Degree=2 IsPeriodic=0
    g54: LineSegment StartX=321.579 StartY=-53.4075 StartZ=0 EndX=371.567 EndY=-80.8644 EndZ=0
    g55: BSplineCurve PolesCount=3 KnotsCount=2 Degree=2 IsPeriodic=0
    g56: BSplineCurve PolesCount=3 KnotsCount=2 Degree=2 IsPeriodic=0
    g57: BSplineCurve PolesCount=3 KnotsCount=2 Degree=2 IsPeriodic=0
    g58: LineSegment StartX=318.073 StartY=-69.424 StartZ=0 EndX=318.073 EndY=-87.7794 EndZ=0
    g59: LineSegment StartX=321.579 StartY=-67.3492 StartZ=0 EndX=362.567 EndY=-89.8542 EndZ=0
    g60: LineSegment StartX=362.073 StartY=-91.7794 StartZ=0 EndX=322.073 EndY=-91.7794 EndZ=0
    g61: BSplineCurve PolesCount=3 KnotsCount=2 Degree=2 IsPeriodic=0
    g62: BSplineCurve PolesCount=3 KnotsCount=2 Degree=2 IsPeriodic=0
    g63: LineSegment StartX=245.072 StartY=-31.3037 StartZ=0 EndX=302.996 EndY=-79.2541 EndZ=0
    g64: LineSegment StartX=302.567 StartY=-56.9099 StartZ=0 EndX=239.193 EndY=-22.1109 EndZ=0
    g65: LineSegment StartX=306.073 StartY=-62.8351 StartZ=0 EndX=306.073 EndY=-77.8102 EndZ=0
    g66: BSplineCurve PolesCount=3 KnotsCount=2 Degree=2 IsPeriodic=0
    g67: LineSegment StartX=298.776 StartY=-91.7794 StartZ=0 EndX=232.072 EndY=-91.7794 EndZ=0
    g68: LineSegment StartX=245.072 StartY=-11.4025 StartZ=0 EndX=243.628 EndY=-14.0323 EndZ=0
    g69: LineSegment StartX=240.741 StartY=-19.2917 StartZ=0 EndX=239.193 EndY=-22.1109 EndZ=0
    g70: LineSegment StartX=243.628 StartY=-14.0323 StartZ=0 EndX=246.258 EndY=-15.476 EndZ=0
    g71: LineSegment StartX=240.741 StartY=-19.2917 StartZ=0 EndX=243.37 EndY=-20.7355 EndZ=0
    g72: ArcOfCircle CenterX=247.444 CenterY=-19.5495 CenterZ=0 NormalX=0 NormalY=0 NormalZ=1 AngleXU=0 Radius=4.24264 StartAngle=3.4249 EndAngle=8.13729
    g73: LineSegment StartX=407.073 StartY=-103.779 StartZ=0 EndX=407.073 EndY=48.2206 EndZ=0
    g74: LineSegment StartX=375.073 StartY=48.2206 StartZ=0 EndX=375.073 EndY=-78.7896 EndZ=0
    g75: LineSegment StartX=375.073 StartY=48.2206 StartZ=0 EndX=382.073 EndY=48.2206 EndZ=0
    g76: LineSegment StartX=407.073 StartY=48.2206 StartZ=0 EndX=400.073 EndY=48.2206 EndZ=0
    g77: LineSegment StartX=394.073 StartY=48.2206 StartZ=0 EndX=394.073 EndY=52.2206 EndZ=0
    g78: LineSegment StartX=388.073 StartY=48.2206 StartZ=0 EndX=388.073 EndY=58.2206 EndZ=0
    g79: ArcOfCircle CenterX=385.073 CenterY=61.2206 CenterZ=0 NormalX=0 NormalY=0 NormalZ=1 AngleXU=0 Radius=4.24264 StartAngle=5.49779 EndAngle=10.2102
    g80: ArcOfCircle CenterX=397.073 CenterY=55.2206 CenterZ=0 NormalX=0 NormalY=0 NormalZ=1 AngleXU=0 Radius=4.24264 StartAngle=5.49779 EndAngle=10.2102
    g81: LineSegment StartX=382.073 StartY=58.2206 StartZ=0 EndX=382.073 EndY=48.2206 EndZ=0
    g82: LineSegment StartX=400.073 StartY=52.2206 StartZ=0 EndX=400.073 EndY=48.2206 EndZ=0
    g83: LineSegment StartX=394.073 StartY=48.2206 StartZ=0 EndX=388.073 EndY=48.2206 EndZ=0
    g84: LineSegment StartX=306.073 StartY=-40.8935 StartZ=0 EndX=306.073 EndY=-27.5935 EndZ=0
    g85: LineSegment StartX=318.073 StartY=-27.5935 StartZ=0 EndX=318.073 EndY=-47.4805 EndZ=0
    g86: LineSegment StartX=306.073 StartY=-27.5935 StartZ=0 EndX=310.073 EndY=-27.5935 EndZ=0
    g87: LineSegment StartX=318.073 StartY=-27.5935 StartZ=0 EndX=314.073 EndY=-27.5935 EndZ=0
    g88: LineSegment StartX=310.073 StartY=-27.5935 StartZ=0 EndX=310.073 EndY=-31.5935 EndZ=0
    g89: LineSegment StartX=314.073 StartY=-27.5935 StartZ=0 EndX=314.073 EndY=-31.5935 EndZ=0
    g90: ArcOfCircle CenterX=312.073 CenterY=-33.5935 CenterZ=0 NormalX=0 NormalY=0 NormalZ=1 AngleXU=0 Radius=2.82843 StartAngle=2.35619 EndAngle=7.06858
  constraints (121):
    c: Distance(g44) = 2.41
    c: Block(g44)
    c: Coincident(g46,g44)
    c: Coincident(g49,g36)
    c: Horizontal(g49)
    c: Block(g49)
    c: Coincident(g50,g45)
    c: Block(g50)
    c: Coincident(g51,g6)
    c: Block(g51)
    c: Coincident(g54,g52)
    c: Coincident(g54,g53)
    c: Coincident(g58,g56)
    c: Coincident(g58,g57)
    c: Vertical(g58)
    c: Coincident(g59,g56)
    c: Coincident(g59,g55)
    c: Coincident(g60,g55)
    c: Coincident(g60,g57)
    c: Horizontal(g60)
    c: Block(g61)
    c: Block(g62)
    c: Coincident(g63,g44)
    c: Coincident(g63,g62)
    c: Coincident(g64,g61)
    c: Coincident(g65,g61)
    c: Coincident(g65,g62)
    c: Vertical(g65)
    c: Block(g66)
    c: Coincident(g66,g50)
    c: Coincident(g67,g66)
    c: Coincident(g67,g43)
    c: Horizontal(g67)
    c: Coincident(g68,g51)
    c: Perpendicular(g68,g51)
    c: Coincident(g69,g64)
    c: Coincident(g70,g68)
    c: Distance(g70) = 3
    c: Distance(g71) = 3
    c: Perpendicular(g68,g70)
    c: Coincident(g72,g70)
    c: Coincident(g72,g71)
    c: Block(g72)
    c: Block(g69)
    c: Block(g71)
    c: Block(g54)
    c: Block(g59)
    c: Block(g58)
    c: Block(g60)
    c: Block(g67)
    c: Block(g43)
    c: Block(g36)
    c: Block(g48)
    c: Block(g46)
    c: Block(g47)
    c: Block(g45)
    c: Block(g35)
    c: Block(g34)
    c: Block(g0)
    c: Block(g33)
    c: Block(g52)
    c: Block(g6)
    c: Block(g41)
    c: Block(g57)
    c: Block(g55)
    c: Block(g53)
    c: Block(g68)
    c: Distance(g48) = 2.76
    c: Distance(g47) = 6.6
    c: Distance(g45) = 2.36657
    c: Coincident(g73,g49)
    c: Vertical(g73)
    c: Distance(g73) = 152
    c: Coincident(g74,g53)
    c: Vertical(g74)
    c: Block(g74)
    c: Coincident(g75,g74)
    c: Horizontal(g75)
    c: Distance(g75) = 7
    c: Horizontal(g76)
    c: Distance(g76) = 7
    c: Coincident(g76,g73)
    c: Vertical(g77)
    c: Distance(g77) = 4
    c: Vertical(g78)
    c: Distance(g78) = 10
    c: Coincident(g79,g78)
    c: Coincident(g80,g77)
    c: Block(g80)
    c: Block(g79)
    c: Coincident(g81,g79)
    c: Coincident(g81,g75)
    c: Vertical(g81)
    c: Coincident(g82,g80)
    c: Coincident(g82,g76)
    c: Vertical(g82)
    c: Coincident(g83,g77)
    c: Coincident(g83,g78)
    c: Horizontal(g83)
    c: Coincident(g84,g6)
    c: Vertical(g84)
    c: Distance(g84) = 13.3
    c: Coincident(g85,g52)
    c: Vertical(g85)
    c: Block(g85)
    c: Coincident(g86,g84)
    c: Horizontal(g86)
    c: Distance(g86) = 4
    c: Coincident(g87,g85)
    c: Horizontal(g87)
    c: Distance(g87) = 4
    c: Coincident(g88,g86)
    c: Vertical(g88)
    c: Coincident(g89,g87)
    c: Vertical(g89)
    c: Distance(g88) = 4
    c: Distance(g89) = 4
    c: Coincident(g90,g88)
    c: Coincident(g90,g89)
    c: Block(g90)
    c: Block(g56)
FEATURE [Sketcher::SketchObject] Sketch005  label="middleTop"
  FullyConstrained = true
  sketch-geometry (133):
    g0: Circle CenterX=175.025 CenterY=27.0667 CenterZ=0 NormalX=0 NormalY=0 NormalZ=1 AngleXU=0 Radius=1
    g1: Circle CenterX=179.022 CenterY=24.8665 CenterZ=0 NormalX=0 NormalY=0 NormalZ=1 AngleXU=0 Radius=1
    g2: Circle CenterX=179.022 CenterY=27.0606 CenterZ=0 NormalX=0 NormalY=0 NormalZ=1 AngleXU=0 Radius=1
    g3: BSplineCurve PolesCount=3 KnotsCount=2 Degree=2 IsPeriodic=0
    g4: GeomPoint X=175.025 Y=27.0667 Z=0
    g5: GeomPoint X=179.022 Y=27.0606 Z=0
    g6: Circle CenterX=189.124 CenterY=27.0628 CenterZ=0 NormalX=0 NormalY=0 NormalZ=1 AngleXU=0 Radius=1
    g7: Circle CenterX=185.124 CenterY=24.8665 CenterZ=0 NormalX=0 NormalY=0 NormalZ=1 AngleXU=0 Radius=1
    g8: Circle CenterX=185.124 CenterY=27.0606 CenterZ=0 NormalX=0 NormalY=0 NormalZ=1 AngleXU=0 Radius=1
    g9: BSplineCurve PolesCount=3 KnotsCount=2 Degree=2 IsPeriodic=0
    g10: GeomPoint X=189.124 Y=27.0628 Z=0
    g11: GeomPoint X=185.124 Y=27.0606 Z=0
    g12: Circle CenterX=165.871 CenterY=18.1458 CenterZ=0 NormalX=0 NormalY=0 NormalZ=1 AngleXU=0 Radius=1
    g13: Circle CenterX=169.377 CenterY=16.2206 CenterZ=0 NormalX=0 NormalY=0 NormalZ=1 AngleXU=0 Radius=1
    g14: Circle CenterX=165.871 CenterY=14.2956 CenterZ=0 NormalX=0 NormalY=0 NormalZ=1 AngleXU=0 Radius=1
    g15: BSplineCurve PolesCount=3 KnotsCount=2 Degree=2 IsPeriodic=0
    g16: GeomPoint X=165.871 Y=18.1458 Z=0
    g17: GeomPoint X=165.871 Y=14.2956 Z=0
    g18: Circle CenterX=198.275 CenterY=18.1318 CenterZ=0 NormalX=0 NormalY=0 NormalZ=1 AngleXU=0 Radius=1
    g19: Circle CenterX=194.768 CenterY=16.2206 CenterZ=0 NormalX=0 NormalY=0 NormalZ=1 AngleXU=0 Radius=1
    g20: Circle CenterX=198.264 CenterY=14.2963 CenterZ=0 NormalX=0 NormalY=0 NormalZ=1 AngleXU=0 Radius=1
    g21: BSplineCurve PolesCount=3 KnotsCount=2 Degree=2 IsPeriodic=0
    g22: GeomPoint X=198.275 Y=18.1318 Z=0
    g23: GeomPoint X=198.264 Y=14.2963 Z=0
    g24: Circle CenterX=125.607 CenterY=54.1951 CenterZ=0 NormalX=0 NormalY=0 NormalZ=1 AngleXU=0 Radius=1
    g25: Circle CenterX=139.632 CenterY=46.4944 CenterZ=0 NormalX=0 NormalY=0 NormalZ=1 AngleXU=0 Radius=1
    g26: Circle CenterX=127.326 CenterY=56.7187 CenterZ=0 NormalX=0 NormalY=0 NormalZ=1 AngleXU=0 Radius=1
    g27: BSplineCurve PolesCount=3 KnotsCount=2 Degree=2 IsPeriodic=0
    g28: GeomPoint X=125.607 Y=54.1951 Z=0
    g29: GeomPoint X=127.326 Y=56.7187 Z=0
    g30: Circle CenterX=236.824 CenterY=56.7187 CenterZ=0 NormalX=0 NormalY=0 NormalZ=1 AngleXU=0 Radius=1
    g31: Circle CenterX=224.513 CenterY=46.4944 CenterZ=0 NormalX=0 NormalY=0 NormalZ=1 AngleXU=0 Radius=1
    g32: Circle CenterX=238.538 CenterY=54.1951 CenterZ=0 NormalX=0 NormalY=0 NormalZ=1 AngleXU=0 Radius=1
    g33: BSplineCurve PolesCount=3 KnotsCount=2 Degree=2 IsPeriodic=0
    g34: GeomPoint X=236.824 Y=56.7187 Z=0
    g35: GeomPoint X=238.538 Y=54.1951 Z=0
    g36: Circle CenterX=189.121 CenterY=124.221 CenterZ=0 NormalX=0 NormalY=0 NormalZ=1 AngleXU=0 Radius=1
    g37: Circle CenterX=185.124 CenterY=124.221 CenterZ=0 NormalX=0 NormalY=0 NormalZ=1 AngleXU=0 Radius=1
    g38: Circle CenterX=185.124 CenterY=120.221 CenterZ=0 NormalX=0 NormalY=0 NormalZ=1 AngleXU=0 Radius=1
    g39: BSplineCurve PolesCount=3 KnotsCount=2 Degree=2 IsPeriodic=0
    g40: GeomPoint X=189.121 Y=124.221 Z=0
    g41: GeomPoint X=185.124 Y=120.221 Z=0
    g42: Circle CenterX=175.022 CenterY=124.221 CenterZ=0 NormalX=0 NormalY=0 NormalZ=1 AngleXU=0 Radius=1
    g43: Circle CenterX=179.022 CenterY=124.221 CenterZ=0 NormalX=0 NormalY=0 NormalZ=1 AngleXU=0 Radius=1
    g44: Circle CenterX=179.022 CenterY=120.221 CenterZ=0 NormalX=0 NormalY=0 NormalZ=1 AngleXU=0 Radius=1
    g45: BSplineCurve PolesCount=3 KnotsCount=2 Degree=2 IsPeriodic=0
    g46: GeomPoint X=175.022 Y=124.221 Z=0
    g47: GeomPoint X=179.022 Y=120.221 Z=0
    g48: LineSegment StartX=232.071 StartY=124.221 StartZ=0 EndX=232.071 EndY=127.221 EndZ=0
    g49-g52: Circle x4 (B-spline internal-alignment scaffolding for g53; pole/knot coordinates omitted)
    g53: BSplineCurve PolesCount=5 KnotsCount=3 Degree=3 IsPeriodic=0
    g54: GeomPoint X=232.072 Y=133.221 Z=0
    g55: GeomPoint X=223.072 Y=130.221 Z=0
    g56: GeomPoint X=232.071 Y=127.221 Z=0
    g57-g61: Circle x5 (B-spline internal-alignment scaffolding for g62; pole/knot coordinates omitted)
    g62: BSplineCurve PolesCount=5 KnotsCount=3 Degree=3 IsPeriodic=0
    g63: GeomPoint X=132.072 Y=133.221 Z=0
    g64: GeomPoint X=141.072 Y=130.221 Z=0
    g65: GeomPoint X=132.072 Y=127.221 Z=0
    g66: ArcOfCircle CenterX=247.391 CenterY=52.0843 CenterZ=0 NormalX=0 NormalY=0 NormalZ=1 AngleXU=0 Radius=4.24264 StartAngle=4.42912 EndAngle=9.14151
    g67: LineSegment StartX=240.687 StartY=51.8263 StartZ=0 EndX=239.192 EndY=54.5542 EndZ=0
    g68: LineSegment StartX=243.575 StartY=46.5669 StartZ=0 EndX=245.072 EndY=43.8408 EndZ=0
    g69: LineSegment StartX=240.168 StartY=69.471 StartZ=0 EndX=241.708 EndY=67.6172 EndZ=0
    g70: LineSegment StartX=246.783 StartY=71.8328 StartZ=0 EndX=248.546 EndY=69.7098 EndZ=0
    g71: LineSegment StartX=245.073 StartY=63.5726 StartZ=0 EndX=243.476 EndY=65.4955 EndZ=0
    g72: LineSegment StartX=123.967 StartY=69.4706 StartZ=0 EndX=122.37 EndY=67.5474 EndZ=0
    g73: LineSegment StartX=232.072 StartY=133.221 StartZ=0 EndX=232.072 EndY=136.221 EndZ=0
    g74: LineSegment StartX=232.072 StartY=136.221 StartZ=0 EndX=132.072 EndY=136.221 EndZ=0
    g75: LineSegment StartX=132.072 StartY=136.221 StartZ=0 EndX=132.072 EndY=133.221 EndZ=0
    g76: LineSegment StartX=132.072 StartY=127.221 StartZ=0 EndX=132.072 EndY=124.221 EndZ=0
    g77: LineSegment StartX=132.072 StartY=124.221 StartZ=0 EndX=175.022 EndY=124.221 EndZ=0
    g78: LineSegment StartX=189.121 StartY=124.221 StartZ=0 EndX=232.071 EndY=124.221 EndZ=0
    g79: LineSegment StartX=185.124 StartY=120.221 StartZ=0 EndX=185.124 EndY=27.0606 EndZ=0
    g80: LineSegment StartX=189.124 StartY=27.0628 StartZ=0 EndX=240.168 EndY=69.471 EndZ=0
    g81: LineSegment StartX=241.708 StartY=67.6172 StartZ=0 EndX=246.783 EndY=71.8328 EndZ=0
    g82: LineSegment StartX=248.546 StartY=69.7098 StartZ=0 EndX=243.476 EndY=65.4955 EndZ=0
    g83: LineSegment StartX=245.073 StartY=63.5726 StartZ=0 EndX=236.824 EndY=56.7187 EndZ=0
    g84: LineSegment StartX=238.538 StartY=54.1951 StartZ=0 EndX=239.192 EndY=54.5542 EndZ=0
    g85: LineSegment StartX=240.687 StartY=51.8263 StartZ=0 EndX=243.317 EndY=53.2701 EndZ=0
    g86: LineSegment StartX=246.205 StartY=48.0108 StartZ=0 EndX=243.575 EndY=46.5669 EndZ=0
    g87: LineSegment StartX=245.072 StartY=43.8408 StartZ=0 EndX=198.275 EndY=18.1318 EndZ=0
    g88: LineSegment StartX=165.871 StartY=18.1458 StartZ=0 EndX=118.934 EndY=43.9178 EndZ=0
    g89: LineSegment StartX=118.934 StartY=43.9178 StartZ=0 EndX=120.377 EndY=46.5474 EndZ=0
    g90: LineSegment StartX=117.748 StartY=47.9913 StartZ=0 EndX=120.377 EndY=46.5474 EndZ=0
    g91: LineSegment StartX=120.635 StartY=53.2507 StartZ=0 EndX=123.265 EndY=51.8068 EndZ=0
    g92: LineSegment StartX=123.265 StartY=51.8068 StartZ=0 EndX=124.73 EndY=54.6766 EndZ=0
    g93: ArcOfCircle CenterX=116.562 CenterY=52.0649 CenterZ=0 NormalX=0 NormalY=0 NormalZ=1 AngleXU=0 Radius=4.24264 StartAngle=0.283267 EndAngle=4.99566
    g94: LineSegment StartX=124.73 StartY=54.6766 StartZ=0 EndX=125.607 EndY=54.1951 EndZ=0
    g95: LineSegment StartX=127.326 StartY=56.7187 StartZ=0 EndX=119.072 EndY=63.5741 EndZ=0
    g96: LineSegment StartX=119.072 StartY=63.5741 StartZ=0 EndX=120.669 EndY=65.4973 EndZ=0
    g97: LineSegment StartX=120.669 StartY=65.4973 StartZ=0 EndX=115.591 EndY=69.7147 EndZ=0
    g98: LineSegment StartX=115.591 StartY=69.7147 StartZ=0 EndX=117.293 EndY=71.7641 EndZ=0
    g99: LineSegment StartX=117.293 StartY=71.7641 StartZ=0 EndX=122.37 EndY=67.5474 EndZ=0
    g100: LineSegment StartX=123.967 StartY=69.4706 StartZ=0 EndX=175.025 EndY=27.0667 EndZ=0
    g101: LineSegment StartX=179.022 StartY=27.0606 StartZ=0 EndX=179.022 EndY=120.221 EndZ=0
    g102-g117: Circle x16 (B-spline internal-alignment scaffolding for g118; pole/knot coordinates omitted)
    g118: BSplineCurve PolesCount=16 KnotsCount=14 Degree=3 IsPeriodic=0
    g119-g132: GeomPoint x14 (B-spline internal-alignment scaffolding for g118; pole/knot coordinates omitted)
  constraints (180):
    c: Weight(g0) = 1
    c: Equal(g0,g1)
    c: Equal(g0,g2)
    c: InternalAlignment(g0,g3)
    c: InternalAlignment(g1,g3)
    c: InternalAlignment(g2,g3)
    c: InternalAlignment(g4,g3)
    c: InternalAlignment(g5,g3)
    c: Weight(g6) = 1
    c: Equal(g6,g7)
    c: Equal(g6,g8)
    c: InternalAlignment(g6,g9)
    c: InternalAlignment(g7,g9)
    c: InternalAlignment(g8,g9)
    c: InternalAlignment(g10,g9)
    c: InternalAlignment(g11,g9)
    c: Block(g9)
    c: Block(g3)
    c: Weight(g12) = 1
    c: Equal(g12,g13)
    c: Equal(g12,g14)
    c: InternalAlignment(g12,g15)
    c: InternalAlignment(g13,g15)
    c: InternalAlignment(g14,g15)
    c: InternalAlignment(g16,g15)
    c: InternalAlignment(g17,g15)
    c: Weight(g18) = 1
    c: Equal(g18,g19)
    c: Equal(g18,g20)
    c: InternalAlignment(g18,g21)
    c: InternalAlignment(g19,g21)
    c: InternalAlignment(g20,g21)
    c: InternalAlignment(g22,g21)
    c: InternalAlignment(g23,g21)
    c: Block(g15)
    c: Block(g21)
    c: Weight(g24) = 1
    c: Equal(g24,g25)
    c: Equal(g24,g26)
    c: InternalAlignment(g24,g27)
    c: InternalAlignment(g25,g27)
    c: InternalAlignment(g26,g27)
    c: InternalAlignment(g28,g27)
    c: InternalAlignment(g29,g27)
    c: Block(g27)
    c: Weight(g30) = 1
    c: Equal(g30,g31)
    c: Equal(g30,g32)
    c: InternalAlignment(g30,g33)
    c: InternalAlignment(g31,g33)
    c: InternalAlignment(g32,g33)
    c: InternalAlignment(g34,g33)
    c: InternalAlignment(g35,g33)
    c: Block(g33)
    c: Weight(g36) = 1
    c: Equal(g36,g37)
    c: Equal(g36,g38)
    c: InternalAlignment(g36,g39)
    c: InternalAlignment(g37,g39)
    c: InternalAlignment(g38,g39)
    c: InternalAlignment(g40,g39)
    c: InternalAlignment(g41,g39)
    c: Weight(g42) = 1
    c: Equal(g42,g43)
    c: Equal(g42,g44)
    c: InternalAlignment(g42,g45)
    c: InternalAlignment(g43,g45)
    c: InternalAlignment(g44,g45)
    c: InternalAlignment(g46,g45)
    c: InternalAlignment(g47,g45)
    c: Block(g45)
    c: Block(g39)
    c: Vertical(g48)
    c: Distance(g48) = 3
    c: Weight(g49) = 1
    c: Equal(g49,g50)
    c: Equal(g49,g51)
    c: Equal(g49,g52)
    c: Coincident(g53,g48)
    c: InternalAlignment(g49-g52 -> g53) x4
    c: InternalAlignment(g54,g53)
    c: InternalAlignment(g55,g53)
    c: InternalAlignment(g56,g53)
    c: Weight(g57) = 1
    c: Equal(g57, g58-g61) x4
    c: InternalAlignment(g57-g61 -> g62) x5
    c: InternalAlignment(g63,g62)
    c: InternalAlignment(g64,g62)
    c: InternalAlignment(g65,g62)
    c: Block(g62)
    c: Block(g67)
    c: Block(g68)
    c: Distance(g69) = 2.41
    c: Distance(g70) = 2.76
    c: Distance(g71) = 2.5
    c: Distance(g72) = 2.5
    c: Block(g66)
    c: Block(g48)
    c: Block(g53)
    c: Coincident(g73,g53)
    c: Vertical(g73)
    c: Distance(g73) = 3
    c: Coincident(g74,g73)
    c: Horizontal(g74)
    c: Distance(g74) = 100
    c: Coincident(g75,g74)
    c: Coincident(g75,g62)
    c: Vertical(g75)
    c: Distance(g75) = 3
    c: Coincident(g76,g62)
    c: Vertical(g76)
    c: Distance(g76) = 3
    c: Coincident(g77,g76)
    c: Coincident(g77,g45)
    c: Horizontal(g77)
    c: Distance(g77) = 42.95
    c: Coincident(g78,g39)
    c: Coincident(g78,g48)
    c: Horizontal(g78)
    c: Distance(g78) = 42.95
    c: Coincident(g79,g39)
    c: Coincident(g79,g9)
    c: Vertical(g79)
    c: Distance(g79) = 93.16
    c: Coincident(g80,g9)
    c: Coincident(g80,g69)
    c: Angle(g80) = 0.693245
    c: Block(g80)
    c: Coincident(g81,g69)
    c: Coincident(g81,g70)
    c: Block(g81)
    c: Coincident(g82,g70)
    c: Coincident(g82,g71)
    c: Block(g82)
    c: Coincident(g83,g71)
    c: Coincident(g83,g33)
    c: Block(g71)
    c: Coincident(g84,g33)
    c: Coincident(g84,g67)
    c: Coincident(g85,g67)
    c: Coincident(g85,g66)
    c: Coincident(g86,g66)
    c: Coincident(g86,g68)
    c: Coincident(g87,g68)
    c: Coincident(g87,g21)
    c: Coincident(g88,g15)
    c: Coincident(g89,g88)
    c: Block(g89)
    c: Coincident(g90,g89)
    c: Block(g90)
    c: Block(g91)
    c: Coincident(g92,g91)
    c: Block(g92)
    c: Coincident(g93,g91)
    c: Coincident(g93,g90)
    c: Block(g93)
    c: Coincident(g94,g92)
    c: Coincident(g94,g27)
    c: Coincident(g95,g27)
    c: Block(g95)
    c: Coincident(g96,g95)
    c: Coincident(g97,g96)
    c: Coincident(g98,g97)
    c: Coincident(g99,g98)
    c: Coincident(g99,g72)
    c: Block(g98)
    c: Block(g96)
    c: Block(g72)
    c: Coincident(g100,g72)
    c: Coincident(g100,g3)
    c: Coincident(g101,g3)
    c: Coincident(g101,g45)
    c: Vertical(g101)
    c: Coincident(g118,g21)
    c: Weight(g102) = 1
    c: Equal(g102, g103-g117) x15
    c: Coincident(g118,g15)
    c: InternalAlignment(g102-g117 -> g118) x16
    c: InternalAlignment(g119-g132 -> g118) x14
    c: Block(g118)
FEATURE [Sketcher::SketchObject] Sketch006  label="leftSideTop"
  FullyConstrained = true
  sketch-geometry (99):
    g0: Circle CenterX=61.1495 CenterY=111.695 CenterZ=0 NormalX=0 NormalY=0 NormalZ=1 AngleXU=0 Radius=1
    g1: Circle CenterX=58.0728 CenterY=114.251 CenterZ=0 NormalX=0 NormalY=0 NormalZ=1 AngleXU=0 Radius=1
    g2: Circle CenterX=58.0728 CenterY=110.251 CenterZ=0 NormalX=0 NormalY=0 NormalZ=1 AngleXU=0 Radius=1
    g3: BSplineCurve PolesCount=3 KnotsCount=2 Degree=2 IsPeriodic=0
    g4: GeomPoint X=61.1495 Y=111.695 Z=0
    g5: GeomPoint X=58.0728 Y=110.251 Z=0
    g6: Circle CenterX=61.5791 CenterY=89.3511 CenterZ=0 NormalX=0 NormalY=0 NormalZ=1 AngleXU=0 Radius=1
    g7: Circle CenterX=58.0728 CenterY=91.2763 CenterZ=0 NormalX=0 NormalY=0 NormalZ=1 AngleXU=0 Radius=1
    g8: Circle CenterX=58.0728 CenterY=95.2763 CenterZ=0 NormalX=0 NormalY=0 NormalZ=1 AngleXU=0 Radius=1
    g9: BSplineCurve PolesCount=3 KnotsCount=2 Degree=2 IsPeriodic=0
    g10: GeomPoint X=61.5791 Y=89.3511 Z=0
    g11: GeomPoint X=58.0728 Y=95.2763 Z=0
    g12: Circle CenterX=62.0728 CenterY=124.221 CenterZ=0 NormalX=0 NormalY=0 NormalZ=1 AngleXU=0 Radius=1
    g13: Circle CenterX=58.0728 CenterY=124.221 CenterZ=0 NormalX=0 NormalY=0 NormalZ=1 AngleXU=0 Radius=1
    g14: Circle CenterX=61.1496 CenterY=121.665 CenterZ=0 NormalX=0 NormalY=0 NormalZ=1 AngleXU=0 Radius=1
    g15: BSplineCurve PolesCount=3 KnotsCount=2 Degree=2 IsPeriodic=0
    g16: GeomPoint X=62.0728 Y=124.221 Z=0
    g17: GeomPoint X=61.1496 Y=121.665 Z=0
    g18: Circle CenterX=61.5791 CenterY=75.4095 CenterZ=0 NormalX=0 NormalY=0 NormalZ=1 AngleXU=0 Radius=1
    g19: Circle CenterX=58.0728 CenterY=77.3346 CenterZ=0 NormalX=0 NormalY=0 NormalZ=1 AngleXU=0 Radius=1
    g20: Circle CenterX=58.0728 CenterY=73.3346 CenterZ=0 NormalX=0 NormalY=0 NormalZ=1 AngleXU=0 Radius=1
    g21: BSplineCurve PolesCount=3 KnotsCount=2 Degree=2 IsPeriodic=0
    g22: GeomPoint X=61.5791 Y=75.4095 Z=0
    g23: GeomPoint X=58.0728 Y=73.3346 Z=0
    g24: Circle CenterX=2.07281 CenterY=124.221 CenterZ=0 NormalX=0 NormalY=0 NormalZ=1 AngleXU=0 Radius=1
    g25: Circle CenterX=1.57905 CenterY=122.295 CenterZ=0 NormalX=0 NormalY=0 NormalZ=1 AngleXU=0 Radius=1
    g26: BSplineCurve PolesCount=3 KnotsCount=2 Degree=2 IsPeriodic=0
    g27: GeomPoint X=2.07281 Y=124.221 Z=0
    g28: GeomPoint X=1.57905 Y=122.295 Z=0
    g29: Circle CenterX=46.0728 CenterY=124.221 CenterZ=0 NormalX=0 NormalY=0 NormalZ=1 AngleXU=0 Radius=1
    g30: Circle CenterX=46.0728 CenterY=120.221 CenterZ=0 NormalX=0 NormalY=0 NormalZ=1 AngleXU=0 Radius=1
    g31: BSplineCurve PolesCount=3 KnotsCount=2 Degree=2 IsPeriodic=0
    g32: GeomPoint X=42.0728 Y=124.221 Z=0
    g33: GeomPoint X=46.0728 Y=120.221 Z=0
    g34: Circle CenterX=46.0728 CenterY=109.865 CenterZ=0 NormalX=0 NormalY=0 NormalZ=1 AngleXU=0 Radius=1
    g35: Circle CenterX=46.0728 CenterY=105.865 CenterZ=0 NormalX=0 NormalY=0 NormalZ=1 AngleXU=0 Radius=1
    g36: Circle CenterX=42.0728 CenterY=105.865 CenterZ=0 NormalX=0 NormalY=0 NormalZ=1 AngleXU=0 Radius=1
    g37: BSplineCurve PolesCount=3 KnotsCount=2 Degree=2 IsPeriodic=0
    g38: GeomPoint X=46.0728 Y=109.865 Z=0
    g39: GeomPoint X=42.0728 Y=105.865 Z=0
    g40: Circle CenterX=35.5028 CenterY=105.865 CenterZ=0 NormalX=0 NormalY=0 NormalZ=1 AngleXU=0 Radius=1
    g41: Circle CenterX=31.5028 CenterY=105.865 CenterZ=0 NormalX=0 NormalY=0 NormalZ=1 AngleXU=0 Radius=1
    g42: Circle CenterX=27.9965 CenterY=107.79 CenterZ=0 NormalX=0 NormalY=0 NormalZ=1 AngleXU=0 Radius=1
    g43: BSplineCurve PolesCount=3 KnotsCount=2 Degree=2 IsPeriodic=0
    g44: GeomPoint X=35.5028 Y=105.865 Z=0
    g45: GeomPoint X=27.9965 Y=107.79 Z=0
    g46-g50: Circle x5 (B-spline internal-alignment scaffolding for g51; pole/knot coordinates omitted)
    g51: BSplineCurve PolesCount=5 KnotsCount=3 Degree=3 IsPeriodic=0
    g52: GeomPoint X=132.072 Y=133.221 Z=0
    g53: GeomPoint X=141.072 Y=130.221 Z=0
    g54: GeomPoint X=132.072 Y=127.221 Z=0
    g55: ArcOfCircle CenterX=116.562 CenterY=52.0649 CenterZ=0 NormalX=0 NormalY=0 NormalZ=1 AngleXU=0 Radius=4.24264 StartAngle=0.283268 EndAngle=4.99566
    g56: LineSegment StartX=123.967 StartY=69.4706 StartZ=0 EndX=122.37 EndY=67.5474 EndZ=0
    g57: LineSegment StartX=117.293 StartY=71.7641 StartZ=0 EndX=115.591 EndY=69.7147 EndZ=0
    g58: LineSegment StartX=120.669 StartY=65.4973 StartZ=0 EndX=119.072 EndY=63.5741 EndZ=0
    g59: LineSegment StartX=124.73 StartY=54.6766 StartZ=0 EndX=123.265 EndY=51.8068 EndZ=0
    g60: LineSegment StartX=120.377 StartY=46.5474 StartZ=0 EndX=118.934 EndY=43.9178 EndZ=0
    g61: BSplineCurve PolesCount=3 KnotsCount=2 Degree=2 IsPeriodic=0
    g62: BSplineCurve PolesCount=3 KnotsCount=2 Degree=2 IsPeriodic=0
    g63: LineSegment StartX=61.5791 StartY=75.4095 StartZ=0 EndX=118.934 EndY=43.9178 EndZ=0
    g64: LineSegment StartX=117.748 StartY=47.9913 StartZ=0 EndX=120.377 EndY=46.5474 EndZ=0
    g65: LineSegment StartX=120.635 StartY=53.2507 StartZ=0 EndX=123.265 EndY=51.8068 EndZ=0
    g66: LineSegment StartX=124.73 StartY=54.6766 StartZ=0 EndX=61.5791 EndY=89.3511 EndZ=0
    g67: LineSegment StartX=58.0728 StartY=95.2763 StartZ=0 EndX=58.0728 EndY=110.251 EndZ=0
    g68: LineSegment StartX=61.1495 StartY=111.695 StartZ=0 EndX=119.072 EndY=63.5741 EndZ=0
    g69: LineSegment StartX=120.669 StartY=65.4973 StartZ=0 EndX=115.591 EndY=69.7147 EndZ=0
    g70: LineSegment StartX=117.293 StartY=71.7641 StartZ=0 EndX=122.37 EndY=67.5474 EndZ=0
    g71: LineSegment StartX=123.967 StartY=69.4706 StartZ=0 EndX=61.1496 EndY=121.665 EndZ=0
    g72: LineSegment StartX=62.0728 StartY=124.221 StartZ=0 EndX=132.072 EndY=124.221 EndZ=0
    g73: LineSegment StartX=132.072 StartY=127.221 StartZ=0 EndX=132.072 EndY=124.221 EndZ=0
    g74: LineSegment StartX=132.072 StartY=133.221 StartZ=0 EndX=132.072 EndY=136.221 EndZ=0
    g75: LineSegment StartX=132.072 StartY=136.221 StartZ=0 EndX=-42.9272 EndY=136.221 EndZ=0
    g76: LineSegment StartX=2.07281 StartY=124.221 StartZ=0 EndX=42.0728 EndY=124.221 EndZ=0
    g77: LineSegment StartX=46.0728 StartY=120.221 StartZ=0 EndX=46.0728 EndY=109.865 EndZ=0
    g78: LineSegment StartX=42.0728 StartY=105.865 StartZ=0 EndX=35.5028 EndY=105.865 EndZ=0
    g79: LineSegment StartX=27.9965 StartY=107.79 StartZ=0 EndX=1.57905 EndY=122.295 EndZ=0
    g80: LineSegment StartX=-6.92718 StartY=76.4095 StartZ=0 EndX=42.0728 EndY=76.4095 EndZ=0
    g81: LineSegment StartX=-17.9272 StartY=48.2206 StartZ=0 EndX=-17.9272 EndY=58.2206 EndZ=0
    g82: LineSegment StartX=-35.9272 StartY=48.2206 StartZ=0 EndX=-35.9272 EndY=52.2206 EndZ=0
    g83: LineSegment StartX=-29.9272 StartY=48.2206 StartZ=0 EndX=-29.9272 EndY=52.2206 EndZ=0
    g84: LineSegment StartX=-23.9272 StartY=48.2206 StartZ=0 EndX=-23.9272 EndY=58.2206 EndZ=0
    g85: ArcOfCircle CenterX=-32.9272 CenterY=55.2206 CenterZ=0 NormalX=0 NormalY=0 NormalZ=1 AngleXU=0 Radius=4.24264 StartAngle=5.49779 EndAngle=10.2102
    g86: ArcOfCircle CenterX=-20.9272 CenterY=61.2206 CenterZ=0 NormalX=0 NormalY=0 NormalZ=1 AngleXU=0 Radius=4.24264 StartAngle=5.49779 EndAngle=10.2102
    g87: LineSegment StartX=-10.9272 StartY=48.2206 StartZ=0 EndX=-10.9272 EndY=72.4095 EndZ=0
    g88: LineSegment StartX=-42.9272 StartY=48.2206 StartZ=0 EndX=-42.9272 EndY=136.221 EndZ=0
    g89: LineSegment StartX=46.0728 StartY=72.4095 StartZ=0 EndX=46.0728 EndY=-27.5905 EndZ=0
    g90: LineSegment StartX=58.0728 StartY=-27.5905 StartZ=0 EndX=58.0728 EndY=73.3346 EndZ=0
    g91: LineSegment StartX=50.0728 StartY=-27.5905 StartZ=0 EndX=50.0728 EndY=-31.5905 EndZ=0
    g92: LineSegment StartX=54.0728 StartY=-27.5905 StartZ=0 EndX=54.0728 EndY=-31.5905 EndZ=0
    g93: ArcOfCircle CenterX=52.0728 CenterY=-33.5905 CenterZ=0 NormalX=0 NormalY=0 NormalZ=1 AngleXU=0 Radius=2.82843 StartAngle=2.35619 EndAngle=7.06858
    g94: LineSegment StartX=46.0728 StartY=-27.5905 StartZ=0 EndX=50.0728 EndY=-27.5905 EndZ=0
    g95: LineSegment StartX=54.0728 StartY=-27.5905 StartZ=0 EndX=58.0728 EndY=-27.5905 EndZ=0
    g96: LineSegment StartX=-17.9272 StartY=48.2206 StartZ=0 EndX=-10.9272 EndY=48.2206 EndZ=0
    g97: LineSegment StartX=-29.9272 StartY=48.2206 StartZ=0 EndX=-23.9272 EndY=48.2206 EndZ=0
    g98: LineSegment StartX=-42.9272 StartY=48.2206 StartZ=0 EndX=-35.9272 EndY=48.2206 EndZ=0
  constraints (172):
    c: Weight(g0) = 1
    c: Equal(g0,g1)
    c: Equal(g0,g2)
    c: InternalAlignment(g0,g3)
    c: InternalAlignment(g1,g3)
    c: InternalAlignment(g2,g3)
    c: InternalAlignment(g4,g3)
    c: InternalAlignment(g5,g3)
    c: Weight(g6) = 1
    c: Equal(g6,g7)
    c: Equal(g6,g8)
    c: InternalAlignment(g6,g9)
    c: InternalAlignment(g7,g9)
    c: InternalAlignment(g8,g9)
    c: InternalAlignment(g10,g9)
    c: InternalAlignment(g11,g9)
    c: Block(g3)
    c: Block(g9)
    c: Weight(g12) = 1
    c: Equal(g12,g13)
    c: Equal(g12,g14)
    c: InternalAlignment(g12,g15)
    c: InternalAlignment(g13,g15)
    c: InternalAlignment(g14,g15)
    c: InternalAlignment(g16,g15)
    c: InternalAlignment(g17,g15)
    c: Block(g15)
    c: Weight(g18) = 1
    c: Equal(g18,g19)
    c: Equal(g18,g20)
    c: InternalAlignment(g18,g21)
    c: InternalAlignment(g19,g21)
    c: InternalAlignment(g20,g21)
    c: InternalAlignment(g22,g21)
    c: InternalAlignment(g23,g21)
    c: Block(g21)
    c: Weight(g24) = 1
    c: Equal(g24,g25)
    c: InternalAlignment(g24,g26)
    c: InternalAlignment(g25,g26)
    c: InternalAlignment(g27,g26)
    c: InternalAlignment(g28,g26)
    c: InternalAlignment(g29,g31)
    c: InternalAlignment(g30,g31)
    c: InternalAlignment(g32,g31)
    c: InternalAlignment(g33,g31)
    c: Weight(g34) = 1
    c: Equal(g34,g35)
    c: Equal(g34,g36)
    c: InternalAlignment(g34,g37)
    c: InternalAlignment(g35,g37)
    c: InternalAlignment(g36,g37)
    c: InternalAlignment(g38,g37)
    c: InternalAlignment(g39,g37)
    c: Equal(g40,g41)
    c: Equal(g40,g42)
    c: InternalAlignment(g40,g43)
    c: InternalAlignment(g41,g43)
    c: InternalAlignment(g42,g43)
    c: InternalAlignment(g44,g43)
    c: InternalAlignment(g45,g43)
    c: Block(g31)
    c: Block(g37)
    c: Block(g43)
    c: Block(g26)
    c: Weight(g46) = 1
    c: Equal(g46, g47-g50) x4
    c: InternalAlignment(g46-g50 -> g51) x5
    c: InternalAlignment(g52,g51)
    c: InternalAlignment(g53,g51)
    c: InternalAlignment(g54,g51)
    c: Block(g51)
    c: Block(g55)
    c: Block(g56)
    c: Block(g57)
    c: Block(g58)
    c: Block(g59)
    c: Block(g60)
    c: Block(g61)
    c: Block(g62)
    c: Coincident(g90,g21)
    c: Coincident(g63,g21)
    c: Coincident(g63,g60)
    c: Coincident(g64,g55)
    c: Coincident(g64,g60)
    c: Coincident(g65,g55)
    c: Coincident(g65,g59)
    c: Coincident(g66,g59)
    c: Coincident(g66,g9)
    c: Coincident(g67,g9)
    c: Coincident(g67,g3)
    c: Vertical(g67)
    c: Coincident(g68,g3)
    c: Coincident(g68,g58)
    c: Coincident(g69,g58)
    c: Coincident(g69,g57)
    c: Coincident(g70,g57)
    c: Coincident(g70,g56)
    c: Coincident(g71,g56)
    c: Coincident(g71,g15)
    c: Coincident(g72,g15)
    c: Horizontal(g72)
    c: Coincident(g73,g51)
    c: Coincident(g73,g72)
    c: Vertical(g73)
    c: Coincident(g74,g51)
    c: Vertical(g74)
    c: Coincident(g75,g74)
    c: Horizontal(g75)
    c: Coincident(g76,g26)
    c: Coincident(g76,g31)
    c: Horizontal(g76)
    c: Coincident(g77,g31)
    c: Coincident(g77,g37)
    c: Vertical(g77)
    c: Coincident(g78,g37)
    c: Coincident(g78,g43)
    c: Horizontal(g78)
    c: Coincident(g79,g43)
    c: Coincident(g79,g26)
    c: Coincident(g80,g62)
    c: Coincident(g80,g61)
    c: Horizontal(g80)
    c: Vertical(g81)
    c: Distance(g81) = 10
    c: Vertical(g82)
    c: Distance(g82) = 4
    c: Vertical(g83)
    c: Distance(g83) = 4
    c: Vertical(g84)
    c: Distance(g84) = 10
    c: Coincident(g85,g83)
    c: Coincident(g85,g82)
    c: Block(g85)
    c: Coincident(g86,g84)
    c: Coincident(g86,g81)
    c: Block(g86)
    c: Coincident(g87,g62)
    c: Vertical(g87)
    c: Coincident(g88,g75)
    c: Vertical(g88)
    c: Block(g75)
    c: Coincident(g89,g61)
    c: Vertical(g89)
    c: Distance(g89) = 100
    c: Block(g90)
    c: Vertical(g91)
    c: Distance(g91) = 4
    c: Vertical(g92)
    c: Distance(g92) = 4
    c: Coincident(g93,g91)
    c: Coincident(g93,g92)
    c: Block(g93)
    c: Coincident(g94,g89)
    c: Coincident(g94,g91)
    c: Horizontal(g94)
    c: Distance(g94) = 4
    c: Coincident(g95,g92)
    c: Coincident(g95,g90)
    c: Horizontal(g95)
    c: Distance(g95) = 4
    c: Block(g87)
    c: Block(g88)
    c: Coincident(g96,g81)
    c: Coincident(g96,g87)
    c: Horizontal(g96)
    c: Coincident(g97,g83)
    c: Coincident(g97,g84)
    c: Horizontal(g97)
    c: Coincident(g98,g88)
    c: Coincident(g98,g82)
    c: Horizontal(g98)
FEATURE [Sketcher::SketchObject] Sketch007  label="leftSideBottom"
  FullyConstrained = true
  sketch-geometry (92):
    g0: ArcOfCircle CenterX=-26.9272 CenterY=-83.7794 CenterZ=0 NormalX=0 NormalY=0 NormalZ=1 AngleXU=0 Radius=8 StartAngle=3.14159 EndAngle=6.28319
    g1: Circle CenterX=61.5791 CenterY=-56.9099 CenterZ=0 NormalX=0 NormalY=0 NormalZ=1 AngleXU=0 Radius=1
    g2: Circle CenterX=58.0728 CenterY=-58.8351 CenterZ=0 NormalX=0 NormalY=0 NormalZ=1 AngleXU=0 Radius=1
    g3: Circle CenterX=58.0728 CenterY=-62.8351 CenterZ=0 NormalX=0 NormalY=0 NormalZ=1 AngleXU=0 Radius=1
    g4: BSplineCurve PolesCount=3 KnotsCount=2 Degree=2 IsPeriodic=0
    g5: GeomPoint X=61.5791 Y=-56.9099 Z=0
    g6: GeomPoint X=58.0728 Y=-62.8351 Z=0
    g7: Circle CenterX=58.0728 CenterY=-77.8102 CenterZ=0 NormalX=0 NormalY=0 NormalZ=1 AngleXU=0 Radius=1
    g8: Circle CenterX=58.0728 CenterY=-81.8102 CenterZ=0 NormalX=0 NormalY=0 NormalZ=1 AngleXU=0 Radius=1
    g9: Circle CenterX=61.1496 CenterY=-79.2541 CenterZ=0 NormalX=0 NormalY=0 NormalZ=1 AngleXU=0 Radius=1
    g10: BSplineCurve PolesCount=3 KnotsCount=2 Degree=2 IsPeriodic=0
    g11: GeomPoint X=58.0728 Y=-77.8102 Z=0
    g12: GeomPoint X=61.1496 Y=-79.2541 Z=0
    g13: Circle CenterX=61.6457 CenterY=-88.8112 CenterZ=0 NormalX=0 NormalY=0 NormalZ=1 AngleXU=0 Radius=1
    g14: Circle CenterX=58.0728 CenterY=-91.7794 CenterZ=0 NormalX=0 NormalY=0 NormalZ=1 AngleXU=0 Radius=1
    g15: Circle CenterX=63.9135 CenterY=-91.8014 CenterZ=0 NormalX=0 NormalY=0 NormalZ=1 AngleXU=0 Radius=1
    g16: BSplineCurve PolesCount=3 KnotsCount=2 Degree=2 IsPeriodic=0
    g17: GeomPoint X=61.6457 Y=-88.8112 Z=0
    g18: GeomPoint X=63.9135 Y=-91.8014 Z=0
    g19: Circle CenterX=58.0728 CenterY=-40.8935 CenterZ=0 NormalX=0 NormalY=0 NormalZ=1 AngleXU=0 Radius=1
    g20: Circle CenterX=58.0728 CenterY=-44.8935 CenterZ=0 NormalX=0 NormalY=0 NormalZ=1 AngleXU=0 Radius=1
    g21: Circle CenterX=61.5791 CenterY=-42.9683 CenterZ=0 NormalX=0 NormalY=0 NormalZ=1 AngleXU=0 Radius=1
    g22: BSplineCurve PolesCount=3 KnotsCount=2 Degree=2 IsPeriodic=0
    g23: GeomPoint X=58.0728 Y=-40.8935 Z=0
    g24: GeomPoint X=61.5791 Y=-42.9683 Z=0
    g25: Circle CenterX=42.5666 CenterY=-67.3492 CenterZ=0 NormalX=0 NormalY=0 NormalZ=1 AngleXU=0 Radius=1
    g26: Circle CenterX=46.0728 CenterY=-65.424 CenterZ=0 NormalX=0 NormalY=0 NormalZ=1 AngleXU=0 Radius=1
    g27: Circle CenterX=46.0728 CenterY=-69.424 CenterZ=0 NormalX=0 NormalY=0 NormalZ=1 AngleXU=0 Radius=1
    g28: BSplineCurve PolesCount=3 KnotsCount=2 Degree=2 IsPeriodic=0
    g29: GeomPoint X=42.5666 Y=-67.3492 Z=0
    g30: GeomPoint X=46.0728 Y=-69.424 Z=0
    g31: Circle CenterX=2.07281 CenterY=-91.7794 CenterZ=0 NormalX=0 NormalY=0 NormalZ=1 AngleXU=0 Radius=1
    g32: Circle CenterX=-1.92719 CenterY=-91.7794 CenterZ=0 NormalX=0 NormalY=0 NormalZ=1 AngleXU=0 Radius=1
    g33: Circle CenterX=1.57905 CenterY=-89.8542 CenterZ=0 NormalX=0 NormalY=0 NormalZ=1 AngleXU=0 Radius=1
    g34: BSplineCurve PolesCount=3 KnotsCount=2 Degree=2 IsPeriodic=0
    g35: GeomPoint X=2.07281 Y=-91.7794 Z=0
    g36: GeomPoint X=1.57905 Y=-89.8542 Z=0
    g37: ArcOfCircle CenterX=-26.9272 CenterY=22.1087 CenterZ=0 NormalX=0 NormalY=0 NormalZ=1 AngleXU=0 Radius=4 StartAngle=5e-16 EndAngle=3.14159
    g38: Circle CenterX=-10.9272 CenterY=-78.7794 CenterZ=0 NormalX=0 NormalY=0 NormalZ=1 AngleXU=0 Radius=1
    g39: Circle CenterX=-10.9272 CenterY=-82.7794 CenterZ=0 NormalX=0 NormalY=0 NormalZ=1 AngleXU=0 Radius=1
    g40: Circle CenterX=-7.42095 CenterY=-80.8542 CenterZ=0 NormalX=0 NormalY=0 NormalZ=1 AngleXU=0 Radius=1
    g41: BSplineCurve PolesCount=3 KnotsCount=2 Degree=2 IsPeriodic=0
    g42: GeomPoint X=-10.9272 Y=-78.7794 Z=0
    g43: GeomPoint X=-7.42095 Y=-80.8542 Z=0
    g44: BSplineCurve PolesCount=3 KnotsCount=2 Degree=2 IsPeriodic=0
    g45: GeomPoint X=42.5666 Y=-53.4075 Z=0
    g46: GeomPoint X=46.0728 Y=-47.4823 Z=0
    g47: BSplineCurve PolesCount=5 KnotsCount=3 Degree=3 IsPeriodic=0
    g48: LineSegment StartX=124.814 StartY=-22.1885 StartZ=0 EndX=123.265 EndY=-19.3655 EndZ=0
    g49: ArcOfCircle CenterX=116.562 CenterY=-19.6236 CenterZ=0 NormalX=0 NormalY=0 NormalZ=1 AngleXU=0 Radius=4.24264 StartAngle=1.28753 EndAngle=6.00037
    g50: LineSegment StartX=-30.9272 StartY=22.1087 StartZ=0 EndX=-34.9272 EndY=-83.7794 EndZ=0
    g51: LineSegment StartX=-22.9272 StartY=22.1087 StartZ=0 EndX=-18.9272 EndY=-83.7794 EndZ=0
    g52: LineSegment StartX=118.934 StartY=-11.4765 StartZ=0 EndX=120.377 EndY=-14.1062 EndZ=0
    g53: LineSegment StartX=118.86 StartY=-31.3104 StartZ=0 EndX=120.377 EndY=-33.1447 EndZ=0
    g54: LineSegment StartX=115.291 StartY=-37.3514 StartZ=0 EndX=117.05 EndY=-39.4781 EndZ=0
    g55: LineSegment StartX=122.136 StartY=-35.2714 StartZ=0 EndX=123.656 EndY=-37.1092 EndZ=0
    g56: BSplineCurve PolesCount=3 KnotsCount=2 Degree=2 IsPeriodic=0
    g57: LineSegment StartX=132.072 StartY=-100.779 StartZ=0 EndX=132.072 EndY=-103.779 EndZ=0
    g58: LineSegment StartX=132.072 StartY=-91.8014 StartZ=0 EndX=132.072 EndY=-94.7791 EndZ=0
    g59: LineSegment StartX=63.9135 StartY=-91.8014 StartZ=0 EndX=132.072 EndY=-91.8014 EndZ=0
    g60: LineSegment StartX=61.6457 StartY=-88.8112 StartZ=0 EndX=123.656 EndY=-37.1092 EndZ=0
    g61: LineSegment StartX=122.136 StartY=-35.2714 StartZ=0 EndX=117.05 EndY=-39.4781 EndZ=0
    g62: LineSegment StartX=115.291 StartY=-37.3514 StartZ=0 EndX=120.377 EndY=-33.1447 EndZ=0
    g63: LineSegment StartX=118.86 StartY=-31.3104 StartZ=0 EndX=61.1496 EndY=-79.2541 EndZ=0
    g64: LineSegment StartX=58.0728 StartY=-77.8102 StartZ=0 EndX=58.0728 EndY=-62.8351 EndZ=0
    g65: LineSegment StartX=61.5791 StartY=-56.9099 StartZ=0 EndX=124.814 EndY=-22.1885 EndZ=0
    g66: LineSegment StartX=120.636 StartY=-20.8076 StartZ=0 EndX=123.265 EndY=-19.3655 EndZ=0
    g67: LineSegment StartX=117.748 StartY=-15.55 StartZ=0 EndX=120.377 EndY=-14.1062 EndZ=0
    g68: LineSegment StartX=118.934 StartY=-11.4765 StartZ=0 EndX=61.5791 EndY=-42.9683 EndZ=0
    g69: LineSegment StartX=-42.9272 StartY=-103.779 StartZ=0 EndX=132.072 EndY=-103.779 EndZ=0
    g70: LineSegment StartX=42.5666 StartY=-53.4075 StartZ=0 EndX=-7.42095 EndY=-80.8542 EndZ=0
    g71: LineSegment StartX=-10.9272 StartY=-78.7794 StartZ=0 EndX=-10.9272 EndY=48.2206 EndZ=0
    g72: LineSegment StartX=2.07281 StartY=-91.7794 StartZ=0 EndX=42.0728 EndY=-91.7794 EndZ=0
    g73: LineSegment StartX=46.0728 StartY=-87.7794 StartZ=0 EndX=46.0728 EndY=-69.424 EndZ=0
    g74: LineSegment StartX=42.5666 StartY=-67.3492 StartZ=0 EndX=1.57905 EndY=-89.8542 EndZ=0
    g75: LineSegment StartX=-42.9272 StartY=-103.779 StartZ=0 EndX=-42.9272 EndY=48.2206 EndZ=0
    g76: LineSegment StartX=-17.9272 StartY=48.2206 StartZ=0 EndX=-17.9272 EndY=58.2206 EndZ=0
    g77: LineSegment StartX=-35.9272 StartY=48.2206 StartZ=0 EndX=-35.9272 EndY=52.2206 EndZ=0
    g78: LineSegment StartX=-29.9272 StartY=48.2206 StartZ=0 EndX=-29.9272 EndY=52.2206 EndZ=0
    g79: LineSegment StartX=-23.9272 StartY=48.2206 StartZ=0 EndX=-23.9272 EndY=58.2206 EndZ=0
    g80: ArcOfCircle CenterX=-32.9272 CenterY=55.2206 CenterZ=0 NormalX=0 NormalY=0 NormalZ=1 AngleXU=0 Radius=4.24264 StartAngle=5.49779 EndAngle=10.2102
    g81: ArcOfCircle CenterX=-20.9272 CenterY=61.2206 CenterZ=0 NormalX=0 NormalY=0 NormalZ=1 AngleXU=0 Radius=4.24264 StartAngle=5.49779 EndAngle=10.2102
    g82: LineSegment StartX=-17.9272 StartY=48.2206 StartZ=0 EndX=-10.9272 EndY=48.2206 EndZ=0
    g83: LineSegment StartX=-42.9272 StartY=48.2206 StartZ=0 EndX=-35.9272 EndY=48.2206 EndZ=0
    g84: LineSegment StartX=50.0728 StartY=-27.5905 StartZ=0 EndX=50.0728 EndY=-31.5905 EndZ=0
    g85: LineSegment StartX=54.0728 StartY=-27.5905 StartZ=0 EndX=54.0728 EndY=-31.5905 EndZ=0
    g86: ArcOfCircle CenterX=52.0728 CenterY=-33.5905 CenterZ=0 NormalX=0 NormalY=0 NormalZ=1 AngleXU=0 Radius=2.82843 StartAngle=2.35619 EndAngle=7.06858
    g87: LineSegment StartX=46.0728 StartY=-27.5905 StartZ=0 EndX=50.0728 EndY=-27.5905 EndZ=0
    g88: LineSegment StartX=54.0728 StartY=-27.5905 StartZ=0 EndX=58.0728 EndY=-27.5905 EndZ=0
    g89: LineSegment StartX=46.0728 StartY=-27.5905 StartZ=0 EndX=46.0728 EndY=-47.4823 EndZ=0
    g90: LineSegment StartX=58.0728 StartY=-27.5905 StartZ=0 EndX=58.0728 EndY=-40.8935 EndZ=0
    g91: LineSegment StartX=-29.9272 StartY=48.2206 StartZ=0 EndX=-23.9272 EndY=48.2206 EndZ=0
  constraints (170):
    c: Weight(g1) = 1
    c: Equal(g1,g2)
    c: Equal(g1,g3)
    c: InternalAlignment(g1,g4)
    c: InternalAlignment(g2,g4)
    c: InternalAlignment(g3,g4)
    c: InternalAlignment(g5,g4)
    c: InternalAlignment(g6,g4)
    c: Weight(g7) = 1
    c: Equal(g7,g8)
    c: Equal(g7,g9)
    c: InternalAlignment(g7,g10)
    c: InternalAlignment(g8,g10)
    c: InternalAlignment(g9,g10)
    c: InternalAlignment(g11,g10)
    c: InternalAlignment(g12,g10)
    c: Block(g4)
    c: Block(g10)
    c: Weight(g13) = 1
    c: Equal(g13,g14)
    c: Equal(g13,g15)
    c: InternalAlignment(g13,g16)
    c: InternalAlignment(g14,g16)
    c: InternalAlignment(g15,g16)
    c: InternalAlignment(g17,g16)
    c: InternalAlignment(g18,g16)
    c: Block(g16)
    c: Weight(g19) = 1
    c: Equal(g19,g20)
    c: Equal(g19,g21)
    c: InternalAlignment(g19,g22)
    c: InternalAlignment(g20,g22)
    c: InternalAlignment(g21,g22)
    c: InternalAlignment(g23,g22)
    c: InternalAlignment(g24,g22)
    c: Block(g22)
    c: Weight(g25) = 1
    c: Equal(g25,g26)
    c: Equal(g25,g27)
    c: InternalAlignment(g25,g28)
    c: InternalAlignment(g26,g28)
    c: InternalAlignment(g27,g28)
    c: InternalAlignment(g29,g28)
    c: InternalAlignment(g30,g28)
    c: Weight(g31) = 1
    c: Equal(g31,g32)
    c: Equal(g31,g33)
    c: InternalAlignment(g31,g34)
    c: InternalAlignment(g32,g34)
    c: InternalAlignment(g33,g34)
    c: InternalAlignment(g35,g34)
    c: InternalAlignment(g36,g34)
    c: Block(g34)
    c: Block(g28)
    c: Block(g37)
    c: Block(g0)
    c: Weight(g38) = 1
    c: Equal(g38,g40)
    c: InternalAlignment(g38,g41)
    c: InternalAlignment(g39,g41)
    c: InternalAlignment(g40,g41)
    c: InternalAlignment(g42,g41)
    c: InternalAlignment(g43,g41)
    c: InternalAlignment(g45,g44)
    c: InternalAlignment(g46,g44)
    c: Block(g47)
    c: Block(g44)
    c: Block(g41)
    c: Block(g48)
    c: Block(g49)
    c: Coincident(g50,g37)
    c: Coincident(g50,g0)
    c: Coincident(g51,g37)
    c: Coincident(g51,g0)
    c: Block(g51)
    c: Block(g50)
    c: Block(g52)
    c: Block(g53)
    c: Block(g54)
    c: Block(g55)
    c: Block(g56)
    c: Coincident(g57,g47)
    c: Vertical(g57)
    c: Coincident(g58,g47)
    c: Vertical(g58)
    c: Coincident(g59,g16)
    c: Coincident(g59,g58)
    c: Horizontal(g59)
    c: Coincident(g60,g16)
    c: Coincident(g60,g55)
    c: Coincident(g61,g55)
    c: Coincident(g61,g54)
    c: Coincident(g62,g54)
    c: Coincident(g62,g53)
    c: Coincident(g63,g53)
    c: Coincident(g63,g10)
    c: Coincident(g64,g10)
    c: Coincident(g64,g4)
    c: Vertical(g64)
    c: Coincident(g65,g4)
    c: Coincident(g65,g48)
    c: Coincident(g66,g49)
    c: Coincident(g66,g48)
    c: Coincident(g67,g49)
    c: Coincident(g67,g52)
    c: Coincident(g68,g52)
    c: Coincident(g68,g22)
    c: Coincident(g69,g57)
    c: Horizontal(g69)
    c: Coincident(g70,g44)
    c: Coincident(g70,g41)
    c: Coincident(g71,g41)
    c: Vertical(g71)
    c: Coincident(g72,g34)
    c: Coincident(g72,g56)
    c: Horizontal(g72)
    c: Coincident(g73,g56)
    c: Coincident(g73,g28)
    c: Vertical(g73)
    c: Coincident(g74,g28)
    c: Coincident(g74,g34)
    c: Block(g69)
    c: Coincident(g75,g69)
    c: Vertical(g75)
    c: Distance(g75) = 152
    c: Block(g71)
    c: Vertical(g76)
    c: Distance(g76) = 10
    c: Vertical(g77)
    c: Distance(g77) = 4
    c: Vertical(g78)
    c: Distance(g78) = 4
    c: Vertical(g79)
    c: Distance(g79) = 10
    c: Coincident(g80,g78)
    c: Coincident(g80,g77)
    c: Block(g80)
    c: Coincident(g81,g79)
    c: Coincident(g81,g76)
    c: Block(g81)
    c: Coincident(g82,g76)
    c: Coincident(g82,g71)
    c: Horizontal(g82)
    c: Coincident(g83,g75)
    c: Coincident(g83,g77)
    c: Horizontal(g83)
    c: Distance(g83) = 7
    c: Distance(g82) = 7
    c: Vertical(g84)
    c: Distance(g84) = 4
    c: Vertical(g85)
    c: Distance(g85) = 4
    c: Coincident(g86,g84)
    c: Coincident(g86,g85)
    c: Block(g86)
    c: Coincident(g87,g84)
    c: Horizontal(g87)
    c: Distance(g87) = 4
    c: Coincident(g88,g85)
    c: Horizontal(g88)
    c: Distance(g88) = 4
    c: Coincident(g89,g87)
    c: Coincident(g89,g44)
    c: Vertical(g89)
    c: Coincident(g90,g88)
    c: Coincident(g90,g22)
    c: Vertical(g90)
    c: Coincident(g91,g78)
    c: Coincident(g91,g79)
    c: Horizontal(g91)
FEATURE [Sketcher::SketchObject] Sketch008  label="rightSideTop"
  FullyConstrained = false
  sketch-geometry (108):
    g0: Circle CenterX=302.996 CenterY=111.695 CenterZ=0 NormalX=0 NormalY=0 NormalZ=1 AngleXU=0 Radius=1
    g1: Circle CenterX=306.073 CenterY=114.251 CenterZ=0 NormalX=0 NormalY=0 NormalZ=1 AngleXU=0 Radius=1
    g2: Circle CenterX=306.073 CenterY=110.251 CenterZ=0 NormalX=0 NormalY=0 NormalZ=1 AngleXU=0 Radius=1
    g3: BSplineCurve PolesCount=3 KnotsCount=2 Degree=2 IsPeriodic=0
    g4: GeomPoint X=302.996 Y=111.695 Z=0
    g5: GeomPoint X=306.073 Y=110.251 Z=0
    g6: Circle CenterX=306.073 CenterY=95.2763 CenterZ=0 NormalX=0 NormalY=0 NormalZ=1 AngleXU=0 Radius=1
    g7: Circle CenterX=306.073 CenterY=91.2763 CenterZ=0 NormalX=0 NormalY=0 NormalZ=1 AngleXU=0 Radius=1
    g8: Circle CenterX=302.567 CenterY=89.3511 CenterZ=0 NormalX=0 NormalY=0 NormalZ=1 AngleXU=0 Radius=1
    g9: BSplineCurve PolesCount=3 KnotsCount=2 Degree=2 IsPeriodic=0
    g10: GeomPoint X=306.073 Y=95.2763 Z=0
    g11: GeomPoint X=302.567 Y=89.3511 Z=0
    g12: LineSegment StartX=306.073 StartY=110.251 StartZ=0 EndX=306.073 EndY=95.2763 EndZ=0
    g13: Circle CenterX=302.073 CenterY=124.221 CenterZ=0 NormalX=0 NormalY=0 NormalZ=1 AngleXU=0 Radius=1
    g14: Circle CenterX=306.073 CenterY=124.221 CenterZ=0 NormalX=0 NormalY=0 NormalZ=1 AngleXU=0 Radius=1
    g15: Circle CenterX=302.996 CenterY=121.665 CenterZ=0 NormalX=0 NormalY=0 NormalZ=1 AngleXU=0 Radius=1
    g16: BSplineCurve PolesCount=3 KnotsCount=2 Degree=2 IsPeriodic=0
    g17: GeomPoint X=302.073 Y=124.221 Z=0
    g18: GeomPoint X=302.996 Y=121.665 Z=0
    g19: Circle CenterX=306.073 CenterY=73.3346 CenterZ=0 NormalX=0 NormalY=0 NormalZ=1 AngleXU=0 Radius=1
    g20: Circle CenterX=306.073 CenterY=77.3346 CenterZ=0 NormalX=0 NormalY=0 NormalZ=1 AngleXU=0 Radius=1
    g21: Circle CenterX=302.535 CenterY=75.4095 CenterZ=0 NormalX=0 NormalY=0 NormalZ=1 AngleXU=0 Radius=1
    g22: BSplineCurve PolesCount=3 KnotsCount=2 Degree=2 IsPeriodic=0
    g23: GeomPoint X=306.073 Y=73.3346 Z=0
    g24: GeomPoint X=302.535 Y=75.4095 Z=0
    g25: Circle CenterX=362.073 CenterY=124.221 CenterZ=0 NormalX=0 NormalY=0 NormalZ=1 AngleXU=0 Radius=1
    g26: Circle CenterX=366.073 CenterY=124.221 CenterZ=0 NormalX=0 NormalY=0 NormalZ=1 AngleXU=0 Radius=1
    g27: Circle CenterX=362.567 CenterY=122.294 CenterZ=0 NormalX=0 NormalY=0 NormalZ=1 AngleXU=0 Radius=1
    g28: BSplineCurve PolesCount=3 KnotsCount=2 Degree=2 IsPeriodic=0
    g29: GeomPoint X=362.073 Y=124.221 Z=0
    g30: GeomPoint X=362.567 Y=122.294 Z=0
    g31: Circle CenterX=322.073 CenterY=124.221 CenterZ=0 NormalX=0 NormalY=0 NormalZ=1 AngleXU=0 Radius=1
    g32: Circle CenterX=318.073 CenterY=124.221 CenterZ=0 NormalX=0 NormalY=0 NormalZ=1 AngleXU=0 Radius=1
    g33: Circle CenterX=318.073 CenterY=120.221 CenterZ=0 NormalX=0 NormalY=0 NormalZ=1 AngleXU=0 Radius=1
    g34: BSplineCurve PolesCount=3 KnotsCount=2 Degree=2 IsPeriodic=0
    g35: GeomPoint X=322.073 Y=124.221 Z=0
    g36: GeomPoint X=318.073 Y=120.221 Z=0
    g37: Circle CenterX=322.073 CenterY=105.865 CenterZ=0 NormalX=0 NormalY=0 NormalZ=1 AngleXU=0 Radius=1
    g38: Circle CenterX=318.073 CenterY=105.865 CenterZ=0 NormalX=0 NormalY=0 NormalZ=1 AngleXU=0 Radius=1
    g39: Circle CenterX=318.073 CenterY=109.865 CenterZ=0 NormalX=0 NormalY=0 NormalZ=1 AngleXU=0 Radius=1
    g40: BSplineCurve PolesCount=3 KnotsCount=2 Degree=2 IsPeriodic=0
    g41: GeomPoint X=322.073 Y=105.865 Z=0
    g42: GeomPoint X=318.073 Y=109.865 Z=0
    g43: Circle CenterX=336.157 CenterY=107.779 CenterZ=0 NormalX=0 NormalY=0 NormalZ=1 AngleXU=0 Radius=1
    g44: Circle CenterX=332.651 CenterY=105.853 CenterZ=0 NormalX=0 NormalY=0 NormalZ=1 AngleXU=0 Radius=1
    g45: Circle CenterX=328.643 CenterY=105.865 CenterZ=0 NormalX=0 NormalY=0 NormalZ=1 AngleXU=0 Radius=1
    g46: BSplineCurve PolesCount=3 KnotsCount=2 Degree=2 IsPeriodic=0
    g47: GeomPoint X=336.157 Y=107.779 Z=0
    g48: GeomPoint X=328.643 Y=105.865 Z=0
    g49: Circle CenterX=322.073 CenterY=76.4095 CenterZ=0 NormalX=0 NormalY=0 NormalZ=1 AngleXU=0 Radius=4
    g50: BSplineCurve PolesCount=3 KnotsCount=2 Degree=2 IsPeriodic=0
    g51: GeomPoint X=318.073 Y=72.4095 Z=0
    g52: GeomPoint X=322.073 Y=76.4095 Z=0
    g53: Circle CenterX=375.073 CenterY=72.4095 CenterZ=0 NormalX=0 NormalY=0 NormalZ=1 AngleXU=0 Radius=1
    g54: Circle CenterX=375.073 CenterY=76.4095 CenterZ=0 NormalX=0 NormalY=0 NormalZ=1 AngleXU=0 Radius=1
    g55: Circle CenterX=371.073 CenterY=76.4095 CenterZ=0 NormalX=0 NormalY=0 NormalZ=1 AngleXU=0 Radius=1
    g56: BSplineCurve PolesCount=3 KnotsCount=2 Degree=2 IsPeriodic=0
    g57: GeomPoint X=375.073 Y=72.4095 Z=0
    g58: GeomPoint X=371.073 Y=76.4095 Z=0
    g59: LineSegment StartX=322.073 StartY=76.4095 StartZ=0 EndX=371.073 EndY=76.4095 EndZ=0
    g60: Circle CenterX=232.072 CenterY=133.221 CenterZ=0 NormalX=0 NormalY=0 NormalZ=1 AngleXU=0 Radius=1
    g61: Circle CenterX=226.072 CenterY=136.221 CenterZ=0 NormalX=0 NormalY=0 NormalZ=1 AngleXU=0 Radius=1
    g62: Circle CenterX=226.072 CenterY=124.221 CenterZ=0 NormalX=0 NormalY=0 NormalZ=1 AngleXU=0 Radius=1
    g63: Circle CenterX=232.072 CenterY=127.221 CenterZ=0 NormalX=0 NormalY=0 NormalZ=1 AngleXU=0 Radius=1
    g64: BSplineCurve PolesCount=5 KnotsCount=3 Degree=3 IsPeriodic=0
    g65: GeomPoint X=232.072 Y=133.221 Z=0
    g66: GeomPoint X=223.072 Y=130.221 Z=0
    g67: GeomPoint X=232.072 Y=127.221 Z=0
    g68: LineSegment StartX=240.687 StartY=51.8263 StartZ=0 EndX=243.317 EndY=53.2701 EndZ=0
    g69: LineSegment StartX=243.575 StartY=46.5669 StartZ=0 EndX=246.205 EndY=48.0108 EndZ=0
    g70: ArcOfCircle CenterX=247.391 CenterY=52.0843 CenterZ=0 NormalX=0 NormalY=0 NormalZ=1 AngleXU=0 Radius=4.24264 StartAngle=4.42912 EndAngle=9.14151
    g71: LineSegment StartX=243.475 StartY=65.4951 StartZ=0 EndX=245.073 EndY=63.5726 EndZ=0
    g72: LineSegment StartX=243.575 StartY=46.5669 StartZ=0 EndX=245.072 EndY=43.8408 EndZ=0
    g73: LineSegment StartX=245.072 StartY=43.8408 StartZ=0 EndX=302.535 EndY=75.4095 EndZ=0
    g74: LineSegment StartX=239.192 StartY=54.5542 StartZ=0 EndX=302.567 EndY=89.3511 EndZ=0
    g75: LineSegment StartX=232.072 StartY=127.221 StartZ=0 EndX=232.072 EndY=124.221 EndZ=0
    g76: LineSegment StartX=232.072 StartY=136.221 StartZ=0 EndX=232.072 EndY=133.221 EndZ=0
    g77: LineSegment StartX=232.072 StartY=136.221 StartZ=0 EndX=407.073 EndY=136.221 EndZ=0
    g78: LineSegment StartX=322.073 StartY=124.221 StartZ=0 EndX=362.073 EndY=124.221 EndZ=0
    g79: LineSegment StartX=362.567 StartY=122.294 StartZ=0 EndX=336.157 EndY=107.779 EndZ=0
    g80: LineSegment StartX=322.073 StartY=105.865 StartZ=0 EndX=328.643 EndY=105.865 EndZ=0
    g81: LineSegment StartX=318.073 StartY=120.221 StartZ=0 EndX=318.073 EndY=109.865 EndZ=0
    g82: LineSegment StartX=232.072 StartY=124.221 StartZ=0 EndX=302.073 EndY=124.221 EndZ=0
    g83: LineSegment StartX=302.996 StartY=121.665 StartZ=0 EndX=240.171 EndY=69.471 EndZ=0
    g84: LineSegment StartX=240.171 StartY=69.471 StartZ=0 EndX=241.711 EndY=67.6177 EndZ=0
    g85: LineSegment StartX=241.711 StartY=67.6177 StartZ=0 EndX=246.787 EndY=71.8365 EndZ=0
    g86: LineSegment StartX=246.787 StartY=71.8365 StartZ=0 EndX=248.551 EndY=69.712 EndZ=0
    g87: LineSegment StartX=248.551 StartY=69.712 StartZ=0 EndX=243.475 EndY=65.4951 EndZ=0
    g88: LineSegment StartX=245.073 StartY=63.5726 StartZ=0 EndX=302.996 EndY=111.695 EndZ=0
    g89: LineSegment StartX=239.192 StartY=54.5542 StartZ=0 EndX=240.687 EndY=51.8263 EndZ=0
    g90: LineSegment StartX=375.073 StartY=48.2206 StartZ=0 EndX=382.073 EndY=48.2206 EndZ=0
    g91: LineSegment StartX=407.073 StartY=48.2206 StartZ=0 EndX=400.073 EndY=48.2206 EndZ=0
    g92: LineSegment StartX=394.073 StartY=48.2206 StartZ=0 EndX=394.073 EndY=52.2206 EndZ=0
    g93: LineSegment StartX=388.073 StartY=48.2206 StartZ=0 EndX=388.073 EndY=58.2206 EndZ=0
    g94: ArcOfCircle CenterX=385.073 CenterY=61.2206 CenterZ=0 NormalX=0 NormalY=0 NormalZ=1 AngleXU=0 Radius=4.24264 StartAngle=5.49779 EndAngle=10.2102
    g95: ArcOfCircle CenterX=397.073 CenterY=55.2206 CenterZ=0 NormalX=0 NormalY=0 NormalZ=1 AngleXU=0 Radius=4.24264 StartAngle=5.49779 EndAngle=10.2102
    g96: LineSegment StartX=382.073 StartY=58.2206 StartZ=0 EndX=382.073 EndY=48.2206 EndZ=0
    g97: LineSegment StartX=400.073 StartY=52.2206 StartZ=0 EndX=400.073 EndY=48.2206 EndZ=0
    g98: LineSegment StartX=394.073 StartY=48.2206 StartZ=0 EndX=388.073 EndY=48.2206 EndZ=0
    g99: LineSegment StartX=306.073 StartY=-27.5935 StartZ=0 EndX=310.073 EndY=-27.5935 EndZ=0
    g100: LineSegment StartX=318.073 StartY=-27.5935 StartZ=0 EndX=314.073 EndY=-27.5935 EndZ=0
    g101: LineSegment StartX=310.073 StartY=-27.5935 StartZ=0 EndX=310.073 EndY=-31.5935 EndZ=0
    g102: LineSegment StartX=314.073 StartY=-27.5935 StartZ=0 EndX=314.073 EndY=-31.5935 EndZ=0
    g103: ArcOfCircle CenterX=312.073 CenterY=-33.5935 CenterZ=0 NormalX=0 NormalY=0 NormalZ=1 AngleXU=0 Radius=2.82843 StartAngle=2.35619 EndAngle=7.06858
    g104: LineSegment StartX=375.073 StartY=72.4095 StartZ=0 EndX=375.073 EndY=48.2206 EndZ=0
    g105: LineSegment StartX=407.073 StartY=48.2206 StartZ=0 EndX=407.073 EndY=136.221 EndZ=0
    g106: LineSegment StartX=318.073 StartY=-27.5935 StartZ=0 EndX=318.073 EndY=72.4095 EndZ=0
    g107: LineSegment StartX=306.073 StartY=73.3346 StartZ=0 EndX=306.073 EndY=-27.5935 EndZ=0
  constraints (136):
    c: Weight(g0) = 1
    c: Equal(g0,g1)
    c: Equal(g0,g2)
    c: InternalAlignment(g0,g3)
    c: InternalAlignment(g1,g3)
    c: InternalAlignment(g2,g3)
    c: InternalAlignment(g4,g3)
    c: InternalAlignment(g5,g3)
    c: Weight(g6) = 1
    c: Equal(g6,g7)
    c: Equal(g6,g8)
    c: InternalAlignment(g6,g9)
    c: InternalAlignment(g7,g9)
    c: InternalAlignment(g8,g9)
    c: InternalAlignment(g10,g9)
    c: InternalAlignment(g11,g9)
    c: Block(g3)
    c: Block(g9)
    c: Coincident(g12,g3)
    c: Coincident(g12,g9)
    c: Vertical(g12)
    c: Weight(g13) = 1
    c: Equal(g13,g14)
    c: Equal(g13,g15)
    c: InternalAlignment(g14,g16)
    c: InternalAlignment(g15,g16)
    c: InternalAlignment(g17,g16)
    c: InternalAlignment(g18,g16)
    c: Block(g71)
    c: Block(g72)
    c: Coincident(g73,g72)
    c: Coincident(g73,g22)
    c: Block(g73)
    c: Coincident(g70,g69)
    c: Coincident(g70,g68)
    c: Coincident(g74,g9)
    c: Block(g74)
    c: Distance(g71) = 2.5
    c: Block(g64)
    c: Block(g46)
    c: Block(g59)
    c: Coincident(g75,g64)
    c: Vertical(g75)
    c: Coincident(g76,g64)
    c: Vertical(g76)
    c: Coincident(g77,g76)
    c: Horizontal(g77)
    c: Coincident(g78,g34)
    c: Coincident(g78,g28)
    c: Horizontal(g78)
    c: Coincident(g79,g28)
    c: Coincident(g79,g46)
    c: Coincident(g80,g40)
    c: Coincident(g80,g46)
    c: Horizontal(g80)
    c: Coincident(g81,g34)
    c: Coincident(g81,g40)
    c: Vertical(g81)
    c: Block(g34)
    c: Block(g40)
    c: Block(g28)
    c: Coincident(g82,g75)
    c: Coincident(g82,g16)
    c: Horizontal(g82)
    c: Coincident(g83,g16)
    c: Block(g82)
    c: Block(g83)
    c: Block(g16)
    c: Coincident(g84,g83)
    c: Block(g84)
    c: Coincident(g85,g84)
    c: Block(g85)
    c: Coincident(g86,g85)
    c: Coincident(g87,g86)
    c: Coincident(g87,g71)
    c: Block(g87)
    c: Coincident(g88,g71)
    c: Coincident(g88,g3)
    c: Block(g88)
    c: Coincident(g89,g74)
    c: Coincident(g89,g68)
    c: Block(g70)
    c: Block(g68)
    c: Block(g69)
    c: Block(g22)
    c: Block(g50)
    c: Block(g56)
    c: Horizontal(g90)
    c: Distance(g90) = 7
    c: Horizontal(g91)
    c: Distance(g91) = 7
    c: Vertical(g92)
    c: Distance(g92) = 4
    c: Vertical(g93)
    c: Distance(g93) = 10
    c: Coincident(g94,g93)
    c: Coincident(g95,g92)
    c: Block(g95)
    c: Block(g94)
    c: Coincident(g96,g94)
    c: Coincident(g96,g90)
    c: Vertical(g96)
    c: Coincident(g97,g95)
    c: Coincident(g97,g91)
    c: Vertical(g97)
    c: Coincident(g98,g92)
    c: Coincident(g98,g93)
    c: Horizontal(g98)
    c: Horizontal(g99)
    c: Distance(g99) = 4
    c: Horizontal(g100)
    c: Distance(g100) = 4
    c: Coincident(g101,g99)
    c: Vertical(g101)
    c: Coincident(g102,g100)
    c: Vertical(g102)
    c: Distance(g101) = 4
    c: Distance(g102) = 4
    c: Coincident(g103,g101)
    c: Coincident(g103,g102)
    c: Block(g103)
    c: Coincident(g104,g56)
    c: Coincident(g104,g90)
    c: Vertical(g104)
    c: Block(g104)
    c: Coincident(g105,g91)
    c: Coincident(g105,g77)
    c: Vertical(g105)
    c: Block(g77)
    c: Block(g105)
    c: Coincident(g106,g100)
    c: Coincident(g106,g50)
    c: Vertical(g106)
    c: Coincident(g107,g22)
    c: Coincident(g107,g99)
    c: Vertical(g107)
FEATURE [Sketcher::SketchObject] Sketch009  label="middleBottom"
  FullyConstrained = true
  sketch-geometry (109):
    g0: Circle CenterX=175.022 CenterY=5.37834 CenterZ=0 NormalX=0 NormalY=0 NormalZ=1 AngleXU=0 Radius=1
    g1: Circle CenterX=179.022 CenterY=7.57463 CenterZ=0 NormalX=0 NormalY=0 NormalZ=1 AngleXU=0 Radius=1
    g2: Circle CenterX=179.022 CenterY=5.34704 CenterZ=0 NormalX=0 NormalY=0 NormalZ=1 AngleXU=0 Radius=1
    g3: BSplineCurve PolesCount=3 KnotsCount=2 Degree=2 IsPeriodic=0
    g4: GeomPoint X=175.022 Y=5.37834 Z=0
    g5: GeomPoint X=179.022 Y=5.34704 Z=0
    g6: Circle CenterX=189.124 CenterY=5.37834 CenterZ=0 NormalX=0 NormalY=0 NormalZ=1 AngleXU=0 Radius=1
    g7: Circle CenterX=185.124 CenterY=7.57463 CenterZ=0 NormalX=0 NormalY=0 NormalZ=1 AngleXU=0 Radius=1
    g8: Circle CenterX=185.124 CenterY=5.34704 CenterZ=0 NormalX=0 NormalY=0 NormalZ=1 AngleXU=0 Radius=1
    g9: BSplineCurve PolesCount=3 KnotsCount=2 Degree=2 IsPeriodic=0
    g10: GeomPoint X=189.124 Y=5.37834 Z=0
    g11: GeomPoint X=185.124 Y=5.34704 Z=0
    g12: Circle CenterX=224.513 CenterY=-14.0532 CenterZ=0 NormalX=0 NormalY=0 NormalZ=1 AngleXU=0 Radius=1
    g13: Circle CenterX=236.584 CenterY=-24.2775 CenterZ=0 NormalX=0 NormalY=0 NormalZ=1 AngleXU=0 Radius=1
    g14: BSplineCurve PolesCount=3 KnotsCount=2 Degree=2 IsPeriodic=0
    g15: GeomPoint X=236.584 Y=-24.2775 Z=0
    g16: Circle CenterX=125.607 CenterY=-21.7539 CenterZ=0 NormalX=0 NormalY=0 NormalZ=1 AngleXU=0 Radius=1
    g17: Circle CenterX=139.632 CenterY=-14.0532 CenterZ=0 NormalX=0 NormalY=0 NormalZ=1 AngleXU=0 Radius=1
    g18: Circle CenterX=127.325 CenterY=-24.2775 CenterZ=0 NormalX=0 NormalY=0 NormalZ=1 AngleXU=0 Radius=1
    g19: BSplineCurve PolesCount=3 KnotsCount=2 Degree=2 IsPeriodic=0
    g20: GeomPoint X=125.607 Y=-21.7539 Z=0
    g21: GeomPoint X=127.325 Y=-24.2775 Z=0
    g22: Circle CenterX=179.022 CenterY=-85.8163 CenterZ=0 NormalX=0 NormalY=0 NormalZ=1 AngleXU=0 Radius=1
    g23: Circle CenterX=179.022 CenterY=-91.7794 CenterZ=0 NormalX=0 NormalY=0 NormalZ=1 AngleXU=0 Radius=1
    g24: Circle CenterX=171.895 CenterY=-91.8014 CenterZ=0 NormalX=0 NormalY=0 NormalZ=1 AngleXU=0 Radius=1
    g25: BSplineCurve PolesCount=3 KnotsCount=2 Degree=2 IsPeriodic=0
    g26: GeomPoint X=179.022 Y=-85.8163 Z=0
    g27: GeomPoint X=171.895 Y=-91.8014 Z=0
    g28: Circle CenterX=185.124 CenterY=-86.2028 CenterZ=0 NormalX=0 NormalY=0 NormalZ=1 AngleXU=0 Radius=1
    g29: Circle CenterX=185.124 CenterY=-91.7794 CenterZ=0 NormalX=0 NormalY=0 NormalZ=1 AngleXU=0 Radius=1
    g30: Circle CenterX=191.747 CenterY=-91.7794 CenterZ=0 NormalX=0 NormalY=0 NormalZ=1 AngleXU=0 Radius=1
    g31: BSplineCurve PolesCount=3 KnotsCount=2 Degree=2 IsPeriodic=0
    g32: GeomPoint X=185.124 Y=-86.2028 Z=0
    g33: GeomPoint X=191.747 Y=-91.7794 Z=0
    g34: BSplineCurve PolesCount=5 KnotsCount=3 Degree=3 IsPeriodic=0
    g35: LineSegment StartX=132.072 StartY=-100.779 StartZ=0 EndX=132.072 EndY=-103.779 EndZ=0
    g36: GeomPoint X=232.072 Y=-94.7794 Z=0
    g37: GeomPoint X=223.072 Y=-97.7794 Z=0
    g38: Circle CenterX=232.072 CenterY=-94.7794 CenterZ=0 NormalX=0 NormalY=0 NormalZ=1 AngleXU=0 Radius=1
    g39: Circle CenterX=232.072 CenterY=-100.779 CenterZ=0 NormalX=0 NormalY=0 NormalZ=1 AngleXU=0 Radius=1
    g40: BSplineCurve PolesCount=5 KnotsCount=3 Degree=3 IsPeriodic=0
    g41: GeomPoint X=232.072 Y=-100.779 Z=0
    g42: LineSegment StartX=123.656 StartY=-37.1092 StartZ=0 EndX=122.136 EndY=-35.2714 EndZ=0
    g43: LineSegment StartX=117.05 StartY=-39.4781 StartZ=0 EndX=115.291 EndY=-37.3514 EndZ=0
    g44: LineSegment StartX=120.377 StartY=-33.1447 StartZ=0 EndX=118.86 EndY=-31.3104 EndZ=0
    g45: ArcOfCircle CenterX=116.562 CenterY=-19.6236 CenterZ=0 NormalX=0 NormalY=0 NormalZ=1 AngleXU=0 Radius=4.24264 StartAngle=1.28753 EndAngle=5.99992
    g46: LineSegment StartX=240.266 StartY=-37.1092 StartZ=0 EndX=189.124 EndY=5.37834 EndZ=0
    g47: LineSegment StartX=191.747 StartY=-91.7794 StartZ=0 EndX=232.072 EndY=-91.7794 EndZ=0
    g48: LineSegment StartX=232.072 StartY=-91.7794 StartZ=0 EndX=232.072 EndY=-94.7794 EndZ=0
    g49: LineSegment StartX=232.072 StartY=-100.779 StartZ=0 EndX=232.072 EndY=-103.779 EndZ=0
    g50: LineSegment StartX=132.072 StartY=-103.779 StartZ=0 EndX=232.072 EndY=-103.779 EndZ=0
    g51: LineSegment StartX=132.072 StartY=-91.8014 StartZ=0 EndX=132.072 EndY=-94.7791 EndZ=0
    g52: LineSegment StartX=132.072 StartY=-91.8014 StartZ=0 EndX=171.895 EndY=-91.8014 EndZ=0
    g53: LineSegment StartX=179.022 StartY=-85.8163 StartZ=0 EndX=179.022 EndY=5.34704 EndZ=0
    g54: LineSegment StartX=175.022 StartY=5.37834 StartZ=0 EndX=123.656 EndY=-37.1092 EndZ=0
    g55: LineSegment StartX=185.124 StartY=5.34704 StartZ=0 EndX=185.124 EndY=-86.2028 EndZ=0
    g56: LineSegment StartX=122.136 StartY=-35.2714 StartZ=0 EndX=117.05 EndY=-39.4781 EndZ=0
    g57: LineSegment StartX=115.291 StartY=-37.3514 StartZ=0 EndX=120.377 EndY=-33.1447 EndZ=0
    g58: LineSegment StartX=118.86 StartY=-31.3104 StartZ=0 EndX=127.325 EndY=-24.2775 EndZ=0
    g59: LineSegment StartX=125.607 StartY=-21.7539 StartZ=0 EndX=124.815 EndY=-22.1887 EndZ=0
    g60: LineSegment StartX=123.265 StartY=-19.3655 StartZ=0 EndX=124.815 EndY=-22.1887 EndZ=0
    g61: LineSegment StartX=120.636 StartY=-20.8094 StartZ=0 EndX=123.265 EndY=-19.3655 EndZ=0
    g62: LineSegment StartX=117.748 StartY=-15.55 StartZ=0 EndX=120.377 EndY=-14.1062 EndZ=0
    g63: LineSegment StartX=120.377 StartY=-14.1062 StartZ=0 EndX=118.934 EndY=-11.4765 EndZ=0
    g64: LineSegment StartX=236.584 StartY=-24.2775 StartZ=0 EndX=245.072 EndY=-31.3037 EndZ=0
    g65: LineSegment StartX=245.072 StartY=-31.3037 StartZ=0 EndX=243.535 EndY=-33.1602 EndZ=0
    g66: LineSegment StartX=243.535 StartY=-33.1602 StartZ=0 EndX=248.619 EndY=-37.3688 EndZ=0
    g67: LineSegment StartX=248.619 StartY=-37.3688 StartZ=0 EndX=246.855 EndY=-39.5064 EndZ=0
    g68: LineSegment StartX=246.855 StartY=-39.5064 StartZ=0 EndX=241.778 EndY=-35.2889 EndZ=0
    g69: LineSegment StartX=241.778 StartY=-35.2889 StartZ=0 EndX=240.266 EndY=-37.1092 EndZ=0
    g70: LineSegment StartX=243.628 StartY=-14.0323 StartZ=0 EndX=246.258 EndY=-15.476 EndZ=0
    g71: LineSegment StartX=240.741 StartY=-19.2917 StartZ=0 EndX=243.37 EndY=-20.7355 EndZ=0
    g72: ArcOfCircle CenterX=247.444 CenterY=-19.5496 CenterZ=0 NormalX=0 NormalY=0 NormalZ=1 AngleXU=0 Radius=4.24264 StartAngle=3.4249 EndAngle=8.13729
    g73: LineSegment StartX=240.741 StartY=-19.2917 StartZ=0 EndX=239.201 EndY=-22.0968 EndZ=0
    g74: LineSegment StartX=238.538 StartY=-21.7516 StartZ=0 EndX=239.201 EndY=-22.0968 EndZ=0
    g75: LineSegment StartX=245.072 StartY=-11.4025 StartZ=0 EndX=243.628 EndY=-14.0323 EndZ=0
    g76-g91: Circle x16 (B-spline internal-alignment scaffolding for g92; pole/knot coordinates omitted)
    g92: BSplineCurve PolesCount=16 KnotsCount=14 Degree=3 IsPeriodic=0
    g93-g106: GeomPoint x14 (B-spline internal-alignment scaffolding for g92; pole/knot coordinates omitted)
    g107: LineSegment StartX=165.871 StartY=14.2956 StartZ=0 EndX=118.934 EndY=-11.4765 EndZ=0
    g108: LineSegment StartX=198.264 StartY=14.2963 StartZ=0 EndX=245.072 EndY=-11.4025 EndZ=0
  constraints (146):
    c: Weight(g0) = 1
    c: Equal(g0,g1)
    c: Equal(g0,g2)
    c: InternalAlignment(g0,g3)
    c: InternalAlignment(g1,g3)
    c: InternalAlignment(g2,g3)
    c: InternalAlignment(g4,g3)
    c: InternalAlignment(g5,g3)
    c: Weight(g6) = 1
    c: Equal(g6,g7)
    c: Equal(g6,g8)
    c: InternalAlignment(g6,g9)
    c: InternalAlignment(g7,g9)
    c: InternalAlignment(g8,g9)
    c: InternalAlignment(g10,g9)
    c: InternalAlignment(g11,g9)
    c: Block(g9)
    c: Block(g3)
    c: InternalAlignment(g12,g14)
    c: InternalAlignment(g13,g14)
    c: InternalAlignment(g15,g14)
    c: Block(g14)
    c: Weight(g16) = 1
    c: Equal(g16,g17)
    c: Equal(g16,g18)
    c: InternalAlignment(g16,g19)
    c: InternalAlignment(g17,g19)
    c: InternalAlignment(g18,g19)
    c: InternalAlignment(g20,g19)
    c: InternalAlignment(g21,g19)
    c: Block(g19)
    c: Weight(g22) = 1
    c: Equal(g22,g23)
    c: Equal(g22,g24)
    c: InternalAlignment(g22,g25)
    c: InternalAlignment(g23,g25)
    c: InternalAlignment(g24,g25)
    c: InternalAlignment(g26,g25)
    c: InternalAlignment(g27,g25)
    c: Weight(g28) = 1
    c: Equal(g28,g29)
    c: Equal(g28,g30)
    c: InternalAlignment(g28,g31)
    c: InternalAlignment(g29,g31)
    c: InternalAlignment(g30,g31)
    c: InternalAlignment(g32,g31)
    c: InternalAlignment(g33,g31)
    c: Block(g31)
    c: Block(g25)
    c: Block(g34)
    c: Coincident(g35,g34)
    c: Vertical(g35)
    c: Block(g35)
    c: Equal(g38,g39)
    c: InternalAlignment(g38,g40)
    c: InternalAlignment(g39,g40)
    c: InternalAlignment(g36,g40)
    c: InternalAlignment(g37,g40)
    c: InternalAlignment(g41,g40)
    c: Block(g40)
    c: Distance(g42) = 2.385
    c: Distance(g43) = 2.76
    c: Parallel(g42,g44)
    c: Block(g45)
    c: Coincident(g46,g9)
    c: Coincident(g47,g31)
    c: Horizontal(g47)
    c: Block(g47)
    c: Coincident(g48,g47)
    c: Coincident(g48,g40)
    c: Vertical(g48)
    c: Block(g48)
    c: Coincident(g49,g40)
    c: Vertical(g49)
    c: Block(g49)
    c: Coincident(g50,g35)
    c: Coincident(g50,g49)
    c: Horizontal(g50)
    c: Block(g50)
    c: Coincident(g51,g34)
    c: Vertical(g51)
    c: Coincident(g52,g51)
    c: Coincident(g52,g25)
    c: Horizontal(g52)
    c: Coincident(g53,g25)
    c: Coincident(g53,g3)
    c: Vertical(g53)
    c: Coincident(g54,g3)
    c: Coincident(g54,g42)
    c: Coincident(g55,g9)
    c: Coincident(g55,g31)
    c: Vertical(g55)
    c: Block(g42)
    c: Coincident(g56,g42)
    c: Coincident(g56,g43)
    c: Coincident(g57,g43)
    c: Coincident(g57,g44)
    c: Block(g57)
    c: Block(g56)
    c: Coincident(g58,g44)
    c: Coincident(g58,g19)
    c: Block(g58)
    c: Coincident(g59,g19)
    c: Block(g59)
    c: Coincident(g60,g59)
    c: Block(g60)
    c: Coincident(g61,g45)
    c: Coincident(g61,g60)
    c: Coincident(g62,g45)
    c: Coincident(g63,g62)
    c: Block(g63)
    c: Coincident(g64,g14)
    c: Block(g64)
    c: Coincident(g65,g64)
    c: Coincident(g66,g65)
    c: Coincident(g67,g66)
    c: Coincident(g68,g67)
    c: Coincident(g69,g68)
    c: Coincident(g69,g46)
    c: Block(g46)
    c: Block(g68)
    c: Block(g66)
    c: Distance(g70) = 3
    c: Distance(g71) = 3
    c: Coincident(g72,g70)
    c: Coincident(g72,g71)
    c: Block(g72)
    c: Coincident(g73,g71)
    c: Distance(g73) = 3.2
    c: Coincident(g74,g14)
    c: Coincident(g74,g73)
    c: Coincident(g75,g70)
    c: Block(g75)
    c: Block(g73)
    c: Distance(g63) = 3
    c: Distance(g60) = 3.22077
    c: Weight(g76) = 1
    c: Equal(g76, g77-g91) x15
    c: InternalAlignment(g76-g91 -> g92) x16
    c: InternalAlignment(g93-g106 -> g92) x14
    c: Coincident(g107,g92)
    c: Coincident(g107,g63)
    c: Block(g107)
    c: Block(g92)
    c: Coincident(g108,g92)
    c: Coincident(g108,g75)
FEATURE [Sketcher::SketchObject] Sketch010  label="legBottomBack"
  FullyConstrained = false
  MapMode = 4
  Placement = pos=(0,0,0) rot=(0.57735,0.57735,0.57735;2.0944rad)
  sketch-geometry (44):
    g0: BSplineCurve PolesCount=3 KnotsCount=2 Degree=2 IsPeriodic=0
    g1: Circle CenterX=-199.665 CenterY=-138.314 CenterZ=0 NormalX=0 NormalY=0 NormalZ=1 AngleXU=0 Radius=1
    g2: GeomPoint X=-199.665 Y=-138.314 Z=0
    g3: LineSegment StartX=-199.665 StartY=-138.314 StartZ=0 EndX=-200.721 EndY=-141.122 EndZ=0
    g4: Circle CenterX=-17.0256 CenterY=-190.268 CenterZ=0 NormalX=0 NormalY=0 NormalZ=1 AngleXU=0 Radius=10.5072
    g5: Circle CenterX=-37.7758 CenterY=-187.672 CenterZ=0 NormalX=0 NormalY=0 NormalZ=1 AngleXU=0 Radius=5.64388
    g6: Circle CenterX=-51.4606 CenterY=-185.091 CenterZ=0 NormalX=0 NormalY=0 NormalZ=1 AngleXU=0 Radius=3.01653
    g7: Circle CenterX=-60.4835 CenterY=-182.688 CenterZ=0 NormalX=0 NormalY=0 NormalZ=1 AngleXU=0 Radius=2.12826
    g8: Circle CenterX=-3.29005 CenterY=-177.662 CenterZ=0 NormalX=0 NormalY=0 NormalZ=1 AngleXU=0 Radius=3.26661
    g9: ArcOfCircle CenterX=11.0205 CenterY=-198.019 CenterZ=0 NormalX=0 NormalY=0 NormalZ=1 AngleXU=0 Radius=13 StartAngle=2.78068 EndAngle=5.92131
    g10: LineSegment StartX=5.08312 StartY=-176.581 StartZ=0 EndX=-1.14188 EndY=-193.429 EndZ=0
    g11: ArcOfCircle CenterX=17.2475 CenterY=-181.166 CenterZ=0 NormalX=0 NormalY=0 NormalZ=1 AngleXU=0 Radius=13 StartAngle=1.21042 EndAngle=2.78109
    g12: LineSegment StartX=38.8952 StartY=-231.233 StartZ=0 EndX=39.9512 EndY=-228.425 EndZ=0
    g13: ArcOfCircle CenterX=46.9911 CenterY=-209.705 CenterZ=0 NormalX=0 NormalY=0 NormalZ=1 AngleXU=0 Radius=20 StartAngle=2.78766 EndAngle=4.35269
    g14: LineSegment StartX=23.7323 StartY=-126.969 StartZ=0 EndX=17.4091 EndY=-143.817 EndZ=0
    g15: ArcOfCircle CenterX=29.5716 CenterY=-148.408 CenterZ=0 NormalX=0 NormalY=0 NormalZ=1 AngleXU=0 Radius=13 StartAngle=2.78068 EndAngle=4.35262
    g16: ArcOfCircle CenterX=35.8967 CenterY=-131.555 CenterZ=0 NormalX=0 NormalY=0 NormalZ=1 AngleXU=0 Radius=13 StartAngle=1.21584 EndAngle=2.78109
    g17: ArcOfCircle CenterX=48.1805 CenterY=-98.7782 CenterZ=0 NormalX=0 NormalY=0 NormalZ=1 AngleXU=0 Radius=13 StartAngle=2.78068 EndAngle=4.35005
    g18: LineSegment StartX=42.354 StartY=-77.3391 StartZ=0 EndX=36.018 EndY=-94.1875 EndZ=0
    g19: ArcOfCircle CenterX=54.5183 CenterY=-81.9247 CenterZ=0 NormalX=0 NormalY=0 NormalZ=1 AngleXU=0 Radius=13 StartAngle=2.42113 EndAngle=2.78109
    g20: ArcOfCircle CenterX=20.184 CenterY=-217.506 CenterZ=0 NormalX=0 NormalY=0 NormalZ=1 AngleXU=0 Radius=3.81084 StartAngle=1.88136 EndAngle=6.80465
    g21: LineSegment StartX=38.4753 StartY=-115.966 StartZ=0 EndX=41.2852 EndY=-117.017 EndZ=0
    g22: ArcOfCircle CenterX=36.3663 CenterY=-113.042 CenterZ=0 NormalX=0 NormalY=0 NormalZ=1 AngleXU=0 Radius=3.60555 StartAngle=0.230024 EndAngle=5.3372
    g23: LineSegment StartX=39.8769 StartY=-112.22 StartZ=0 EndX=42.6867 EndY=-113.271 EndZ=0
    g24: LineSegment StartX=19.9036 StartY=-165.61 StartZ=0 EndX=22.7134 EndY=-166.661 EndZ=0
    g25: ArcOfCircle CenterX=17.7945 CenterY=-162.686 CenterZ=0 NormalX=0 NormalY=0 NormalZ=1 AngleXU=0 Radius=3.60555 StartAngle=0.230024 EndAngle=5.3372
    g26: LineSegment StartX=21.3051 StartY=-161.864 StartZ=0 EndX=24.1149 EndY=-162.915 EndZ=0
    g27: LineSegment StartX=41.085 StartY=-66.3176 StartZ=0 EndX=46.0385 EndY=-62.5254 EndZ=0
    g28: LineSegment StartX=48.9563 StartY=-66.3367 StartZ=0 EndX=44.7488 EndY=-73.3482 EndZ=0
    g29: ArcOfCircle CenterX=49.8795 CenterY=-62.6074 CenterZ=0 NormalX=0 NormalY=0 NormalZ=1 AngleXU=0 Radius=3.84187 StartAngle=4.46973 EndAngle=9.40343
    g30: LineSegment StartX=41.085 StartY=-66.3176 StartZ=0 EndX=8.65492 EndY=-152.553 EndZ=0
    g31: LineSegment StartX=43.5724 StartY=-110.934 StartZ=0 EndX=42.6867 EndY=-113.271 EndZ=0
    g32: LineSegment StartX=40.4148 StartY=-119.365 StartZ=0 EndX=41.2852 EndY=-117.017 EndZ=0
    g33: LineSegment StartX=21.8316 StartY=-169.001 StartZ=0 EndX=22.7134 EndY=-166.661 EndZ=0
    g34: LineSegment StartX=24.9948 StartY=-160.575 StartZ=0 EndX=24.1149 EndY=-162.915 EndZ=0
    g35: LineSegment StartX=23.1786 StartY=-202.622 StartZ=0 EndX=19.0195 EndY=-213.878 EndZ=0
    g36: LineSegment StartX=28.2308 StartY=-202.773 StartZ=0 EndX=23.4884 EndY=-215.608 EndZ=0
    g37: LineSegment StartX=-200.721 StartY=-141.122 StartZ=0 EndX=-79.0409 EndY=-186.881 EndZ=0
    g38: LineSegment StartX=-79.0409 StartY=-186.881 StartZ=0 EndX=-77.6329 EndY=-183.137 EndZ=0
    g39: LineSegment StartX=-76.2249 StartY=-179.393 StartZ=0 EndX=-72.8553 EndY=-180.66 EndZ=0
    g40: LineSegment StartX=-77.6329 StartY=-183.137 StartZ=0 EndX=-74.2633 EndY=-184.404 EndZ=0
    g41: ArcOfCircle CenterX=-71.1257 CenterY=-183.448 CenterZ=0 NormalX=0 NormalY=0 NormalZ=1 AngleXU=0 Radius=3.28025 StartAngle=3.43759 EndAngle=8.40938
    g42: LineSegment StartX=-76.2249 StartY=-179.393 StartZ=0 EndX=-74.4658 EndY=-174.715 EndZ=0
    g43: LineSegment StartX=-79.0409 StartY=-186.881 StartZ=0 EndX=38.8952 EndY=-231.233 EndZ=0
  constraints (81):
    c: Block(g9)
    c: Block(g11)
    c: InternalAlignment(g1,g0)
    c: InternalAlignment(g2,g0)
    c: Block(g0)
    c: Block(g4)
    c: Block(g8)
    c: Block(g5)
    c: Block(g6)
    c: Block(g7)
    c: Block(g13)
    c: Coincident(g12,g13)
    c: Block(g12)
    c: Coincident(g3,g0)
    c: Coincident(g10,g11)
    c: Coincident(g10,g9)
    c: Block(g15)
    c: Block(g16)
    c: Coincident(g14,g16)
    c: Coincident(g14,g15)
    c: Block(g17)
    c: Block(g19)
    c: Coincident(g18,g19)
    c: Coincident(g18,g17)
    c: Block(g20)
    c: Block(g22)
    c: Coincident(g23,g22)
    c: Coincident(g21,g22)
    c: Parallel(g23,g21)
    c: Block(g21)
    c: Block(g23)
    c: Block(g25)
    c: Coincident(g26,g25)
    c: Coincident(g24,g25)
    c: Parallel(g26,g24)
    c: Block(g24)
    c: Block(g26)
    c: Block(g27)
    c: Coincident(g29,g27)
    c: Coincident(g29,g28)
    c: Block(g29)
    c: Coincident(g30,g27)
    c: Coincident(g30,g0)
    c: Block(g28)
    c: Coincident(g31,g23)
    c: Block(g31)
    c: Coincident(g32,g21)
    c: Block(g32)
    c: Coincident(g33,g24)
    c: Coincident(g34,g26)
    c: Block(g34)
    c: Block(g33)
    c: Coincident(g35,g9)
    c: Coincident(g35,g20)
    c: Block(g35)
    c: Coincident(g11,g33)
    c: Coincident(g15,g34)
    c: Coincident(g16,g32)
    c: Coincident(g17,g31)
    c: Coincident(g19,g28)
    c: Coincident(g36,g13)
    c: Coincident(g36,g20)
    c: Coincident(g37,g3)
    c: Block(g3)
    c: Perpendicular(g37,g3)
    c: Distance(g37) = 130
    c: Coincident(g38,g37)
    c: Distance(g38) = 4
    c: Perpendicular(g37,g38)
    c: Distance(g39) = 3.6
    c: Coincident(g40,g38)
    c: Distance(g40) = 3.6
    c: Block(g39)
    c: Block(g40)
    c: Coincident(g41,g39)
    c: Coincident(g41,g40)
    c: Coincident(g42,g39)
    c: Parallel(g38,g42)
    c: PointOnObject(g42,g0)
    c: Coincident(g43,g37)
    c: Coincident(g43,g12)
FEATURE [Sketcher::SketchObject] Sketch011  label="legBottomFront"
  FullyConstrained = true
  MapMode = 4
  Placement = pos=(0,0,0) rot=(0.57735,0.57735,0.57735;2.0944rad)
  sketch-geometry (13):
    g0: LineSegment StartX=-199.665 StartY=-138.314 StartZ=0 EndX=-200.721 EndY=-141.122 EndZ=0
    g1: LineSegment StartX=-200.721 StartY=-141.122 StartZ=0 EndX=-79.0409 EndY=-186.881 EndZ=0
    g2: ArcOfCircle CenterX=-71.1257 CenterY=-183.448 CenterZ=0 NormalX=0 NormalY=0 NormalZ=1 AngleXU=0 Radius=3.28025 StartAngle=3.43759 EndAngle=8.40938
    g3: LineSegment StartX=-74.4626 StartY=-174.707 StartZ=0 EndX=-76.2249 EndY=-179.393 EndZ=0
    g4: LineSegment StartX=-76.2249 StartY=-179.393 StartZ=0 EndX=-72.8553 EndY=-180.66 EndZ=0
    g5: Circle CenterX=-74.4626 CenterY=-174.707 CenterZ=0 NormalX=0 NormalY=0 NormalZ=1 AngleXU=0 Radius=1
    g6: Circle CenterX=-130.185 CenterY=-164.454 CenterZ=0 NormalX=0 NormalY=0 NormalZ=1 AngleXU=0 Radius=1
    g7: Circle CenterX=-199.665 CenterY=-138.314 CenterZ=0 NormalX=0 NormalY=0 NormalZ=1 AngleXU=0 Radius=1
    g8: BSplineCurve PolesCount=3 KnotsCount=2 Degree=2 IsPeriodic=0
    g9: GeomPoint X=-74.4626 Y=-174.707 Z=0
    g10: GeomPoint X=-199.665 Y=-138.314 Z=0
    g11: LineSegment StartX=-77.6329 StartY=-183.137 StartZ=0 EndX=-79.0409 EndY=-186.881 EndZ=0
    g12: LineSegment StartX=-77.6329 StartY=-183.137 StartZ=0 EndX=-74.2633 EndY=-184.404 EndZ=0
  constraints (24):
    c: Coincident(g1,g0)
    c: Block(g0)
    c: Perpendicular(g1,g0)
    c: Distance(g1) = 130
    c: Coincident(g4,g3)
    c: Coincident(g4,g2)
    c: Block(g2)
    c: Block(g4)
    c: Coincident(g8,g3)
    c: Weight(g5) = 1
    c: Equal(g5,g6)
    c: Equal(g5,g7)
    c: Coincident(g8,g0)
    c: InternalAlignment(g5,g8)
    c: InternalAlignment(g6,g8)
    c: InternalAlignment(g7,g8)
    c: InternalAlignment(g9,g8)
    c: InternalAlignment(g10,g8)
    c: Block(g8)
    c: Block(g3)
    c: Coincident(g11,g1)
    c: Coincident(g12,g11)
    c: Coincident(g12,g2)
    c: Block(g12)
